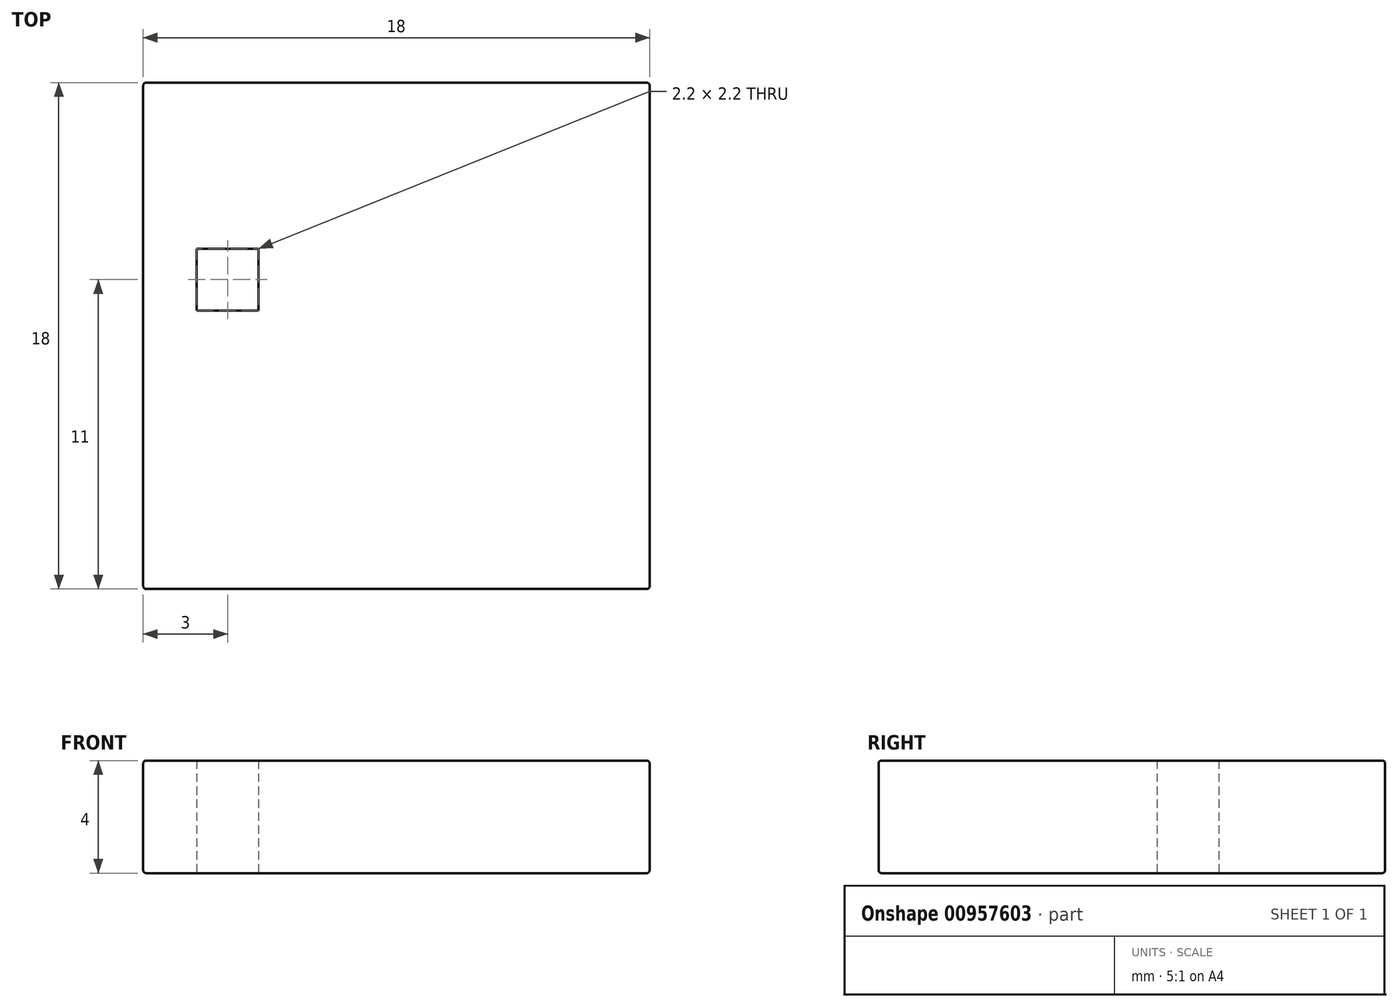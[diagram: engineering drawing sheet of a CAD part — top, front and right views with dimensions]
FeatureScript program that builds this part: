
annotation { "Feature Type Name" : "Feature", "Feature Type Description" : "" }
export const myFeature = defineFeature(function(context is Context, id is Id, definition is map)
    precondition{}
    {
        {
            var Q0;
            Q0=qCreatedBy(makeId("Top.planeOp"),FACE);
            var sketch = newSketch(context, id + "F0", { "sketchPlane" : qUnion([Q0])});
            skLineSegment(sketch, "E0.bottom", {"start": v(-9, 9) * mm, "end": v(9, 9) * mm});
            skLineSegment(sketch, "E0.top", {"start": v(-9, -9) * mm, "end": v(9, -9) * mm});
            skLineSegment(sketch, "E0.left", {"start": v(-9, 9) * mm, "end": v(-9, -9) * mm});
            skLineSegment(sketch, "E0.right", {"start": v(9, 9) * mm, "end": v(9, -9) * mm});
            skPoint(sketch, "E0.middle", {"position": v(0, 0) * mm});
            skLineSegment(sketch, "E1", {"start": v(-8, 9) * mm, "end": v(-8, -9) * mm});
            skLineSegment(sketch, "E2", {"start": v(-7.1, 9) * mm, "end": v(-7.1, -9) * mm});
            skLineSegment(sketch, "E3", {"start": v(-6.9, 9) * mm, "end": v(-6.9, -9) * mm});
            skLineSegment(sketch, "E4", {"start": v(-5.1, 9) * mm, "end": v(-5.1, -9) * mm});
            skLineSegment(sketch, "E5", {"start": v(-4.9, 9) * mm, "end": v(-4.9, -9) * mm});
            skLineSegment(sketch, "E6", {"start": v(-3.1, 9) * mm, "end": v(-3.1, -9) * mm});
            skLineSegment(sketch, "E7", {"start": v(-2.9, 9) * mm, "end": v(-2.9, -9) * mm});
            skLineSegment(sketch, "E8", {"start": v(-1.1, 9) * mm, "end": v(-1.1, -9) * mm});
            skLineSegment(sketch, "E9", {"start": v(-0.9, 9) * mm, "end": v(-0.9, -9) * mm});
            skLineSegment(sketch, "E10", {"start": v(0.9, 9) * mm, "end": v(0.9, -9) * mm});
            skLineSegment(sketch, "E11", {"start": v(1.1, 9) * mm, "end": v(1.1, -9) * mm});
            skLineSegment(sketch, "E12", {"start": v(2.9, 9) * mm, "end": v(2.9, -9) * mm});
            skLineSegment(sketch, "E13", {"start": v(3.1, 9) * mm, "end": v(3.1, -9) * mm});
            skLineSegment(sketch, "E14", {"start": v(4.9, 9) * mm, "end": v(4.9, -9) * mm});
            skLineSegment(sketch, "E15", {"start": v(5.1, 9) * mm, "end": v(5.1, -9) * mm});
            skLineSegment(sketch, "E16", {"start": v(6.9, 9) * mm, "end": v(6.9, -9) * mm});
            skLineSegment(sketch, "E17", {"start": v(7.1, 9) * mm, "end": v(7.1, -9) * mm});
            skLineSegment(sketch, "E18", {"start": v(8, 9) * mm, "end": v(8, -9) * mm});
            skLineSegment(sketch, "E19", {"start": v(9, 8) * mm, "end": v(-9, 8) * mm});
            skLineSegment(sketch, "E20", {"start": v(9, 7.1) * mm, "end": v(-9, 7.1) * mm});
            skLineSegment(sketch, "E21", {"start": v(9, 6.9) * mm, "end": v(-9, 6.9) * mm});
            skLineSegment(sketch, "E22", {"start": v(9, 5.1) * mm, "end": v(-9, 5.1) * mm});
            skLineSegment(sketch, "E23", {"start": v(9, 4.9) * mm, "end": v(-9, 4.9) * mm});
            skLineSegment(sketch, "E24", {"start": v(9, 3.1) * mm, "end": v(-9, 3.1) * mm});
            skLineSegment(sketch, "E25", {"start": v(9, 2.9) * mm, "end": v(-9, 2.9) * mm});
            skLineSegment(sketch, "E26", {"start": v(9, 1.1) * mm, "end": v(-9, 1.1) * mm});
            skLineSegment(sketch, "E27", {"start": v(9, 0.9) * mm, "end": v(-9, 0.9) * mm});
            skLineSegment(sketch, "E28", {"start": v(9, -0.9) * mm, "end": v(-9, -0.9) * mm});
            skLineSegment(sketch, "E29", {"start": v(9, -1.1) * mm, "end": v(-9, -1.1) * mm});
            skLineSegment(sketch, "E30", {"start": v(9, -2.9) * mm, "end": v(-9, -2.9) * mm});
            skLineSegment(sketch, "E31", {"start": v(9, -3.1) * mm, "end": v(-9, -3.1) * mm});
            skLineSegment(sketch, "E32", {"start": v(9, -4.9) * mm, "end": v(-9, -4.9) * mm});
            skLineSegment(sketch, "E33", {"start": v(9, -5.1) * mm, "end": v(-9, -5.1) * mm});
            skLineSegment(sketch, "E34", {"start": v(9, -6.9) * mm, "end": v(-9, -6.9) * mm});
            skLineSegment(sketch, "E35", {"start": v(9, -7.1) * mm, "end": v(-9, -7.1) * mm});
            skLineSegment(sketch, "E36", {"start": v(9, -8) * mm, "end": v(-9, -8) * mm});
            skSolve(sketch);
        }
        {
            var Q0;
            {var subQ0=sQuery(id+"F0.wireOp",EDGE,"E30");var subQ1=sQuery(id+"F0.wireOp",EDGE,"E10");var subQ2=makeQuery(id+"F0.imprint","INTERSECT",VERTEX,{"derivedFrom":[subQ1,subQ0]});Q0=makeQuery(id+"F0.imprint","IMPRINT",FACE,{"disambiguationData":[TD([[makeQuery(id+"F0.imprint","IMPRINT",EDGE,{"disambiguationData":[TD([[subQ2,-1.0]])],"derivedFrom":subQ1}),1.0]])]});}
            var Q1;
            {var subQ0=sQuery(id+"F0.wireOp",EDGE,"E26");var subQ1=sQuery(id+"F0.wireOp",EDGE,"E11");var subQ2=makeQuery(id+"F0.imprint","INTERSECT",VERTEX,{"derivedFrom":[subQ1,subQ0]});Q1=makeQuery(id+"F0.imprint","IMPRINT",FACE,{"disambiguationData":[TD([[makeQuery(id+"F0.imprint","IMPRINT",EDGE,{"disambiguationData":[TD([[subQ2,-1.0]])],"derivedFrom":subQ1}),1.0]])]});}
            var Q2;
            {var subQ0=sQuery(id+"F0.wireOp",EDGE,"E25");var subQ1=sQuery(id+"F0.wireOp",EDGE,"E8");var subQ2=makeQuery(id+"F0.imprint","INTERSECT",VERTEX,{"derivedFrom":[subQ1,subQ0]});Q2=makeQuery(id+"F0.imprint","IMPRINT",FACE,{"disambiguationData":[TD([[makeQuery(id+"F0.imprint","IMPRINT",EDGE,{"disambiguationData":[TD([[subQ2,-1.0]])],"derivedFrom":subQ1}),1.0]])]});}
            var Q3;
            {var subQ0=sQuery(id+"F0.wireOp",EDGE,"E24");var subQ1=sQuery(id+"F0.wireOp",EDGE,"E10");var subQ2=makeQuery(id+"F0.imprint","INTERSECT",VERTEX,{"derivedFrom":[subQ1,subQ0]});Q3=makeQuery(id+"F0.imprint","IMPRINT",FACE,{"disambiguationData":[TD([[makeQuery(id+"F0.imprint","IMPRINT",EDGE,{"disambiguationData":[TD([[subQ2,-1.0]])],"derivedFrom":subQ1}),1.0]])]});}
            var Q4;
            {var subQ0=sQuery(id+"F0.wireOp",EDGE,"E30");var subQ1=sQuery(id+"F0.wireOp",EDGE,"E15");var subQ2=makeQuery(id+"F0.imprint","INTERSECT",VERTEX,{"derivedFrom":[subQ1,subQ0]});Q4=makeQuery(id+"F0.imprint","IMPRINT",FACE,{"disambiguationData":[TD([[makeQuery(id+"F0.imprint","IMPRINT",EDGE,{"disambiguationData":[TD([[subQ2,-1.0]])],"derivedFrom":subQ1}),1.0]])]});}
            var Q5;
            {var subQ0=sQuery(id+"F0.wireOp",EDGE,"E35");var subQ1=sQuery(id+"F0.wireOp",EDGE,"E12");var subQ2=makeQuery(id+"F0.imprint","INTERSECT",VERTEX,{"derivedFrom":[subQ1,subQ0]});Q5=makeQuery(id+"F0.imprint","IMPRINT",FACE,{"disambiguationData":[TD([[makeQuery(id+"F0.imprint","IMPRINT",EDGE,{"disambiguationData":[TD([[subQ2,-1.0]])],"derivedFrom":subQ1}),1.0]])]});}
            var Q6;
            {var subQ0=sQuery(id+"F0.wireOp",EDGE,"E35");var subQ1=sQuery(id+"F0.wireOp",EDGE,"E14");var subQ2=makeQuery(id+"F0.imprint","INTERSECT",VERTEX,{"derivedFrom":[subQ1,subQ0]});Q6=makeQuery(id+"F0.imprint","IMPRINT",FACE,{"disambiguationData":[TD([[makeQuery(id+"F0.imprint","IMPRINT",EDGE,{"disambiguationData":[TD([[subQ2,-1.0]])],"derivedFrom":subQ1}),1.0]])]});}
            var Q7;
            {var subQ0=sQuery(id+"F0.wireOp",EDGE,"E32");var subQ1=sQuery(id+"F0.wireOp",EDGE,"E10");var subQ2=makeQuery(id+"F0.imprint","INTERSECT",VERTEX,{"derivedFrom":[subQ1,subQ0]});Q7=makeQuery(id+"F0.imprint","IMPRINT",FACE,{"disambiguationData":[TD([[makeQuery(id+"F0.imprint","IMPRINT",EDGE,{"disambiguationData":[TD([[subQ2,-1.0]])],"derivedFrom":subQ1}),1.0]])]});}
            var Q8;
            {var subQ0=sQuery(id+"F0.wireOp",EDGE,"E23");var subQ1=sQuery(id+"F0.wireOp",EDGE,"E14");var subQ2=makeQuery(id+"F0.imprint","INTERSECT",VERTEX,{"derivedFrom":[subQ1,subQ0]});Q8=makeQuery(id+"F0.imprint","IMPRINT",FACE,{"disambiguationData":[TD([[makeQuery(id+"F0.imprint","IMPRINT",EDGE,{"disambiguationData":[TD([[subQ2,-1.0]])],"derivedFrom":subQ1}),1.0]])]});}
            var Q9;
            {var subQ0=sQuery(id+"F0.wireOp",EDGE,"E23");var subQ1=sQuery(id+"F0.wireOp",EDGE,"E16");var subQ2=makeQuery(id+"F0.imprint","INTERSECT",VERTEX,{"derivedFrom":[subQ1,subQ0]});Q9=makeQuery(id+"F0.imprint","IMPRINT",FACE,{"disambiguationData":[TD([[makeQuery(id+"F0.imprint","IMPRINT",EDGE,{"disambiguationData":[TD([[subQ2,-1.0]])],"derivedFrom":subQ1}),1.0]])]});}
            var Q10;
            {var subQ0=sQuery(id+"F0.wireOp",EDGE,"E22");var subQ1=sQuery(id+"F0.wireOp",EDGE,"E9");var subQ2=makeQuery(id+"F0.imprint","INTERSECT",VERTEX,{"derivedFrom":[subQ1,subQ0]});Q10=makeQuery(id+"F0.imprint","IMPRINT",FACE,{"disambiguationData":[TD([[makeQuery(id+"F0.imprint","IMPRINT",EDGE,{"disambiguationData":[TD([[subQ2,-1.0]])],"derivedFrom":subQ1}),1.0]])]});}
            var Q11;
            {var subQ0=sQuery(id+"F0.wireOp",EDGE,"E27");var subQ1=sQuery(id+"F0.wireOp",EDGE,"E10");var subQ2=makeQuery(id+"F0.imprint","INTERSECT",VERTEX,{"derivedFrom":[subQ1,subQ0]});Q11=makeQuery(id+"F0.imprint","IMPRINT",FACE,{"disambiguationData":[TD([[makeQuery(id+"F0.imprint","IMPRINT",EDGE,{"disambiguationData":[TD([[subQ2,-1.0]])],"derivedFrom":subQ1}),1.0]])]});}
            var Q12;
            {var subQ0=sQuery(id+"F0.wireOp",EDGE,"E31");var subQ1=sQuery(id+"F0.wireOp",EDGE,"E2");var subQ2=makeQuery(id+"F0.imprint","INTERSECT",VERTEX,{"derivedFrom":[subQ1,subQ0]});Q12=makeQuery(id+"F0.imprint","IMPRINT",FACE,{"disambiguationData":[TD([[makeQuery(id+"F0.imprint","IMPRINT",EDGE,{"disambiguationData":[TD([[subQ2,-1.0]])],"derivedFrom":subQ1}),1.0]])]});}
            var Q13;
            {var subQ0=sQuery(id+"F0.wireOp",EDGE,"E30");var subQ1=sQuery(id+"F0.wireOp",EDGE,"E13");var subQ2=makeQuery(id+"F0.imprint","INTERSECT",VERTEX,{"derivedFrom":[subQ1,subQ0]});Q13=makeQuery(id+"F0.imprint","IMPRINT",FACE,{"disambiguationData":[TD([[makeQuery(id+"F0.imprint","IMPRINT",EDGE,{"disambiguationData":[TD([[subQ2,-1.0]])],"derivedFrom":subQ1}),1.0]])]});}
            var Q14;
            {var subQ0=sQuery(id+"F0.wireOp",EDGE,"E33");var subQ1=sQuery(id+"F0.wireOp",EDGE,"E16");var subQ2=makeQuery(id+"F0.imprint","INTERSECT",VERTEX,{"derivedFrom":[subQ1,subQ0]});Q14=makeQuery(id+"F0.imprint","IMPRINT",FACE,{"disambiguationData":[TD([[makeQuery(id+"F0.imprint","IMPRINT",EDGE,{"disambiguationData":[TD([[subQ2,-1.0]])],"derivedFrom":subQ1}),1.0]])]});}
            var Q15;
            {var subQ0=sQuery(id+"F0.wireOp",EDGE,"E29");var subQ1=sQuery(id+"F0.wireOp",EDGE,"E8");var subQ2=makeQuery(id+"F0.imprint","INTERSECT",VERTEX,{"derivedFrom":[subQ1,subQ0]});Q15=makeQuery(id+"F0.imprint","IMPRINT",FACE,{"disambiguationData":[TD([[makeQuery(id+"F0.imprint","IMPRINT",EDGE,{"disambiguationData":[TD([[subQ2,-1.0]])],"derivedFrom":subQ1}),1.0]])]});}
            var Q16;
            {var subQ0=sQuery(id+"F0.wireOp",EDGE,"E26");var subQ1=sQuery(id+"F0.wireOp",EDGE,"E1");var subQ2=makeQuery(id+"F0.imprint","INTERSECT",VERTEX,{"derivedFrom":[subQ1,subQ0]});Q16=makeQuery(id+"F0.imprint","IMPRINT",FACE,{"disambiguationData":[TD([[makeQuery(id+"F0.imprint","IMPRINT",EDGE,{"disambiguationData":[TD([[subQ2,-1.0]])],"derivedFrom":subQ1}),1.0]])]});}
            var Q17;
            {var subQ0=sQuery(id+"F0.wireOp",EDGE,"E30");var subQ1=sQuery(id+"F0.wireOp",EDGE,"E12");var subQ2=makeQuery(id+"F0.imprint","INTERSECT",VERTEX,{"derivedFrom":[subQ1,subQ0]});Q17=makeQuery(id+"F0.imprint","IMPRINT",FACE,{"disambiguationData":[TD([[makeQuery(id+"F0.imprint","IMPRINT",EDGE,{"disambiguationData":[TD([[subQ2,-1.0]])],"derivedFrom":subQ1}),1.0]])]});}
            var Q18;
            {var subQ0=sQuery(id+"F0.wireOp",EDGE,"E29");var subQ1=sQuery(id+"F0.wireOp",EDGE,"E12");var subQ2=makeQuery(id+"F0.imprint","INTERSECT",VERTEX,{"derivedFrom":[subQ1,subQ0]});Q18=makeQuery(id+"F0.imprint","IMPRINT",FACE,{"disambiguationData":[TD([[makeQuery(id+"F0.imprint","IMPRINT",EDGE,{"disambiguationData":[TD([[subQ2,-1.0]])],"derivedFrom":subQ1}),1.0]])]});}
            var Q19;
            {var subQ0=sQuery(id+"F0.wireOp",EDGE,"E31");var subQ1=sQuery(id+"F0.wireOp",EDGE,"E6");var subQ2=makeQuery(id+"F0.imprint","INTERSECT",VERTEX,{"derivedFrom":[subQ1,subQ0]});Q19=makeQuery(id+"F0.imprint","IMPRINT",FACE,{"disambiguationData":[TD([[makeQuery(id+"F0.imprint","IMPRINT",EDGE,{"disambiguationData":[TD([[subQ2,-1.0]])],"derivedFrom":subQ1}),1.0]])]});}
            var Q20;
            {var subQ0=sQuery(id+"F0.wireOp",EDGE,"E29");var subQ1=sQuery(id+"F0.wireOp",EDGE,"E10");var subQ2=makeQuery(id+"F0.imprint","INTERSECT",VERTEX,{"derivedFrom":[subQ1,subQ0]});Q20=makeQuery(id+"F0.imprint","IMPRINT",FACE,{"disambiguationData":[TD([[makeQuery(id+"F0.imprint","IMPRINT",EDGE,{"disambiguationData":[TD([[subQ2,-1.0]])],"derivedFrom":subQ1}),1.0]])]});}
            var Q21;
            {var subQ0=sQuery(id+"F0.wireOp",EDGE,"E25");var subQ1=sQuery(id+"F0.wireOp",EDGE,"E16");var subQ2=makeQuery(id+"F0.imprint","INTERSECT",VERTEX,{"derivedFrom":[subQ1,subQ0]});Q21=makeQuery(id+"F0.imprint","IMPRINT",FACE,{"disambiguationData":[TD([[makeQuery(id+"F0.imprint","IMPRINT",EDGE,{"disambiguationData":[TD([[subQ2,-1.0]])],"derivedFrom":subQ1}),1.0]])]});}
            var Q22;
            {var subQ0=sQuery(id+"F0.wireOp",EDGE,"E35");var subQ1=sQuery(id+"F0.wireOp",EDGE,"E16");var subQ2=makeQuery(id+"F0.imprint","INTERSECT",VERTEX,{"derivedFrom":[subQ1,subQ0]});Q22=makeQuery(id+"F0.imprint","IMPRINT",FACE,{"disambiguationData":[TD([[makeQuery(id+"F0.imprint","IMPRINT",EDGE,{"disambiguationData":[TD([[subQ2,-1.0]])],"derivedFrom":subQ1}),1.0]])]});}
            var Q23;
            {var subQ0=sQuery(id+"F0.wireOp",EDGE,"E31");var subQ1=sQuery(id+"F0.wireOp",EDGE,"E12");var subQ2=makeQuery(id+"F0.imprint","INTERSECT",VERTEX,{"derivedFrom":[subQ1,subQ0]});Q23=makeQuery(id+"F0.imprint","IMPRINT",FACE,{"disambiguationData":[TD([[makeQuery(id+"F0.imprint","IMPRINT",EDGE,{"disambiguationData":[TD([[subQ2,-1.0]])],"derivedFrom":subQ1}),1.0]])]});}
            var Q24;
            {var subQ0=sQuery(id+"F0.wireOp",EDGE,"E24");var subQ1=sQuery(id+"F0.wireOp",EDGE,"E1");var subQ2=makeQuery(id+"F0.imprint","INTERSECT",VERTEX,{"derivedFrom":[subQ1,subQ0]});Q24=makeQuery(id+"F0.imprint","IMPRINT",FACE,{"disambiguationData":[TD([[makeQuery(id+"F0.imprint","IMPRINT",EDGE,{"disambiguationData":[TD([[subQ2,-1.0]])],"derivedFrom":subQ1}),1.0]])]});}
            var Q25;
            {var subQ0=sQuery(id+"F0.wireOp",EDGE,"E27");var subQ1=sQuery(id+"F0.wireOp",EDGE,"E16");var subQ2=makeQuery(id+"F0.imprint","INTERSECT",VERTEX,{"derivedFrom":[subQ1,subQ0]});Q25=makeQuery(id+"F0.imprint","IMPRINT",FACE,{"disambiguationData":[TD([[makeQuery(id+"F0.imprint","IMPRINT",EDGE,{"disambiguationData":[TD([[subQ2,-1.0]])],"derivedFrom":subQ1}),1.0]])]});}
            var Q26;
            {var subQ0=sQuery(id+"F0.wireOp",EDGE,"E26");var subQ1=sQuery(id+"F0.wireOp",EDGE,"E9");var subQ2=makeQuery(id+"F0.imprint","INTERSECT",VERTEX,{"derivedFrom":[subQ1,subQ0]});Q26=makeQuery(id+"F0.imprint","IMPRINT",FACE,{"disambiguationData":[TD([[makeQuery(id+"F0.imprint","IMPRINT",EDGE,{"disambiguationData":[TD([[subQ2,-1.0]])],"derivedFrom":subQ1}),1.0]])]});}
            var Q27;
            {var subQ0=sQuery(id+"F0.wireOp",EDGE,"E35");var subQ1=sQuery(id+"F0.wireOp",EDGE,"E2");var subQ2=makeQuery(id+"F0.imprint","INTERSECT",VERTEX,{"derivedFrom":[subQ1,subQ0]});Q27=makeQuery(id+"F0.imprint","IMPRINT",FACE,{"disambiguationData":[TD([[makeQuery(id+"F0.imprint","IMPRINT",EDGE,{"disambiguationData":[TD([[subQ2,-1.0]])],"derivedFrom":subQ1}),1.0]])]});}
            var Q28;
            {var subQ0=sQuery(id+"F0.wireOp",EDGE,"E22");var subQ1=sQuery(id+"F0.wireOp",EDGE,"E16");var subQ2=makeQuery(id+"F0.imprint","INTERSECT",VERTEX,{"derivedFrom":[subQ1,subQ0]});Q28=makeQuery(id+"F0.imprint","IMPRINT",FACE,{"disambiguationData":[TD([[makeQuery(id+"F0.imprint","IMPRINT",EDGE,{"disambiguationData":[TD([[subQ2,-1.0]])],"derivedFrom":subQ1}),1.0]])]});}
            var Q29;
            {var subQ0=sQuery(id+"F0.wireOp",EDGE,"E35");var subQ1=sQuery(id+"F0.wireOp",EDGE,"E8");var subQ2=makeQuery(id+"F0.imprint","INTERSECT",VERTEX,{"derivedFrom":[subQ1,subQ0]});Q29=makeQuery(id+"F0.imprint","IMPRINT",FACE,{"disambiguationData":[TD([[makeQuery(id+"F0.imprint","IMPRINT",EDGE,{"disambiguationData":[TD([[subQ2,-1.0]])],"derivedFrom":subQ1}),1.0]])]});}
            var Q30;
            {var subQ0=sQuery(id+"F0.wireOp",EDGE,"E24");var subQ1=sQuery(id+"F0.wireOp",EDGE,"E7");var subQ2=makeQuery(id+"F0.imprint","INTERSECT",VERTEX,{"derivedFrom":[subQ1,subQ0]});Q30=makeQuery(id+"F0.imprint","IMPRINT",FACE,{"disambiguationData":[TD([[makeQuery(id+"F0.imprint","IMPRINT",EDGE,{"disambiguationData":[TD([[subQ2,-1.0]])],"derivedFrom":subQ1}),1.0]])]});}
            var Q31;
            {var subQ0=sQuery(id+"F0.wireOp",EDGE,"E21");var subQ1=sQuery(id+"F0.wireOp",EDGE,"E16");var subQ2=makeQuery(id+"F0.imprint","INTERSECT",VERTEX,{"derivedFrom":[subQ1,subQ0]});Q31=makeQuery(id+"F0.imprint","IMPRINT",FACE,{"disambiguationData":[TD([[makeQuery(id+"F0.imprint","IMPRINT",EDGE,{"disambiguationData":[TD([[subQ2,-1.0]])],"derivedFrom":subQ1}),1.0]])]});}
            var Q32;
            {var subQ0=sQuery(id+"F0.wireOp",EDGE,"E32");var subQ1=sQuery(id+"F0.wireOp",EDGE,"E11");var subQ2=makeQuery(id+"F0.imprint","INTERSECT",VERTEX,{"derivedFrom":[subQ1,subQ0]});Q32=makeQuery(id+"F0.imprint","IMPRINT",FACE,{"disambiguationData":[TD([[makeQuery(id+"F0.imprint","IMPRINT",EDGE,{"disambiguationData":[TD([[subQ2,-1.0]])],"derivedFrom":subQ1}),1.0]])]});}
            var Q33;
            {var subQ0=sQuery(id+"F0.wireOp",EDGE,"E33");var subQ1=sQuery(id+"F0.wireOp",EDGE,"E8");var subQ2=makeQuery(id+"F0.imprint","INTERSECT",VERTEX,{"derivedFrom":[subQ1,subQ0]});Q33=makeQuery(id+"F0.imprint","IMPRINT",FACE,{"disambiguationData":[TD([[makeQuery(id+"F0.imprint","IMPRINT",EDGE,{"disambiguationData":[TD([[subQ2,-1.0]])],"derivedFrom":subQ1}),1.0]])]});}
            var Q34;
            {var subQ0=sQuery(id+"F0.wireOp",EDGE,"E30");var subQ1=sQuery(id+"F0.wireOp",EDGE,"E9");var subQ2=makeQuery(id+"F0.imprint","INTERSECT",VERTEX,{"derivedFrom":[subQ1,subQ0]});Q34=makeQuery(id+"F0.imprint","IMPRINT",FACE,{"disambiguationData":[TD([[makeQuery(id+"F0.imprint","IMPRINT",EDGE,{"disambiguationData":[TD([[subQ2,-1.0]])],"derivedFrom":subQ1}),1.0]])]});}
            var Q35;
            {var subQ0=sQuery(id+"F0.wireOp",EDGE,"E22");var subQ1=sQuery(id+"F0.wireOp",EDGE,"E8");var subQ2=makeQuery(id+"F0.imprint","INTERSECT",VERTEX,{"derivedFrom":[subQ1,subQ0]});Q35=makeQuery(id+"F0.imprint","IMPRINT",FACE,{"disambiguationData":[TD([[makeQuery(id+"F0.imprint","IMPRINT",EDGE,{"disambiguationData":[TD([[subQ2,-1.0]])],"derivedFrom":subQ1}),1.0]])]});}
            var Q36;
            {var subQ0=sQuery(id+"F0.wireOp",EDGE,"E27");var subQ1=sQuery(id+"F0.wireOp",EDGE,"E2");var subQ2=makeQuery(id+"F0.imprint","INTERSECT",VERTEX,{"derivedFrom":[subQ1,subQ0]});Q36=makeQuery(id+"F0.imprint","IMPRINT",FACE,{"disambiguationData":[TD([[makeQuery(id+"F0.imprint","IMPRINT",EDGE,{"disambiguationData":[TD([[subQ2,-1.0]])],"derivedFrom":subQ1}),1.0]])]});}
            var Q37;
            {var subQ0=sQuery(id+"F0.wireOp",EDGE,"E30");var subQ1=sQuery(id+"F0.wireOp",EDGE,"E11");var subQ2=makeQuery(id+"F0.imprint","INTERSECT",VERTEX,{"derivedFrom":[subQ1,subQ0]});Q37=makeQuery(id+"F0.imprint","IMPRINT",FACE,{"disambiguationData":[TD([[makeQuery(id+"F0.imprint","IMPRINT",EDGE,{"disambiguationData":[TD([[subQ2,-1.0]])],"derivedFrom":subQ1}),1.0]])]});}
            var Q38;
            {var subQ0=sQuery(id+"F0.wireOp",EDGE,"E26");var subQ1=sQuery(id+"F0.wireOp",EDGE,"E5");var subQ2=makeQuery(id+"F0.imprint","INTERSECT",VERTEX,{"derivedFrom":[subQ1,subQ0]});Q38=makeQuery(id+"F0.imprint","IMPRINT",FACE,{"disambiguationData":[TD([[makeQuery(id+"F0.imprint","IMPRINT",EDGE,{"disambiguationData":[TD([[subQ2,-1.0]])],"derivedFrom":subQ1}),1.0]])]});}
            var Q39;
            {var subQ0=sQuery(id+"F0.wireOp",EDGE,"E31");var subQ1=sQuery(id+"F0.wireOp",EDGE,"E8");var subQ2=makeQuery(id+"F0.imprint","INTERSECT",VERTEX,{"derivedFrom":[subQ1,subQ0]});Q39=makeQuery(id+"F0.imprint","IMPRINT",FACE,{"disambiguationData":[TD([[makeQuery(id+"F0.imprint","IMPRINT",EDGE,{"disambiguationData":[TD([[subQ2,-1.0]])],"derivedFrom":subQ1}),1.0]])]});}
            var Q40;
            {var subQ0=sQuery(id+"F0.wireOp",EDGE,"E32");var subQ1=sQuery(id+"F0.wireOp",EDGE,"E7");var subQ2=makeQuery(id+"F0.imprint","INTERSECT",VERTEX,{"derivedFrom":[subQ1,subQ0]});Q40=makeQuery(id+"F0.imprint","IMPRINT",FACE,{"disambiguationData":[TD([[makeQuery(id+"F0.imprint","IMPRINT",EDGE,{"disambiguationData":[TD([[subQ2,-1.0]])],"derivedFrom":subQ1}),1.0]])]});}
            var Q41;
            {var subQ0=sQuery(id+"F0.wireOp",EDGE,"E24");var subQ1=sQuery(id+"F0.wireOp",EDGE,"E17");var subQ2=makeQuery(id+"F0.imprint","INTERSECT",VERTEX,{"derivedFrom":[subQ1,subQ0]});Q41=makeQuery(id+"F0.imprint","IMPRINT",FACE,{"disambiguationData":[TD([[makeQuery(id+"F0.imprint","IMPRINT",EDGE,{"disambiguationData":[TD([[subQ2,-1.0]])],"derivedFrom":subQ1}),1.0]])]});}
            var Q42;
            {var subQ0=sQuery(id+"F0.wireOp",EDGE,"E26");var subQ1=sQuery(id+"F0.wireOp",EDGE,"E14");var subQ2=makeQuery(id+"F0.imprint","INTERSECT",VERTEX,{"derivedFrom":[subQ1,subQ0]});Q42=makeQuery(id+"F0.imprint","IMPRINT",FACE,{"disambiguationData":[TD([[makeQuery(id+"F0.imprint","IMPRINT",EDGE,{"disambiguationData":[TD([[subQ2,-1.0]])],"derivedFrom":subQ1}),1.0]])]});}
            var Q43;
            {var subQ0=sQuery(id+"F0.wireOp",EDGE,"E31");var subQ1=sQuery(id+"F0.wireOp",EDGE,"E14");var subQ2=makeQuery(id+"F0.imprint","INTERSECT",VERTEX,{"derivedFrom":[subQ1,subQ0]});Q43=makeQuery(id+"F0.imprint","IMPRINT",FACE,{"disambiguationData":[TD([[makeQuery(id+"F0.imprint","IMPRINT",EDGE,{"disambiguationData":[TD([[subQ2,-1.0]])],"derivedFrom":subQ1}),1.0]])]});}
            var Q44;
            {var subQ0=sQuery(id+"F0.wireOp",EDGE,"E24");var subQ1=sQuery(id+"F0.wireOp",EDGE,"E5");var subQ2=makeQuery(id+"F0.imprint","INTERSECT",VERTEX,{"derivedFrom":[subQ1,subQ0]});Q44=makeQuery(id+"F0.imprint","IMPRINT",FACE,{"disambiguationData":[TD([[makeQuery(id+"F0.imprint","IMPRINT",EDGE,{"disambiguationData":[TD([[subQ2,-1.0]])],"derivedFrom":subQ1}),1.0]])]});}
            var Q45;
            {var subQ0=sQuery(id+"F0.wireOp",EDGE,"E26");var subQ1=sQuery(id+"F0.wireOp",EDGE,"E12");var subQ2=makeQuery(id+"F0.imprint","INTERSECT",VERTEX,{"derivedFrom":[subQ1,subQ0]});Q45=makeQuery(id+"F0.imprint","IMPRINT",FACE,{"disambiguationData":[TD([[makeQuery(id+"F0.imprint","IMPRINT",EDGE,{"disambiguationData":[TD([[subQ2,-1.0]])],"derivedFrom":subQ1}),1.0]])]});}
            var Q46;
            {var subQ0=sQuery(id+"F0.wireOp",EDGE,"E30");var subQ1=sQuery(id+"F0.wireOp",EDGE,"E5");var subQ2=makeQuery(id+"F0.imprint","INTERSECT",VERTEX,{"derivedFrom":[subQ1,subQ0]});Q46=makeQuery(id+"F0.imprint","IMPRINT",FACE,{"disambiguationData":[TD([[makeQuery(id+"F0.imprint","IMPRINT",EDGE,{"disambiguationData":[TD([[subQ2,-1.0]])],"derivedFrom":subQ1}),1.0]])]});}
            var Q47;
            {var subQ0=sQuery(id+"F0.wireOp",EDGE,"E33");var subQ1=sQuery(id+"F0.wireOp",EDGE,"E14");var subQ2=makeQuery(id+"F0.imprint","INTERSECT",VERTEX,{"derivedFrom":[subQ1,subQ0]});Q47=makeQuery(id+"F0.imprint","IMPRINT",FACE,{"disambiguationData":[TD([[makeQuery(id+"F0.imprint","IMPRINT",EDGE,{"disambiguationData":[TD([[subQ2,-1.0]])],"derivedFrom":subQ1}),1.0]])]});}
            var Q48;
            {var subQ0=sQuery(id+"F0.wireOp",EDGE,"E32");var subQ1=sQuery(id+"F0.wireOp",EDGE,"E9");var subQ2=makeQuery(id+"F0.imprint","INTERSECT",VERTEX,{"derivedFrom":[subQ1,subQ0]});Q48=makeQuery(id+"F0.imprint","IMPRINT",FACE,{"disambiguationData":[TD([[makeQuery(id+"F0.imprint","IMPRINT",EDGE,{"disambiguationData":[TD([[subQ2,-1.0]])],"derivedFrom":subQ1}),1.0]])]});}
            var Q49;
            {var subQ0=sQuery(id+"F0.wireOp",EDGE,"E25");var subQ1=sQuery(id+"F0.wireOp",EDGE,"E6");var subQ2=makeQuery(id+"F0.imprint","INTERSECT",VERTEX,{"derivedFrom":[subQ1,subQ0]});Q49=makeQuery(id+"F0.imprint","IMPRINT",FACE,{"disambiguationData":[TD([[makeQuery(id+"F0.imprint","IMPRINT",EDGE,{"disambiguationData":[TD([[subQ2,-1.0]])],"derivedFrom":subQ1}),1.0]])]});}
            var Q50;
            {var subQ0=sQuery(id+"F0.wireOp",EDGE,"E19");var subQ1=sQuery(id+"F0.wireOp",EDGE,"E16");var subQ2=makeQuery(id+"F0.imprint","INTERSECT",VERTEX,{"derivedFrom":[subQ1,subQ0]});Q50=makeQuery(id+"F0.imprint","IMPRINT",FACE,{"disambiguationData":[TD([[makeQuery(id+"F0.imprint","IMPRINT",EDGE,{"disambiguationData":[TD([[subQ2,-1.0]])],"derivedFrom":subQ1}),1.0]])]});}
            var Q51;
            {var subQ0=sQuery(id+"F0.wireOp",EDGE,"E19");var subQ1=sQuery(id+"F0.wireOp",EDGE,"E10");var subQ2=makeQuery(id+"F0.imprint","INTERSECT",VERTEX,{"derivedFrom":[subQ1,subQ0]});Q51=makeQuery(id+"F0.imprint","IMPRINT",FACE,{"disambiguationData":[TD([[makeQuery(id+"F0.imprint","IMPRINT",EDGE,{"disambiguationData":[TD([[subQ2,-1.0]])],"derivedFrom":subQ1}),1.0]])]});}
            var Q52;
            {var subQ0=sQuery(id+"F0.wireOp",EDGE,"E19");var subQ1=sQuery(id+"F0.wireOp",EDGE,"E2");var subQ2=makeQuery(id+"F0.imprint","INTERSECT",VERTEX,{"derivedFrom":[subQ1,subQ0]});Q52=makeQuery(id+"F0.imprint","IMPRINT",FACE,{"disambiguationData":[TD([[makeQuery(id+"F0.imprint","IMPRINT",EDGE,{"disambiguationData":[TD([[subQ2,-1.0]])],"derivedFrom":subQ1}),1.0]])]});}
            var Q53;
            {var subQ0=sQuery(id+"F0.wireOp",EDGE,"E32");var subQ1=sQuery(id+"F0.wireOp",EDGE,"E17");var subQ2=makeQuery(id+"F0.imprint","INTERSECT",VERTEX,{"derivedFrom":[subQ1,subQ0]});Q53=makeQuery(id+"F0.imprint","IMPRINT",FACE,{"disambiguationData":[TD([[makeQuery(id+"F0.imprint","IMPRINT",EDGE,{"disambiguationData":[TD([[subQ2,-1.0]])],"derivedFrom":subQ1}),1.0]])]});}
            var Q54;
            {var subQ0=sQuery(id+"F0.wireOp",EDGE,"E30");var subQ1=sQuery(id+"F0.wireOp",EDGE,"E17");var subQ2=makeQuery(id+"F0.imprint","INTERSECT",VERTEX,{"derivedFrom":[subQ1,subQ0]});Q54=makeQuery(id+"F0.imprint","IMPRINT",FACE,{"disambiguationData":[TD([[makeQuery(id+"F0.imprint","IMPRINT",EDGE,{"disambiguationData":[TD([[subQ2,-1.0]])],"derivedFrom":subQ1}),1.0]])]});}
            var Q55;
            {var subQ0=sQuery(id+"F0.wireOp",EDGE,"E33");var subQ1=sQuery(id+"F0.wireOp",EDGE,"E12");var subQ2=makeQuery(id+"F0.imprint","INTERSECT",VERTEX,{"derivedFrom":[subQ1,subQ0]});Q55=makeQuery(id+"F0.imprint","IMPRINT",FACE,{"disambiguationData":[TD([[makeQuery(id+"F0.imprint","IMPRINT",EDGE,{"disambiguationData":[TD([[subQ2,-1.0]])],"derivedFrom":subQ1}),1.0]])]});}
            var Q56;
            {var subQ0=sQuery(id+"F0.wireOp",EDGE,"E24");var subQ1=sQuery(id+"F0.wireOp",EDGE,"E8");var subQ2=makeQuery(id+"F0.imprint","INTERSECT",VERTEX,{"derivedFrom":[subQ1,subQ0]});Q56=makeQuery(id+"F0.imprint","IMPRINT",FACE,{"disambiguationData":[TD([[makeQuery(id+"F0.imprint","IMPRINT",EDGE,{"disambiguationData":[TD([[subQ2,-1.0]])],"derivedFrom":subQ1}),1.0]])]});}
            var Q57;
            {var subQ0=sQuery(id+"F0.wireOp",EDGE,"E22");var subQ1=sQuery(id+"F0.wireOp",EDGE,"E13");var subQ2=makeQuery(id+"F0.imprint","INTERSECT",VERTEX,{"derivedFrom":[subQ1,subQ0]});Q57=makeQuery(id+"F0.imprint","IMPRINT",FACE,{"disambiguationData":[TD([[makeQuery(id+"F0.imprint","IMPRINT",EDGE,{"disambiguationData":[TD([[subQ2,-1.0]])],"derivedFrom":subQ1}),1.0]])]});}
            var Q58;
            {var subQ0=sQuery(id+"F0.wireOp",EDGE,"E19");var subQ1=sQuery(id+"F0.wireOp",EDGE,"E14");var subQ2=makeQuery(id+"F0.imprint","INTERSECT",VERTEX,{"derivedFrom":[subQ1,subQ0]});Q58=makeQuery(id+"F0.imprint","IMPRINT",FACE,{"disambiguationData":[TD([[makeQuery(id+"F0.imprint","IMPRINT",EDGE,{"disambiguationData":[TD([[subQ2,-1.0]])],"derivedFrom":subQ1}),1.0]])]});}
            var Q59;
            {var subQ0=sQuery(id+"F0.wireOp",EDGE,"E32");var subQ1=sQuery(id+"F0.wireOp",EDGE,"E16");var subQ2=makeQuery(id+"F0.imprint","INTERSECT",VERTEX,{"derivedFrom":[subQ1,subQ0]});Q59=makeQuery(id+"F0.imprint","IMPRINT",FACE,{"disambiguationData":[TD([[makeQuery(id+"F0.imprint","IMPRINT",EDGE,{"disambiguationData":[TD([[subQ2,-1.0]])],"derivedFrom":subQ1}),1.0]])]});}
            var Q60;
            {var subQ0=sQuery(id+"F0.wireOp",EDGE,"E32");var subQ1=sQuery(id+"F0.wireOp",EDGE,"E3");var subQ2=makeQuery(id+"F0.imprint","INTERSECT",VERTEX,{"derivedFrom":[subQ1,subQ0]});Q60=makeQuery(id+"F0.imprint","IMPRINT",FACE,{"disambiguationData":[TD([[makeQuery(id+"F0.imprint","IMPRINT",EDGE,{"disambiguationData":[TD([[subQ2,-1.0]])],"derivedFrom":subQ1}),1.0]])]});}
            var Q61;
            {var subQ0=sQuery(id+"F0.wireOp",EDGE,"E32");var subQ1=sQuery(id+"F0.wireOp",EDGE,"E6");var subQ2=makeQuery(id+"F0.imprint","INTERSECT",VERTEX,{"derivedFrom":[subQ1,subQ0]});Q61=makeQuery(id+"F0.imprint","IMPRINT",FACE,{"disambiguationData":[TD([[makeQuery(id+"F0.imprint","IMPRINT",EDGE,{"disambiguationData":[TD([[subQ2,-1.0]])],"derivedFrom":subQ1}),1.0]])]});}
            var Q62;
            {var subQ0=sQuery(id+"F0.wireOp",EDGE,"E35");var subQ1=sQuery(id+"F0.wireOp",EDGE,"E10");var subQ2=makeQuery(id+"F0.imprint","INTERSECT",VERTEX,{"derivedFrom":[subQ1,subQ0]});Q62=makeQuery(id+"F0.imprint","IMPRINT",FACE,{"disambiguationData":[TD([[makeQuery(id+"F0.imprint","IMPRINT",EDGE,{"disambiguationData":[TD([[subQ2,-1.0]])],"derivedFrom":subQ1}),1.0]])]});}
            var Q63;
            {var subQ0=sQuery(id+"F0.wireOp",EDGE,"E23");var subQ1=sQuery(id+"F0.wireOp",EDGE,"E12");var subQ2=makeQuery(id+"F0.imprint","INTERSECT",VERTEX,{"derivedFrom":[subQ1,subQ0]});Q63=makeQuery(id+"F0.imprint","IMPRINT",FACE,{"disambiguationData":[TD([[makeQuery(id+"F0.imprint","IMPRINT",EDGE,{"disambiguationData":[TD([[subQ2,-1.0]])],"derivedFrom":subQ1}),1.0]])]});}
            var Q64;
            {var subQ0=sQuery(id+"F0.wireOp",EDGE,"E32");var subQ1=sQuery(id+"F0.wireOp",EDGE,"E5");var subQ2=makeQuery(id+"F0.imprint","INTERSECT",VERTEX,{"derivedFrom":[subQ1,subQ0]});Q64=makeQuery(id+"F0.imprint","IMPRINT",FACE,{"disambiguationData":[TD([[makeQuery(id+"F0.imprint","IMPRINT",EDGE,{"disambiguationData":[TD([[subQ2,-1.0]])],"derivedFrom":subQ1}),1.0]])]});}
            var Q65;
            {var subQ0=sQuery(id+"F0.wireOp",EDGE,"E33");var subQ1=sQuery(id+"F0.wireOp",EDGE,"E6");var subQ2=makeQuery(id+"F0.imprint","INTERSECT",VERTEX,{"derivedFrom":[subQ1,subQ0]});Q65=makeQuery(id+"F0.imprint","IMPRINT",FACE,{"disambiguationData":[TD([[makeQuery(id+"F0.imprint","IMPRINT",EDGE,{"disambiguationData":[TD([[subQ2,-1.0]])],"derivedFrom":subQ1}),1.0]])]});}
            var Q66;
            {var subQ0=sQuery(id+"F0.wireOp",EDGE,"E30");var subQ1=sQuery(id+"F0.wireOp",EDGE,"E7");var subQ2=makeQuery(id+"F0.imprint","INTERSECT",VERTEX,{"derivedFrom":[subQ1,subQ0]});Q66=makeQuery(id+"F0.imprint","IMPRINT",FACE,{"disambiguationData":[TD([[makeQuery(id+"F0.imprint","IMPRINT",EDGE,{"disambiguationData":[TD([[subQ2,-1.0]])],"derivedFrom":subQ1}),1.0]])]});}
            var Q67;
            {var subQ0=sQuery(id+"F0.wireOp",EDGE,"E33");var subQ1=sQuery(id+"F0.wireOp",EDGE,"E10");var subQ2=makeQuery(id+"F0.imprint","INTERSECT",VERTEX,{"derivedFrom":[subQ1,subQ0]});Q67=makeQuery(id+"F0.imprint","IMPRINT",FACE,{"disambiguationData":[TD([[makeQuery(id+"F0.imprint","IMPRINT",EDGE,{"disambiguationData":[TD([[subQ2,-1.0]])],"derivedFrom":subQ1}),1.0]])]});}
            var Q68;
            {var subQ0=sQuery(id+"F0.wireOp",EDGE,"E30");var subQ1=sQuery(id+"F0.wireOp",EDGE,"E14");var subQ2=makeQuery(id+"F0.imprint","INTERSECT",VERTEX,{"derivedFrom":[subQ1,subQ0]});Q68=makeQuery(id+"F0.imprint","IMPRINT",FACE,{"disambiguationData":[TD([[makeQuery(id+"F0.imprint","IMPRINT",EDGE,{"disambiguationData":[TD([[subQ2,-1.0]])],"derivedFrom":subQ1}),1.0]])]});}
            var Q69;
            {var subQ0=sQuery(id+"F0.wireOp",EDGE,"E26");var subQ1=sQuery(id+"F0.wireOp",EDGE,"E13");var subQ2=makeQuery(id+"F0.imprint","INTERSECT",VERTEX,{"derivedFrom":[subQ1,subQ0]});Q69=makeQuery(id+"F0.imprint","IMPRINT",FACE,{"disambiguationData":[TD([[makeQuery(id+"F0.imprint","IMPRINT",EDGE,{"disambiguationData":[TD([[subQ2,-1.0]])],"derivedFrom":subQ1}),1.0]])]});}
            var Q70;
            {var subQ0=sQuery(id+"F0.wireOp",EDGE,"E26");var subQ1=sQuery(id+"F0.wireOp",EDGE,"E16");var subQ2=makeQuery(id+"F0.imprint","INTERSECT",VERTEX,{"derivedFrom":[subQ1,subQ0]});Q70=makeQuery(id+"F0.imprint","IMPRINT",FACE,{"disambiguationData":[TD([[makeQuery(id+"F0.imprint","IMPRINT",EDGE,{"disambiguationData":[TD([[subQ2,-1.0]])],"derivedFrom":subQ1}),1.0]])]});}
            var Q71;
            {var subQ0=sQuery(id+"F0.wireOp",EDGE,"E32");var subQ1=sQuery(id+"F0.wireOp",EDGE,"E14");var subQ2=makeQuery(id+"F0.imprint","INTERSECT",VERTEX,{"derivedFrom":[subQ1,subQ0]});Q71=makeQuery(id+"F0.imprint","IMPRINT",FACE,{"disambiguationData":[TD([[makeQuery(id+"F0.imprint","IMPRINT",EDGE,{"disambiguationData":[TD([[subQ2,-1.0]])],"derivedFrom":subQ1}),1.0]])]});}
            var Q72;
            {var subQ0=sQuery(id+"F0.wireOp",EDGE,"E24");var subQ1=sQuery(id+"F0.wireOp",EDGE,"E11");var subQ2=makeQuery(id+"F0.imprint","INTERSECT",VERTEX,{"derivedFrom":[subQ1,subQ0]});Q72=makeQuery(id+"F0.imprint","IMPRINT",FACE,{"disambiguationData":[TD([[makeQuery(id+"F0.imprint","IMPRINT",EDGE,{"disambiguationData":[TD([[subQ2,-1.0]])],"derivedFrom":subQ1}),1.0]])]});}
            var Q73;
            {var subQ0=sQuery(id+"F0.wireOp",EDGE,"E30");var subQ1=sQuery(id+"F0.wireOp",EDGE,"E3");var subQ2=makeQuery(id+"F0.imprint","INTERSECT",VERTEX,{"derivedFrom":[subQ1,subQ0]});Q73=makeQuery(id+"F0.imprint","IMPRINT",FACE,{"disambiguationData":[TD([[makeQuery(id+"F0.imprint","IMPRINT",EDGE,{"disambiguationData":[TD([[subQ2,-1.0]])],"derivedFrom":subQ1}),1.0]])]});}
            var Q74;
            {var subQ0=sQuery(id+"F0.wireOp",EDGE,"E22");var subQ1=sQuery(id+"F0.wireOp",EDGE,"E14");var subQ2=makeQuery(id+"F0.imprint","INTERSECT",VERTEX,{"derivedFrom":[subQ1,subQ0]});Q74=makeQuery(id+"F0.imprint","IMPRINT",FACE,{"disambiguationData":[TD([[makeQuery(id+"F0.imprint","IMPRINT",EDGE,{"disambiguationData":[TD([[subQ2,-1.0]])],"derivedFrom":subQ1}),1.0]])]});}
            var Q75;
            {var subQ0=sQuery(id+"F0.wireOp",EDGE,"E22");var subQ1=sQuery(id+"F0.wireOp",EDGE,"E15");var subQ2=makeQuery(id+"F0.imprint","INTERSECT",VERTEX,{"derivedFrom":[subQ1,subQ0]});Q75=makeQuery(id+"F0.imprint","IMPRINT",FACE,{"disambiguationData":[TD([[makeQuery(id+"F0.imprint","IMPRINT",EDGE,{"disambiguationData":[TD([[subQ2,-1.0]])],"derivedFrom":subQ1}),1.0]])]});}
            var Q76;
            {var subQ0=sQuery(id+"F0.wireOp",EDGE,"E29");var subQ1=sQuery(id+"F0.wireOp",EDGE,"E16");var subQ2=makeQuery(id+"F0.imprint","INTERSECT",VERTEX,{"derivedFrom":[subQ1,subQ0]});Q76=makeQuery(id+"F0.imprint","IMPRINT",FACE,{"disambiguationData":[TD([[makeQuery(id+"F0.imprint","IMPRINT",EDGE,{"disambiguationData":[TD([[subQ2,-1.0]])],"derivedFrom":subQ1}),1.0]])]});}
            var Q77;
            {var subQ0=sQuery(id+"F0.wireOp",EDGE,"E22");var subQ1=sQuery(id+"F0.wireOp",EDGE,"E17");var subQ2=makeQuery(id+"F0.imprint","INTERSECT",VERTEX,{"derivedFrom":[subQ1,subQ0]});Q77=makeQuery(id+"F0.imprint","IMPRINT",FACE,{"disambiguationData":[TD([[makeQuery(id+"F0.imprint","IMPRINT",EDGE,{"disambiguationData":[TD([[subQ2,-1.0]])],"derivedFrom":subQ1}),1.0]])]});}
            var Q78;
            {var subQ0=sQuery(id+"F0.wireOp",EDGE,"E30");var subQ1=sQuery(id+"F0.wireOp",EDGE,"E6");var subQ2=makeQuery(id+"F0.imprint","INTERSECT",VERTEX,{"derivedFrom":[subQ1,subQ0]});Q78=makeQuery(id+"F0.imprint","IMPRINT",FACE,{"disambiguationData":[TD([[makeQuery(id+"F0.imprint","IMPRINT",EDGE,{"disambiguationData":[TD([[subQ2,-1.0]])],"derivedFrom":subQ1}),1.0]])]});}
            var Q79;
            {var subQ0=sQuery(id+"F0.wireOp",EDGE,"E21");var subQ1=sQuery(id+"F0.wireOp",EDGE,"E10");var subQ2=makeQuery(id+"F0.imprint","INTERSECT",VERTEX,{"derivedFrom":[subQ1,subQ0]});Q79=makeQuery(id+"F0.imprint","IMPRINT",FACE,{"disambiguationData":[TD([[makeQuery(id+"F0.imprint","IMPRINT",EDGE,{"disambiguationData":[TD([[subQ2,-1.0]])],"derivedFrom":subQ1}),1.0]])]});}
            var Q80;
            {var subQ0=sQuery(id+"F0.wireOp",EDGE,"E23");var subQ1=sQuery(id+"F0.wireOp",EDGE,"E10");var subQ2=makeQuery(id+"F0.imprint","INTERSECT",VERTEX,{"derivedFrom":[subQ1,subQ0]});Q80=makeQuery(id+"F0.imprint","IMPRINT",FACE,{"disambiguationData":[TD([[makeQuery(id+"F0.imprint","IMPRINT",EDGE,{"disambiguationData":[TD([[subQ2,-1.0]])],"derivedFrom":subQ1}),1.0]])]});}
            var Q81;
            {var subQ0=sQuery(id+"F0.wireOp",EDGE,"E24");var subQ1=sQuery(id+"F0.wireOp",EDGE,"E6");var subQ2=makeQuery(id+"F0.imprint","INTERSECT",VERTEX,{"derivedFrom":[subQ1,subQ0]});Q81=makeQuery(id+"F0.imprint","IMPRINT",FACE,{"disambiguationData":[TD([[makeQuery(id+"F0.imprint","IMPRINT",EDGE,{"disambiguationData":[TD([[subQ2,-1.0]])],"derivedFrom":subQ1}),1.0]])]});}
            var Q82;
            {var subQ0=sQuery(id+"F0.wireOp",EDGE,"E32");var subQ1=sQuery(id+"F0.wireOp",EDGE,"E1");var subQ2=makeQuery(id+"F0.imprint","INTERSECT",VERTEX,{"derivedFrom":[subQ1,subQ0]});Q82=makeQuery(id+"F0.imprint","IMPRINT",FACE,{"disambiguationData":[TD([[makeQuery(id+"F0.imprint","IMPRINT",EDGE,{"disambiguationData":[TD([[subQ2,-1.0]])],"derivedFrom":subQ1}),1.0]])]});}
            var Q83;
            {var subQ0=sQuery(id+"F0.wireOp",EDGE,"E24");var subQ1=sQuery(id+"F0.wireOp",EDGE,"E12");var subQ2=makeQuery(id+"F0.imprint","INTERSECT",VERTEX,{"derivedFrom":[subQ1,subQ0]});Q83=makeQuery(id+"F0.imprint","IMPRINT",FACE,{"disambiguationData":[TD([[makeQuery(id+"F0.imprint","IMPRINT",EDGE,{"disambiguationData":[TD([[subQ2,-1.0]])],"derivedFrom":subQ1}),1.0]])]});}
            var Q84;
            {var subQ0=sQuery(id+"F0.wireOp",EDGE,"E25");var subQ1=sQuery(id+"F0.wireOp",EDGE,"E14");var subQ2=makeQuery(id+"F0.imprint","INTERSECT",VERTEX,{"derivedFrom":[subQ1,subQ0]});Q84=makeQuery(id+"F0.imprint","IMPRINT",FACE,{"disambiguationData":[TD([[makeQuery(id+"F0.imprint","IMPRINT",EDGE,{"disambiguationData":[TD([[subQ2,-1.0]])],"derivedFrom":subQ1}),1.0]])]});}
            var Q85;
            {var subQ0=sQuery(id+"F0.wireOp",EDGE,"E26");var subQ1=sQuery(id+"F0.wireOp",EDGE,"E6");var subQ2=makeQuery(id+"F0.imprint","INTERSECT",VERTEX,{"derivedFrom":[subQ1,subQ0]});Q85=makeQuery(id+"F0.imprint","IMPRINT",FACE,{"disambiguationData":[TD([[makeQuery(id+"F0.imprint","IMPRINT",EDGE,{"disambiguationData":[TD([[subQ2,-1.0]])],"derivedFrom":subQ1}),1.0]])]});}
            var Q86;
            {var subQ0=sQuery(id+"F0.wireOp",EDGE,"E22");var subQ1=sQuery(id+"F0.wireOp",EDGE,"E3");var subQ2=makeQuery(id+"F0.imprint","INTERSECT",VERTEX,{"derivedFrom":[subQ1,subQ0]});Q86=makeQuery(id+"F0.imprint","IMPRINT",FACE,{"disambiguationData":[TD([[makeQuery(id+"F0.imprint","IMPRINT",EDGE,{"disambiguationData":[TD([[subQ2,-1.0]])],"derivedFrom":subQ1}),1.0]])]});}
            var Q87;
            {var subQ0=sQuery(id+"F0.wireOp",EDGE,"E24");var subQ1=sQuery(id+"F0.wireOp",EDGE,"E13");var subQ2=makeQuery(id+"F0.imprint","INTERSECT",VERTEX,{"derivedFrom":[subQ1,subQ0]});Q87=makeQuery(id+"F0.imprint","IMPRINT",FACE,{"disambiguationData":[TD([[makeQuery(id+"F0.imprint","IMPRINT",EDGE,{"disambiguationData":[TD([[subQ2,-1.0]])],"derivedFrom":subQ1}),1.0]])]});}
            var Q88;
            {var subQ0=sQuery(id+"F0.wireOp",EDGE,"E31");var subQ1=sQuery(id+"F0.wireOp",EDGE,"E10");var subQ2=makeQuery(id+"F0.imprint","INTERSECT",VERTEX,{"derivedFrom":[subQ1,subQ0]});Q88=makeQuery(id+"F0.imprint","IMPRINT",FACE,{"disambiguationData":[TD([[makeQuery(id+"F0.imprint","IMPRINT",EDGE,{"disambiguationData":[TD([[subQ2,-1.0]])],"derivedFrom":subQ1}),1.0]])]});}
            var Q89;
            {var subQ0=sQuery(id+"F0.wireOp",EDGE,"E26");var subQ1=sQuery(id+"F0.wireOp",EDGE,"E8");var subQ2=makeQuery(id+"F0.imprint","INTERSECT",VERTEX,{"derivedFrom":[subQ1,subQ0]});Q89=makeQuery(id+"F0.imprint","IMPRINT",FACE,{"disambiguationData":[TD([[makeQuery(id+"F0.imprint","IMPRINT",EDGE,{"disambiguationData":[TD([[subQ2,-1.0]])],"derivedFrom":subQ1}),1.0]])]});}
            var Q90;
            {var subQ0=sQuery(id+"F0.wireOp",EDGE,"E32");var subQ1=sQuery(id+"F0.wireOp",EDGE,"E12");var subQ2=makeQuery(id+"F0.imprint","INTERSECT",VERTEX,{"derivedFrom":[subQ1,subQ0]});Q90=makeQuery(id+"F0.imprint","IMPRINT",FACE,{"disambiguationData":[TD([[makeQuery(id+"F0.imprint","IMPRINT",EDGE,{"disambiguationData":[TD([[subQ2,-1.0]])],"derivedFrom":subQ1}),1.0]])]});}
            var Q91;
            {var subQ0=sQuery(id+"F0.wireOp",EDGE,"E23");var subQ1=sQuery(id+"F0.wireOp",EDGE,"E6");var subQ2=makeQuery(id+"F0.imprint","INTERSECT",VERTEX,{"derivedFrom":[subQ1,subQ0]});Q91=makeQuery(id+"F0.imprint","IMPRINT",FACE,{"disambiguationData":[TD([[makeQuery(id+"F0.imprint","IMPRINT",EDGE,{"disambiguationData":[TD([[subQ2,-1.0]])],"derivedFrom":subQ1}),1.0]])]});}
            var Q92;
            {var subQ0=sQuery(id+"F0.wireOp",EDGE,"E32");var subQ1=sQuery(id+"F0.wireOp",EDGE,"E8");var subQ2=makeQuery(id+"F0.imprint","INTERSECT",VERTEX,{"derivedFrom":[subQ1,subQ0]});Q92=makeQuery(id+"F0.imprint","IMPRINT",FACE,{"disambiguationData":[TD([[makeQuery(id+"F0.imprint","IMPRINT",EDGE,{"disambiguationData":[TD([[subQ2,-1.0]])],"derivedFrom":subQ1}),1.0]])]});}
            var Q93;
            {var subQ0=sQuery(id+"F0.wireOp",EDGE,"E27");var subQ1=sQuery(id+"F0.wireOp",EDGE,"E14");var subQ2=makeQuery(id+"F0.imprint","INTERSECT",VERTEX,{"derivedFrom":[subQ1,subQ0]});Q93=makeQuery(id+"F0.imprint","IMPRINT",FACE,{"disambiguationData":[TD([[makeQuery(id+"F0.imprint","IMPRINT",EDGE,{"disambiguationData":[TD([[subQ2,-1.0]])],"derivedFrom":subQ1}),1.0]])]});}
            var Q94;
            {var subQ0=sQuery(id+"F0.wireOp",EDGE,"E22");var subQ1=sQuery(id+"F0.wireOp",EDGE,"E1");var subQ2=makeQuery(id+"F0.imprint","INTERSECT",VERTEX,{"derivedFrom":[subQ1,subQ0]});Q94=makeQuery(id+"F0.imprint","IMPRINT",FACE,{"disambiguationData":[TD([[makeQuery(id+"F0.imprint","IMPRINT",EDGE,{"disambiguationData":[TD([[subQ2,-1.0]])],"derivedFrom":subQ1}),1.0]])]});}
            var Q95;
            {var subQ0=sQuery(id+"F0.wireOp",EDGE,"E26");var subQ1=sQuery(id+"F0.wireOp",EDGE,"E17");var subQ2=makeQuery(id+"F0.imprint","INTERSECT",VERTEX,{"derivedFrom":[subQ1,subQ0]});Q95=makeQuery(id+"F0.imprint","IMPRINT",FACE,{"disambiguationData":[TD([[makeQuery(id+"F0.imprint","IMPRINT",EDGE,{"disambiguationData":[TD([[subQ2,-1.0]])],"derivedFrom":subQ1}),1.0]])]});}
            var Q96;
            {var subQ0=sQuery(id+"F0.wireOp",EDGE,"E32");var subQ1=sQuery(id+"F0.wireOp",EDGE,"E15");var subQ2=makeQuery(id+"F0.imprint","INTERSECT",VERTEX,{"derivedFrom":[subQ1,subQ0]});Q96=makeQuery(id+"F0.imprint","IMPRINT",FACE,{"disambiguationData":[TD([[makeQuery(id+"F0.imprint","IMPRINT",EDGE,{"disambiguationData":[TD([[subQ2,-1.0]])],"derivedFrom":subQ1}),1.0]])]});}
            var Q97;
            {var subQ0=sQuery(id+"F0.wireOp",EDGE,"E23");var subQ1=sQuery(id+"F0.wireOp",EDGE,"E8");var subQ2=makeQuery(id+"F0.imprint","INTERSECT",VERTEX,{"derivedFrom":[subQ1,subQ0]});Q97=makeQuery(id+"F0.imprint","IMPRINT",FACE,{"disambiguationData":[TD([[makeQuery(id+"F0.imprint","IMPRINT",EDGE,{"disambiguationData":[TD([[subQ2,-1.0]])],"derivedFrom":subQ1}),1.0]])]});}
            var Q98;
            {var subQ0=sQuery(id+"F0.wireOp",EDGE,"E25");var subQ1=sQuery(id+"F0.wireOp",EDGE,"E12");var subQ2=makeQuery(id+"F0.imprint","INTERSECT",VERTEX,{"derivedFrom":[subQ1,subQ0]});Q98=makeQuery(id+"F0.imprint","IMPRINT",FACE,{"disambiguationData":[TD([[makeQuery(id+"F0.imprint","IMPRINT",EDGE,{"disambiguationData":[TD([[subQ2,-1.0]])],"derivedFrom":subQ1}),1.0]])]});}
            var Q99;
            {var subQ0=sQuery(id+"F0.wireOp",EDGE,"E26");var subQ1=sQuery(id+"F0.wireOp",EDGE,"E7");var subQ2=makeQuery(id+"F0.imprint","INTERSECT",VERTEX,{"derivedFrom":[subQ1,subQ0]});Q99=makeQuery(id+"F0.imprint","IMPRINT",FACE,{"disambiguationData":[TD([[makeQuery(id+"F0.imprint","IMPRINT",EDGE,{"disambiguationData":[TD([[subQ2,-1.0]])],"derivedFrom":subQ1}),1.0]])]});}
            var Q100;
            {var subQ0=sQuery(id+"F0.wireOp",EDGE,"E22");var subQ1=sQuery(id+"F0.wireOp",EDGE,"E6");var subQ2=makeQuery(id+"F0.imprint","INTERSECT",VERTEX,{"derivedFrom":[subQ1,subQ0]});Q100=makeQuery(id+"F0.imprint","IMPRINT",FACE,{"disambiguationData":[TD([[makeQuery(id+"F0.imprint","IMPRINT",EDGE,{"disambiguationData":[TD([[subQ2,-1.0]])],"derivedFrom":subQ1}),1.0]])]});}
            var Q101;
            {var subQ0=sQuery(id+"F0.wireOp",EDGE,"E33");var subQ1=sQuery(id+"F0.wireOp",EDGE,"E2");var subQ2=makeQuery(id+"F0.imprint","INTERSECT",VERTEX,{"derivedFrom":[subQ1,subQ0]});Q101=makeQuery(id+"F0.imprint","IMPRINT",FACE,{"disambiguationData":[TD([[makeQuery(id+"F0.imprint","IMPRINT",EDGE,{"disambiguationData":[TD([[subQ2,-1.0]])],"derivedFrom":subQ1}),1.0]])]});}
            var Q102;
            {var subQ0=sQuery(id+"F0.wireOp",EDGE,"E21");var subQ1=sQuery(id+"F0.wireOp",EDGE,"E8");var subQ2=makeQuery(id+"F0.imprint","INTERSECT",VERTEX,{"derivedFrom":[subQ1,subQ0]});Q102=makeQuery(id+"F0.imprint","IMPRINT",FACE,{"disambiguationData":[TD([[makeQuery(id+"F0.imprint","IMPRINT",EDGE,{"disambiguationData":[TD([[subQ2,-1.0]])],"derivedFrom":subQ1}),1.0]])]});}
            var Q103;
            {var subQ0=sQuery(id+"F0.wireOp",EDGE,"E22");var subQ1=sQuery(id+"F0.wireOp",EDGE,"E11");var subQ2=makeQuery(id+"F0.imprint","INTERSECT",VERTEX,{"derivedFrom":[subQ1,subQ0]});Q103=makeQuery(id+"F0.imprint","IMPRINT",FACE,{"disambiguationData":[TD([[makeQuery(id+"F0.imprint","IMPRINT",EDGE,{"disambiguationData":[TD([[subQ2,-1.0]])],"derivedFrom":subQ1}),1.0]])]});}
            var Q104;
            {var subQ0=sQuery(id+"F0.wireOp",EDGE,"E32");var subQ1=sQuery(id+"F0.wireOp",EDGE,"E13");var subQ2=makeQuery(id+"F0.imprint","INTERSECT",VERTEX,{"derivedFrom":[subQ1,subQ0]});Q104=makeQuery(id+"F0.imprint","IMPRINT",FACE,{"disambiguationData":[TD([[makeQuery(id+"F0.imprint","IMPRINT",EDGE,{"disambiguationData":[TD([[subQ2,-1.0]])],"derivedFrom":subQ1}),1.0]])]});}
            var Q105;
            {var subQ0=sQuery(id+"F0.wireOp",EDGE,"E21");var subQ1=sQuery(id+"F0.wireOp",EDGE,"E14");var subQ2=makeQuery(id+"F0.imprint","INTERSECT",VERTEX,{"derivedFrom":[subQ1,subQ0]});Q105=makeQuery(id+"F0.imprint","IMPRINT",FACE,{"disambiguationData":[TD([[makeQuery(id+"F0.imprint","IMPRINT",EDGE,{"disambiguationData":[TD([[subQ2,-1.0]])],"derivedFrom":subQ1}),1.0]])]});}
            var Q106;
            {var subQ0=sQuery(id+"F0.wireOp",EDGE,"E29");var subQ1=sQuery(id+"F0.wireOp",EDGE,"E6");var subQ2=makeQuery(id+"F0.imprint","INTERSECT",VERTEX,{"derivedFrom":[subQ1,subQ0]});Q106=makeQuery(id+"F0.imprint","IMPRINT",FACE,{"disambiguationData":[TD([[makeQuery(id+"F0.imprint","IMPRINT",EDGE,{"disambiguationData":[TD([[subQ2,-1.0]])],"derivedFrom":subQ1}),1.0]])]});}
            var Q107;
            {var subQ0=sQuery(id+"F0.wireOp",EDGE,"E30");var subQ1=sQuery(id+"F0.wireOp",EDGE,"E1");var subQ2=makeQuery(id+"F0.imprint","INTERSECT",VERTEX,{"derivedFrom":[subQ1,subQ0]});Q107=makeQuery(id+"F0.imprint","IMPRINT",FACE,{"disambiguationData":[TD([[makeQuery(id+"F0.imprint","IMPRINT",EDGE,{"disambiguationData":[TD([[subQ2,-1.0]])],"derivedFrom":subQ1}),1.0]])]});}
            var Q108;
            {var subQ0=sQuery(id+"F0.wireOp",EDGE,"E35");var subQ1=sQuery(id+"F0.wireOp",EDGE,"E6");var subQ2=makeQuery(id+"F0.imprint","INTERSECT",VERTEX,{"derivedFrom":[subQ1,subQ0]});Q108=makeQuery(id+"F0.imprint","IMPRINT",FACE,{"disambiguationData":[TD([[makeQuery(id+"F0.imprint","IMPRINT",EDGE,{"disambiguationData":[TD([[subQ2,-1.0]])],"derivedFrom":subQ1}),1.0]])]});}
            var Q109;
            {var subQ0=sQuery(id+"F0.wireOp",EDGE,"E19");var subQ1=sQuery(id+"F0.wireOp",EDGE,"E6");var subQ2=makeQuery(id+"F0.imprint","INTERSECT",VERTEX,{"derivedFrom":[subQ1,subQ0]});Q109=makeQuery(id+"F0.imprint","IMPRINT",FACE,{"disambiguationData":[TD([[makeQuery(id+"F0.imprint","IMPRINT",EDGE,{"disambiguationData":[TD([[subQ2,-1.0]])],"derivedFrom":subQ1}),1.0]])]});}
            var Q110;
            {var subQ0=sQuery(id+"F0.wireOp",EDGE,"E30");var subQ1=sQuery(id+"F0.wireOp",EDGE,"E8");var subQ2=makeQuery(id+"F0.imprint","INTERSECT",VERTEX,{"derivedFrom":[subQ1,subQ0]});Q110=makeQuery(id+"F0.imprint","IMPRINT",FACE,{"disambiguationData":[TD([[makeQuery(id+"F0.imprint","IMPRINT",EDGE,{"disambiguationData":[TD([[subQ2,-1.0]])],"derivedFrom":subQ1}),1.0]])]});}
            var Q111;
            {var subQ0=sQuery(id+"F0.wireOp",EDGE,"E30");var subQ1=sQuery(id+"F0.wireOp",EDGE,"E2");var subQ2=makeQuery(id+"F0.imprint","INTERSECT",VERTEX,{"derivedFrom":[subQ1,subQ0]});Q111=makeQuery(id+"F0.imprint","IMPRINT",FACE,{"disambiguationData":[TD([[makeQuery(id+"F0.imprint","IMPRINT",EDGE,{"disambiguationData":[TD([[subQ2,-1.0]])],"derivedFrom":subQ1}),1.0]])]});}
            var Q112;
            {var subQ0=sQuery(id+"F0.wireOp",EDGE,"E21");var subQ1=sQuery(id+"F0.wireOp",EDGE,"E2");var subQ2=makeQuery(id+"F0.imprint","INTERSECT",VERTEX,{"derivedFrom":[subQ1,subQ0]});Q112=makeQuery(id+"F0.imprint","IMPRINT",FACE,{"disambiguationData":[TD([[makeQuery(id+"F0.imprint","IMPRINT",EDGE,{"disambiguationData":[TD([[subQ2,-1.0]])],"derivedFrom":subQ1}),1.0]])]});}
            var Q113;
            {var subQ0=sQuery(id+"F0.wireOp",EDGE,"E27");var subQ1=sQuery(id+"F0.wireOp",EDGE,"E6");var subQ2=makeQuery(id+"F0.imprint","INTERSECT",VERTEX,{"derivedFrom":[subQ1,subQ0]});Q113=makeQuery(id+"F0.imprint","IMPRINT",FACE,{"disambiguationData":[TD([[makeQuery(id+"F0.imprint","IMPRINT",EDGE,{"disambiguationData":[TD([[subQ2,-1.0]])],"derivedFrom":subQ1}),1.0]])]});}
            var Q114;
            {var subQ0=sQuery(id+"F0.wireOp",EDGE,"E19");var subQ1=sQuery(id+"F0.wireOp",EDGE,"E8");var subQ2=makeQuery(id+"F0.imprint","INTERSECT",VERTEX,{"derivedFrom":[subQ1,subQ0]});Q114=makeQuery(id+"F0.imprint","IMPRINT",FACE,{"disambiguationData":[TD([[makeQuery(id+"F0.imprint","IMPRINT",EDGE,{"disambiguationData":[TD([[subQ2,-1.0]])],"derivedFrom":subQ1}),1.0]])]});}
            var Q115;
            {var subQ0=sQuery(id+"F0.wireOp",EDGE,"E30");var subQ1=sQuery(id+"F0.wireOp",EDGE,"E16");var subQ2=makeQuery(id+"F0.imprint","INTERSECT",VERTEX,{"derivedFrom":[subQ1,subQ0]});Q115=makeQuery(id+"F0.imprint","IMPRINT",FACE,{"disambiguationData":[TD([[makeQuery(id+"F0.imprint","IMPRINT",EDGE,{"disambiguationData":[TD([[subQ2,-1.0]])],"derivedFrom":subQ1}),1.0]])]});}
            var Q116;
            {var subQ0=sQuery(id+"F0.wireOp",EDGE,"E24");var subQ1=sQuery(id+"F0.wireOp",EDGE,"E16");var subQ2=makeQuery(id+"F0.imprint","INTERSECT",VERTEX,{"derivedFrom":[subQ1,subQ0]});Q116=makeQuery(id+"F0.imprint","IMPRINT",FACE,{"disambiguationData":[TD([[makeQuery(id+"F0.imprint","IMPRINT",EDGE,{"disambiguationData":[TD([[subQ2,-1.0]])],"derivedFrom":subQ1}),1.0]])]});}
            var Q117;
            {var subQ0=sQuery(id+"F0.wireOp",EDGE,"E19");var subQ1=sQuery(id+"F0.wireOp",EDGE,"E12");var subQ2=makeQuery(id+"F0.imprint","INTERSECT",VERTEX,{"derivedFrom":[subQ1,subQ0]});Q117=makeQuery(id+"F0.imprint","IMPRINT",FACE,{"disambiguationData":[TD([[makeQuery(id+"F0.imprint","IMPRINT",EDGE,{"disambiguationData":[TD([[subQ2,-1.0]])],"derivedFrom":subQ1}),1.0]])]});}
            var Q118;
            {var subQ0=sQuery(id+"F0.wireOp",EDGE,"E22");var subQ1=sQuery(id+"F0.wireOp",EDGE,"E2");var subQ2=makeQuery(id+"F0.imprint","INTERSECT",VERTEX,{"derivedFrom":[subQ1,subQ0]});Q118=makeQuery(id+"F0.imprint","IMPRINT",FACE,{"disambiguationData":[TD([[makeQuery(id+"F0.imprint","IMPRINT",EDGE,{"disambiguationData":[TD([[subQ2,-1.0]])],"derivedFrom":subQ1}),1.0]])]});}
            var Q119;
            {var subQ0=sQuery(id+"F0.wireOp",EDGE,"E27");var subQ1=sQuery(id+"F0.wireOp",EDGE,"E8");var subQ2=makeQuery(id+"F0.imprint","INTERSECT",VERTEX,{"derivedFrom":[subQ1,subQ0]});Q119=makeQuery(id+"F0.imprint","IMPRINT",FACE,{"disambiguationData":[TD([[makeQuery(id+"F0.imprint","IMPRINT",EDGE,{"disambiguationData":[TD([[subQ2,-1.0]])],"derivedFrom":subQ1}),1.0]])]});}
            var Q120;
            {var subQ0=sQuery(id+"F0.wireOp",EDGE,"E22");var subQ1=sQuery(id+"F0.wireOp",EDGE,"E7");var subQ2=makeQuery(id+"F0.imprint","INTERSECT",VERTEX,{"derivedFrom":[subQ1,subQ0]});Q120=makeQuery(id+"F0.imprint","IMPRINT",FACE,{"disambiguationData":[TD([[makeQuery(id+"F0.imprint","IMPRINT",EDGE,{"disambiguationData":[TD([[subQ2,-1.0]])],"derivedFrom":subQ1}),1.0]])]});}
            var Q121;
            {var subQ0=sQuery(id+"F0.wireOp",EDGE,"E26");var subQ1=sQuery(id+"F0.wireOp",EDGE,"E10");var subQ2=makeQuery(id+"F0.imprint","INTERSECT",VERTEX,{"derivedFrom":[subQ1,subQ0]});Q121=makeQuery(id+"F0.imprint","IMPRINT",FACE,{"disambiguationData":[TD([[makeQuery(id+"F0.imprint","IMPRINT",EDGE,{"disambiguationData":[TD([[subQ2,-1.0]])],"derivedFrom":subQ1}),1.0]])]});}
            var Q122;
            {var subQ0=sQuery(id+"F0.wireOp",EDGE,"E25");var subQ1=sQuery(id+"F0.wireOp",EDGE,"E10");var subQ2=makeQuery(id+"F0.imprint","INTERSECT",VERTEX,{"derivedFrom":[subQ1,subQ0]});Q122=makeQuery(id+"F0.imprint","IMPRINT",FACE,{"disambiguationData":[TD([[makeQuery(id+"F0.imprint","IMPRINT",EDGE,{"disambiguationData":[TD([[subQ2,-1.0]])],"derivedFrom":subQ1}),1.0]])]});}
            var Q123;
            {var subQ0=sQuery(id+"F0.wireOp",EDGE,"E21");var subQ1=sQuery(id+"F0.wireOp",EDGE,"E6");var subQ2=makeQuery(id+"F0.imprint","INTERSECT",VERTEX,{"derivedFrom":[subQ1,subQ0]});Q123=makeQuery(id+"F0.imprint","IMPRINT",FACE,{"disambiguationData":[TD([[makeQuery(id+"F0.imprint","IMPRINT",EDGE,{"disambiguationData":[TD([[subQ2,-1.0]])],"derivedFrom":subQ1}),1.0]])]});}
            var Q124;
            {var subQ0=sQuery(id+"F0.wireOp",EDGE,"E29");var subQ1=sQuery(id+"F0.wireOp",EDGE,"E2");var subQ2=makeQuery(id+"F0.imprint","INTERSECT",VERTEX,{"derivedFrom":[subQ1,subQ0]});Q124=makeQuery(id+"F0.imprint","IMPRINT",FACE,{"disambiguationData":[TD([[makeQuery(id+"F0.imprint","IMPRINT",EDGE,{"disambiguationData":[TD([[subQ2,-1.0]])],"derivedFrom":subQ1}),1.0]])]});}
            var Q125;
            {var subQ0=sQuery(id+"F0.wireOp",EDGE,"E27");var subQ1=sQuery(id+"F0.wireOp",EDGE,"E12");var subQ2=makeQuery(id+"F0.imprint","INTERSECT",VERTEX,{"derivedFrom":[subQ1,subQ0]});Q125=makeQuery(id+"F0.imprint","IMPRINT",FACE,{"disambiguationData":[TD([[makeQuery(id+"F0.imprint","IMPRINT",EDGE,{"disambiguationData":[TD([[subQ2,-1.0]])],"derivedFrom":subQ1}),1.0]])]});}
            var Q126;
            {var subQ0=sQuery(id+"F0.wireOp",EDGE,"E32");var subQ1=sQuery(id+"F0.wireOp",EDGE,"E2");var subQ2=makeQuery(id+"F0.imprint","INTERSECT",VERTEX,{"derivedFrom":[subQ1,subQ0]});Q126=makeQuery(id+"F0.imprint","IMPRINT",FACE,{"disambiguationData":[TD([[makeQuery(id+"F0.imprint","IMPRINT",EDGE,{"disambiguationData":[TD([[subQ2,-1.0]])],"derivedFrom":subQ1}),1.0]])]});}
            var Q127;
            {var subQ0=sQuery(id+"F0.wireOp",EDGE,"E22");var subQ1=sQuery(id+"F0.wireOp",EDGE,"E12");var subQ2=makeQuery(id+"F0.imprint","INTERSECT",VERTEX,{"derivedFrom":[subQ1,subQ0]});Q127=makeQuery(id+"F0.imprint","IMPRINT",FACE,{"disambiguationData":[TD([[makeQuery(id+"F0.imprint","IMPRINT",EDGE,{"disambiguationData":[TD([[subQ2,-1.0]])],"derivedFrom":subQ1}),1.0]])]});}
            var Q128;
            {var subQ0=sQuery(id+"F0.wireOp",EDGE,"E23");var subQ1=sQuery(id+"F0.wireOp",EDGE,"E2");var subQ2=makeQuery(id+"F0.imprint","INTERSECT",VERTEX,{"derivedFrom":[subQ1,subQ0]});Q128=makeQuery(id+"F0.imprint","IMPRINT",FACE,{"disambiguationData":[TD([[makeQuery(id+"F0.imprint","IMPRINT",EDGE,{"disambiguationData":[TD([[subQ2,-1.0]])],"derivedFrom":subQ1}),1.0]])]});}
            var Q129;
            {var subQ0=sQuery(id+"F0.wireOp",EDGE,"E22");var subQ1=sQuery(id+"F0.wireOp",EDGE,"E10");var subQ2=makeQuery(id+"F0.imprint","INTERSECT",VERTEX,{"derivedFrom":[subQ1,subQ0]});Q129=makeQuery(id+"F0.imprint","IMPRINT",FACE,{"disambiguationData":[TD([[makeQuery(id+"F0.imprint","IMPRINT",EDGE,{"disambiguationData":[TD([[subQ2,-1.0]])],"derivedFrom":subQ1}),1.0]])]});}
            var Q130;
            {var subQ0=sQuery(id+"F0.wireOp",EDGE,"E26");var subQ1=sQuery(id+"F0.wireOp",EDGE,"E15");var subQ2=makeQuery(id+"F0.imprint","INTERSECT",VERTEX,{"derivedFrom":[subQ1,subQ0]});Q130=makeQuery(id+"F0.imprint","IMPRINT",FACE,{"disambiguationData":[TD([[makeQuery(id+"F0.imprint","IMPRINT",EDGE,{"disambiguationData":[TD([[subQ2,-1.0]])],"derivedFrom":subQ1}),1.0]])]});}
            var Q131;
            {var subQ0=sQuery(id+"F0.wireOp",EDGE,"E24");var subQ1=sQuery(id+"F0.wireOp",EDGE,"E14");var subQ2=makeQuery(id+"F0.imprint","INTERSECT",VERTEX,{"derivedFrom":[subQ1,subQ0]});Q131=makeQuery(id+"F0.imprint","IMPRINT",FACE,{"disambiguationData":[TD([[makeQuery(id+"F0.imprint","IMPRINT",EDGE,{"disambiguationData":[TD([[subQ2,-1.0]])],"derivedFrom":subQ1}),1.0]])]});}
            var Q132;
            {var subQ0=sQuery(id+"F0.wireOp",EDGE,"E24");var subQ1=sQuery(id+"F0.wireOp",EDGE,"E9");var subQ2=makeQuery(id+"F0.imprint","INTERSECT",VERTEX,{"derivedFrom":[subQ1,subQ0]});Q132=makeQuery(id+"F0.imprint","IMPRINT",FACE,{"disambiguationData":[TD([[makeQuery(id+"F0.imprint","IMPRINT",EDGE,{"disambiguationData":[TD([[subQ2,-1.0]])],"derivedFrom":subQ1}),1.0]])]});}
            var Q133;
            {var subQ0=sQuery(id+"F0.wireOp",EDGE,"E21");var subQ1=sQuery(id+"F0.wireOp",EDGE,"E12");var subQ2=makeQuery(id+"F0.imprint","INTERSECT",VERTEX,{"derivedFrom":[subQ1,subQ0]});Q133=makeQuery(id+"F0.imprint","IMPRINT",FACE,{"disambiguationData":[TD([[makeQuery(id+"F0.imprint","IMPRINT",EDGE,{"disambiguationData":[TD([[subQ2,-1.0]])],"derivedFrom":subQ1}),1.0]])]});}
            var Q134;
            {var subQ0=sQuery(id+"F0.wireOp",EDGE,"E22");var subQ1=sQuery(id+"F0.wireOp",EDGE,"E5");var subQ2=makeQuery(id+"F0.imprint","INTERSECT",VERTEX,{"derivedFrom":[subQ1,subQ0]});Q134=makeQuery(id+"F0.imprint","IMPRINT",FACE,{"disambiguationData":[TD([[makeQuery(id+"F0.imprint","IMPRINT",EDGE,{"disambiguationData":[TD([[subQ2,-1.0]])],"derivedFrom":subQ1}),1.0]])]});}
            var Q135;
            {var subQ0=sQuery(id+"F0.wireOp",EDGE,"E24");var subQ1=sQuery(id+"F0.wireOp",EDGE,"E15");var subQ2=makeQuery(id+"F0.imprint","INTERSECT",VERTEX,{"derivedFrom":[subQ1,subQ0]});Q135=makeQuery(id+"F0.imprint","IMPRINT",FACE,{"disambiguationData":[TD([[makeQuery(id+"F0.imprint","IMPRINT",EDGE,{"disambiguationData":[TD([[subQ2,-1.0]])],"derivedFrom":subQ1}),1.0]])]});}
            var Q136;
            {var subQ0=sQuery(id+"F0.wireOp",EDGE,"E29");var subQ1=sQuery(id+"F0.wireOp",EDGE,"E14");var subQ2=makeQuery(id+"F0.imprint","INTERSECT",VERTEX,{"derivedFrom":[subQ1,subQ0]});Q136=makeQuery(id+"F0.imprint","IMPRINT",FACE,{"disambiguationData":[TD([[makeQuery(id+"F0.imprint","IMPRINT",EDGE,{"disambiguationData":[TD([[subQ2,-1.0]])],"derivedFrom":subQ1}),1.0]])]});}
            var Q137;
            {var subQ0=sQuery(id+"F0.wireOp",EDGE,"E31");var subQ1=sQuery(id+"F0.wireOp",EDGE,"E16");var subQ2=makeQuery(id+"F0.imprint","INTERSECT",VERTEX,{"derivedFrom":[subQ1,subQ0]});Q137=makeQuery(id+"F0.imprint","IMPRINT",FACE,{"disambiguationData":[TD([[makeQuery(id+"F0.imprint","IMPRINT",EDGE,{"disambiguationData":[TD([[subQ2,-1.0]])],"derivedFrom":subQ1}),1.0]])]});}
            var Q138;
            {var subQ0=sQuery(id+"F0.wireOp",EDGE,"E34");var subQ1=sQuery(id+"F0.wireOp",EDGE,"E15");var subQ2=makeQuery(id+"F0.imprint","INTERSECT",VERTEX,{"derivedFrom":[subQ1,subQ0]});Q138=makeQuery(id+"F0.imprint","IMPRINT",FACE,{"disambiguationData":[TD([[makeQuery(id+"F0.imprint","IMPRINT",EDGE,{"disambiguationData":[TD([[subQ2,-1.0]])],"derivedFrom":subQ1}),1.0]])]});}
            var Q139;
            {var subQ0=sQuery(id+"F0.wireOp",EDGE,"E20");var subQ1=sQuery(id+"F0.wireOp",EDGE,"E6");var subQ2=makeQuery(id+"F0.imprint","INTERSECT",VERTEX,{"derivedFrom":[subQ1,subQ0]});Q139=makeQuery(id+"F0.imprint","IMPRINT",FACE,{"disambiguationData":[TD([[makeQuery(id+"F0.imprint","IMPRINT",EDGE,{"disambiguationData":[TD([[subQ2,-1.0]])],"derivedFrom":subQ1}),1.0]])]});}
            var Q140;
            {var subQ0=sQuery(id+"F0.wireOp",EDGE,"E22");var subQ1=sQuery(id+"F0.wireOp",EDGE,"E0.right");var subQ2=makeQuery(id+"F0.imprint","INTERSECT",VERTEX,{"derivedFrom":[subQ1,subQ0]});Q140=makeQuery(id+"F0.imprint","IMPRINT",FACE,{"disambiguationData":[TD([[makeQuery(id+"F0.imprint","IMPRINT",EDGE,{"disambiguationData":[TD([[subQ2,-1.0]])],"derivedFrom":subQ1}),-1.0]])]});}
            var Q141;
            {var subQ0=sQuery(id+"F0.wireOp",EDGE,"E7");var subQ1=sQuery(id+"F0.wireOp",EDGE,"E0.bottom");var subQ2=makeQuery(id+"F0.imprint","INTERSECT",VERTEX,{"derivedFrom":[subQ1,subQ0]});Q141=makeQuery(id+"F0.imprint","IMPRINT",FACE,{"disambiguationData":[TD([[makeQuery(id+"F0.imprint","IMPRINT",EDGE,{"disambiguationData":[TD([[subQ2,-1.0]])],"derivedFrom":subQ1}),-1.0]])]});}
            var Q142;
            {var subQ0=sQuery(id+"F0.wireOp",EDGE,"E20");var subQ1=sQuery(id+"F0.wireOp",EDGE,"E15");var subQ2=makeQuery(id+"F0.imprint","INTERSECT",VERTEX,{"derivedFrom":[subQ1,subQ0]});Q142=makeQuery(id+"F0.imprint","IMPRINT",FACE,{"disambiguationData":[TD([[makeQuery(id+"F0.imprint","IMPRINT",EDGE,{"disambiguationData":[TD([[subQ2,-1.0]])],"derivedFrom":subQ1}),1.0]])]});}
            var Q143;
            {var subQ0=sQuery(id+"F0.wireOp",EDGE,"E30");var subQ1=sQuery(id+"F0.wireOp",EDGE,"E0.left");var subQ2=makeQuery(id+"F0.imprint","INTERSECT",VERTEX,{"derivedFrom":[subQ1,subQ0]});Q143=makeQuery(id+"F0.imprint","IMPRINT",FACE,{"disambiguationData":[TD([[makeQuery(id+"F0.imprint","IMPRINT",EDGE,{"disambiguationData":[TD([[subQ2,-1.0]])],"derivedFrom":subQ1}),1.0]])]});}
            var Q144;
            {var subQ0=sQuery(id+"F0.wireOp",EDGE,"E20");var subQ1=sQuery(id+"F0.wireOp",EDGE,"E1");var subQ2=makeQuery(id+"F0.imprint","INTERSECT",VERTEX,{"derivedFrom":[subQ1,subQ0]});Q144=makeQuery(id+"F0.imprint","IMPRINT",FACE,{"disambiguationData":[TD([[makeQuery(id+"F0.imprint","IMPRINT",EDGE,{"disambiguationData":[TD([[subQ2,-1.0]])],"derivedFrom":subQ1}),1.0]])]});}
            var Q145;
            {var subQ0=sQuery(id+"F0.wireOp",EDGE,"E28");var subQ1=sQuery(id+"F0.wireOp",EDGE,"E12");var subQ2=makeQuery(id+"F0.imprint","INTERSECT",VERTEX,{"derivedFrom":[subQ1,subQ0]});Q145=makeQuery(id+"F0.imprint","IMPRINT",FACE,{"disambiguationData":[TD([[makeQuery(id+"F0.imprint","IMPRINT",EDGE,{"disambiguationData":[TD([[subQ2,-1.0]])],"derivedFrom":subQ1}),1.0]])]});}
            var Q146;
            {var subQ0=sQuery(id+"F0.wireOp",EDGE,"E35");var subQ1=sQuery(id+"F0.wireOp",EDGE,"E0.left");var subQ2=makeQuery(id+"F0.imprint","INTERSECT",VERTEX,{"derivedFrom":[subQ1,subQ0]});Q146=makeQuery(id+"F0.imprint","IMPRINT",FACE,{"disambiguationData":[TD([[makeQuery(id+"F0.imprint","IMPRINT",EDGE,{"disambiguationData":[TD([[subQ2,-1.0]])],"derivedFrom":subQ1}),1.0]])]});}
            var Q147;
            {var subQ0=sQuery(id+"F0.wireOp",EDGE,"E34");var subQ1=sQuery(id+"F0.wireOp",EDGE,"E17");var subQ2=makeQuery(id+"F0.imprint","INTERSECT",VERTEX,{"derivedFrom":[subQ1,subQ0]});Q147=makeQuery(id+"F0.imprint","IMPRINT",FACE,{"disambiguationData":[TD([[makeQuery(id+"F0.imprint","IMPRINT",EDGE,{"disambiguationData":[TD([[subQ2,-1.0]])],"derivedFrom":subQ1}),1.0]])]});}
            var Q148;
            {var subQ0=sQuery(id+"F0.wireOp",EDGE,"E28");var subQ1=sQuery(id+"F0.wireOp",EDGE,"E11");var subQ2=makeQuery(id+"F0.imprint","INTERSECT",VERTEX,{"derivedFrom":[subQ1,subQ0]});Q148=makeQuery(id+"F0.imprint","IMPRINT",FACE,{"disambiguationData":[TD([[makeQuery(id+"F0.imprint","IMPRINT",EDGE,{"disambiguationData":[TD([[subQ2,-1.0]])],"derivedFrom":subQ1}),1.0]])]});}
            var Q149;
            {var subQ0=sQuery(id+"F0.wireOp",EDGE,"E35");var subQ1=sQuery(id+"F0.wireOp",EDGE,"E0.right");var subQ2=makeQuery(id+"F0.imprint","INTERSECT",VERTEX,{"derivedFrom":[subQ1,subQ0]});Q149=makeQuery(id+"F0.imprint","IMPRINT",FACE,{"disambiguationData":[TD([[makeQuery(id+"F0.imprint","IMPRINT",EDGE,{"disambiguationData":[TD([[subQ2,-1.0]])],"derivedFrom":subQ1}),-1.0]])]});}
            var Q150;
            {var subQ0=sQuery(id+"F0.wireOp",EDGE,"E28");var subQ1=sQuery(id+"F0.wireOp",EDGE,"E10");var subQ2=makeQuery(id+"F0.imprint","INTERSECT",VERTEX,{"derivedFrom":[subQ1,subQ0]});Q150=makeQuery(id+"F0.imprint","IMPRINT",FACE,{"disambiguationData":[TD([[makeQuery(id+"F0.imprint","IMPRINT",EDGE,{"disambiguationData":[TD([[subQ2,-1.0]])],"derivedFrom":subQ1}),1.0]])]});}
            var Q151;
            {var subQ0=sQuery(id+"F0.wireOp",EDGE,"E17");var subQ1=sQuery(id+"F0.wireOp",EDGE,"E0.bottom");var subQ2=makeQuery(id+"F0.imprint","INTERSECT",VERTEX,{"derivedFrom":[subQ1,subQ0]});Q151=makeQuery(id+"F0.imprint","IMPRINT",FACE,{"disambiguationData":[TD([[makeQuery(id+"F0.imprint","IMPRINT",EDGE,{"disambiguationData":[TD([[subQ2,-1.0]])],"derivedFrom":subQ1}),-1.0]])]});}
            var Q152;
            {var subQ0=sQuery(id+"F0.wireOp",EDGE,"E13");var subQ1=sQuery(id+"F0.wireOp",EDGE,"E0.bottom");var subQ2=makeQuery(id+"F0.imprint","INTERSECT",VERTEX,{"derivedFrom":[subQ1,subQ0]});Q152=makeQuery(id+"F0.imprint","IMPRINT",FACE,{"disambiguationData":[TD([[makeQuery(id+"F0.imprint","IMPRINT",EDGE,{"disambiguationData":[TD([[subQ2,-1.0]])],"derivedFrom":subQ1}),-1.0]])]});}
            var Q153;
            {var subQ0=sQuery(id+"F0.wireOp",EDGE,"E20");var subQ1=sQuery(id+"F0.wireOp",EDGE,"E5");var subQ2=makeQuery(id+"F0.imprint","INTERSECT",VERTEX,{"derivedFrom":[subQ1,subQ0]});Q153=makeQuery(id+"F0.imprint","IMPRINT",FACE,{"disambiguationData":[TD([[makeQuery(id+"F0.imprint","IMPRINT",EDGE,{"disambiguationData":[TD([[subQ2,-1.0]])],"derivedFrom":subQ1}),1.0]])]});}
            var Q154;
            {var subQ0=sQuery(id+"F0.wireOp",EDGE,"E20");var subQ1=sQuery(id+"F0.wireOp",EDGE,"E16");var subQ2=makeQuery(id+"F0.imprint","INTERSECT",VERTEX,{"derivedFrom":[subQ1,subQ0]});Q154=makeQuery(id+"F0.imprint","IMPRINT",FACE,{"disambiguationData":[TD([[makeQuery(id+"F0.imprint","IMPRINT",EDGE,{"disambiguationData":[TD([[subQ2,-1.0]])],"derivedFrom":subQ1}),1.0]])]});}
            var Q155;
            {var subQ0=sQuery(id+"F0.wireOp",EDGE,"E16");var subQ1=sQuery(id+"F0.wireOp",EDGE,"E0.bottom");var subQ2=makeQuery(id+"F0.imprint","INTERSECT",VERTEX,{"derivedFrom":[subQ1,subQ0]});Q155=makeQuery(id+"F0.imprint","IMPRINT",FACE,{"disambiguationData":[TD([[makeQuery(id+"F0.imprint","IMPRINT",EDGE,{"disambiguationData":[TD([[subQ2,-1.0]])],"derivedFrom":subQ1}),-1.0]])]});}
            var Q156;
            {var subQ0=sQuery(id+"F0.wireOp",EDGE,"E33");var subQ1=sQuery(id+"F0.wireOp",EDGE,"E0.right");var subQ2=makeQuery(id+"F0.imprint","INTERSECT",VERTEX,{"derivedFrom":[subQ1,subQ0]});Q156=makeQuery(id+"F0.imprint","IMPRINT",FACE,{"disambiguationData":[TD([[makeQuery(id+"F0.imprint","IMPRINT",EDGE,{"disambiguationData":[TD([[subQ2,-1.0]])],"derivedFrom":subQ1}),-1.0]])]});}
            var Q157;
            {var subQ0=sQuery(id+"F0.wireOp",EDGE,"E28");var subQ1=sQuery(id+"F0.wireOp",EDGE,"E3");var subQ2=makeQuery(id+"F0.imprint","INTERSECT",VERTEX,{"derivedFrom":[subQ1,subQ0]});Q157=makeQuery(id+"F0.imprint","IMPRINT",FACE,{"disambiguationData":[TD([[makeQuery(id+"F0.imprint","IMPRINT",EDGE,{"disambiguationData":[TD([[subQ2,-1.0]])],"derivedFrom":subQ1}),1.0]])]});}
            var Q158;
            {var subQ0=sQuery(id+"F0.wireOp",EDGE,"E28");var subQ1=sQuery(id+"F0.wireOp",EDGE,"E6");var subQ2=makeQuery(id+"F0.imprint","INTERSECT",VERTEX,{"derivedFrom":[subQ1,subQ0]});Q158=makeQuery(id+"F0.imprint","IMPRINT",FACE,{"disambiguationData":[TD([[makeQuery(id+"F0.imprint","IMPRINT",EDGE,{"disambiguationData":[TD([[subQ2,-1.0]])],"derivedFrom":subQ1}),1.0]])]});}
            var Q159;
            {var subQ0=sQuery(id+"F0.wireOp",EDGE,"E28");var subQ1=sQuery(id+"F0.wireOp",EDGE,"E1");var subQ2=makeQuery(id+"F0.imprint","INTERSECT",VERTEX,{"derivedFrom":[subQ1,subQ0]});Q159=makeQuery(id+"F0.imprint","IMPRINT",FACE,{"disambiguationData":[TD([[makeQuery(id+"F0.imprint","IMPRINT",EDGE,{"disambiguationData":[TD([[subQ2,-1.0]])],"derivedFrom":subQ1}),1.0]])]});}
            var Q160;
            {var subQ0=sQuery(id+"F0.wireOp",EDGE,"E20");var subQ1=sQuery(id+"F0.wireOp",EDGE,"E10");var subQ2=makeQuery(id+"F0.imprint","INTERSECT",VERTEX,{"derivedFrom":[subQ1,subQ0]});Q160=makeQuery(id+"F0.imprint","IMPRINT",FACE,{"disambiguationData":[TD([[makeQuery(id+"F0.imprint","IMPRINT",EDGE,{"disambiguationData":[TD([[subQ2,-1.0]])],"derivedFrom":subQ1}),1.0]])]});}
            var Q161;
            {var subQ0=sQuery(id+"F0.wireOp",EDGE,"E20");var subQ1=sQuery(id+"F0.wireOp",EDGE,"E14");var subQ2=makeQuery(id+"F0.imprint","INTERSECT",VERTEX,{"derivedFrom":[subQ1,subQ0]});Q161=makeQuery(id+"F0.imprint","IMPRINT",FACE,{"disambiguationData":[TD([[makeQuery(id+"F0.imprint","IMPRINT",EDGE,{"disambiguationData":[TD([[subQ2,-1.0]])],"derivedFrom":subQ1}),1.0]])]});}
            var Q162;
            {var subQ0=sQuery(id+"F0.wireOp",EDGE,"E4");var subQ1=sQuery(id+"F0.wireOp",EDGE,"E0.bottom");var subQ2=makeQuery(id+"F0.imprint","INTERSECT",VERTEX,{"derivedFrom":[subQ1,subQ0]});Q162=makeQuery(id+"F0.imprint","IMPRINT",FACE,{"disambiguationData":[TD([[makeQuery(id+"F0.imprint","IMPRINT",EDGE,{"disambiguationData":[TD([[subQ2,-1.0]])],"derivedFrom":subQ1}),-1.0]])]});}
            var Q163;
            {var subQ0=sQuery(id+"F0.wireOp",EDGE,"E14");var subQ1=sQuery(id+"F0.wireOp",EDGE,"E0.bottom");var subQ2=makeQuery(id+"F0.imprint","INTERSECT",VERTEX,{"derivedFrom":[subQ1,subQ0]});Q163=makeQuery(id+"F0.imprint","IMPRINT",FACE,{"disambiguationData":[TD([[makeQuery(id+"F0.imprint","IMPRINT",EDGE,{"disambiguationData":[TD([[subQ2,-1.0]])],"derivedFrom":subQ1}),-1.0]])]});}
            var Q164;
            {var subQ0=sQuery(id+"F0.wireOp",EDGE,"E7");var subQ1=sQuery(id+"F0.wireOp",EDGE,"E0.top");var subQ2=makeQuery(id+"F0.imprint","INTERSECT",VERTEX,{"derivedFrom":[subQ1,subQ0]});Q164=makeQuery(id+"F0.imprint","IMPRINT",FACE,{"disambiguationData":[TD([[makeQuery(id+"F0.imprint","IMPRINT",EDGE,{"disambiguationData":[TD([[subQ2,-1.0]])],"derivedFrom":subQ1}),1.0]])]});}
            var Q165;
            {var subQ0=sQuery(id+"F0.wireOp",EDGE,"E30");var subQ1=sQuery(id+"F0.wireOp",EDGE,"E4");var subQ2=makeQuery(id+"F0.imprint","INTERSECT",VERTEX,{"derivedFrom":[subQ1,subQ0]});Q165=makeQuery(id+"F0.imprint","IMPRINT",FACE,{"disambiguationData":[TD([[makeQuery(id+"F0.imprint","IMPRINT",EDGE,{"disambiguationData":[TD([[subQ2,-1.0]])],"derivedFrom":subQ1}),1.0]])]});}
            var Q166;
            {var subQ0=sQuery(id+"F0.wireOp",EDGE,"E23");var subQ1=sQuery(id+"F0.wireOp",EDGE,"E0.right");var subQ2=makeQuery(id+"F0.imprint","INTERSECT",VERTEX,{"derivedFrom":[subQ1,subQ0]});Q166=makeQuery(id+"F0.imprint","IMPRINT",FACE,{"disambiguationData":[TD([[makeQuery(id+"F0.imprint","IMPRINT",EDGE,{"disambiguationData":[TD([[subQ2,-1.0]])],"derivedFrom":subQ1}),-1.0]])]});}
            var Q167;
            {var subQ0=sQuery(id+"F0.wireOp",EDGE,"E34");var subQ1=sQuery(id+"F0.wireOp",EDGE,"E16");var subQ2=makeQuery(id+"F0.imprint","INTERSECT",VERTEX,{"derivedFrom":[subQ1,subQ0]});Q167=makeQuery(id+"F0.imprint","IMPRINT",FACE,{"disambiguationData":[TD([[makeQuery(id+"F0.imprint","IMPRINT",EDGE,{"disambiguationData":[TD([[subQ2,-1.0]])],"derivedFrom":subQ1}),1.0]])]});}
            var Q168;
            {var subQ0=sQuery(id+"F0.wireOp",EDGE,"E32");var subQ1=sQuery(id+"F0.wireOp",EDGE,"E0.left");var subQ2=makeQuery(id+"F0.imprint","INTERSECT",VERTEX,{"derivedFrom":[subQ1,subQ0]});Q168=makeQuery(id+"F0.imprint","IMPRINT",FACE,{"disambiguationData":[TD([[makeQuery(id+"F0.imprint","IMPRINT",EDGE,{"disambiguationData":[TD([[subQ2,-1.0]])],"derivedFrom":subQ1}),1.0]])]});}
            var Q169;
            {var subQ0=sQuery(id+"F0.wireOp",EDGE,"E34");var subQ1=sQuery(id+"F0.wireOp",EDGE,"E7");var subQ2=makeQuery(id+"F0.imprint","INTERSECT",VERTEX,{"derivedFrom":[subQ1,subQ0]});Q169=makeQuery(id+"F0.imprint","IMPRINT",FACE,{"disambiguationData":[TD([[makeQuery(id+"F0.imprint","IMPRINT",EDGE,{"disambiguationData":[TD([[subQ2,-1.0]])],"derivedFrom":subQ1}),1.0]])]});}
            var Q170;
            {var subQ0=sQuery(id+"F0.wireOp",EDGE,"E22");var subQ1=sQuery(id+"F0.wireOp",EDGE,"E4");var subQ2=makeQuery(id+"F0.imprint","INTERSECT",VERTEX,{"derivedFrom":[subQ1,subQ0]});Q170=makeQuery(id+"F0.imprint","IMPRINT",FACE,{"disambiguationData":[TD([[makeQuery(id+"F0.imprint","IMPRINT",EDGE,{"disambiguationData":[TD([[subQ2,-1.0]])],"derivedFrom":subQ1}),1.0]])]});}
            var Q171;
            {var subQ0=sQuery(id+"F0.wireOp",EDGE,"E14");var subQ1=sQuery(id+"F0.wireOp",EDGE,"E0.top");var subQ2=makeQuery(id+"F0.imprint","INTERSECT",VERTEX,{"derivedFrom":[subQ1,subQ0]});Q171=makeQuery(id+"F0.imprint","IMPRINT",FACE,{"disambiguationData":[TD([[makeQuery(id+"F0.imprint","IMPRINT",EDGE,{"disambiguationData":[TD([[subQ2,-1.0]])],"derivedFrom":subQ1}),1.0]])]});}
            var Q172;
            {var subQ0=sQuery(id+"F0.wireOp",EDGE,"E34");var subQ1=sQuery(id+"F0.wireOp",EDGE,"E1");var subQ2=makeQuery(id+"F0.imprint","INTERSECT",VERTEX,{"derivedFrom":[subQ1,subQ0]});Q172=makeQuery(id+"F0.imprint","IMPRINT",FACE,{"disambiguationData":[TD([[makeQuery(id+"F0.imprint","IMPRINT",EDGE,{"disambiguationData":[TD([[subQ2,-1.0]])],"derivedFrom":subQ1}),1.0]])]});}
            var Q173;
            {var subQ0=sQuery(id+"F0.wireOp",EDGE,"E21");var subQ1=sQuery(id+"F0.wireOp",EDGE,"E0.right");var subQ2=makeQuery(id+"F0.imprint","INTERSECT",VERTEX,{"derivedFrom":[subQ1,subQ0]});Q173=makeQuery(id+"F0.imprint","IMPRINT",FACE,{"disambiguationData":[TD([[makeQuery(id+"F0.imprint","IMPRINT",EDGE,{"disambiguationData":[TD([[subQ2,-1.0]])],"derivedFrom":subQ1}),-1.0]])]});}
            var Q174;
            {var subQ0=sQuery(id+"F0.wireOp",EDGE,"E16");var subQ1=sQuery(id+"F0.wireOp",EDGE,"E0.top");var subQ2=makeQuery(id+"F0.imprint","INTERSECT",VERTEX,{"derivedFrom":[subQ1,subQ0]});Q174=makeQuery(id+"F0.imprint","IMPRINT",FACE,{"disambiguationData":[TD([[makeQuery(id+"F0.imprint","IMPRINT",EDGE,{"disambiguationData":[TD([[subQ2,-1.0]])],"derivedFrom":subQ1}),1.0]])]});}
            var Q175;
            {var subQ0=sQuery(id+"F0.wireOp",EDGE,"E31");var subQ1=sQuery(id+"F0.wireOp",EDGE,"E4");var subQ2=makeQuery(id+"F0.imprint","INTERSECT",VERTEX,{"derivedFrom":[subQ1,subQ0]});Q175=makeQuery(id+"F0.imprint","IMPRINT",FACE,{"disambiguationData":[TD([[makeQuery(id+"F0.imprint","IMPRINT",EDGE,{"disambiguationData":[TD([[subQ2,-1.0]])],"derivedFrom":subQ1}),1.0]])]});}
            var Q176;
            {var subQ0=sQuery(id+"F0.wireOp",EDGE,"E32");var subQ1=sQuery(id+"F0.wireOp",EDGE,"E4");var subQ2=makeQuery(id+"F0.imprint","INTERSECT",VERTEX,{"derivedFrom":[subQ1,subQ0]});Q176=makeQuery(id+"F0.imprint","IMPRINT",FACE,{"disambiguationData":[TD([[makeQuery(id+"F0.imprint","IMPRINT",EDGE,{"disambiguationData":[TD([[subQ2,-1.0]])],"derivedFrom":subQ1}),1.0]])]});}
            var Q177;
            {var subQ0=sQuery(id+"F0.wireOp",EDGE,"E33");var subQ1=sQuery(id+"F0.wireOp",EDGE,"E0.left");var subQ2=makeQuery(id+"F0.imprint","INTERSECT",VERTEX,{"derivedFrom":[subQ1,subQ0]});Q177=makeQuery(id+"F0.imprint","IMPRINT",FACE,{"disambiguationData":[TD([[makeQuery(id+"F0.imprint","IMPRINT",EDGE,{"disambiguationData":[TD([[subQ2,-1.0]])],"derivedFrom":subQ1}),1.0]])]});}
            var Q178;
            {var subQ0=sQuery(id+"F0.wireOp",EDGE,"E20");var subQ1=sQuery(id+"F0.wireOp",EDGE,"E3");var subQ2=makeQuery(id+"F0.imprint","INTERSECT",VERTEX,{"derivedFrom":[subQ1,subQ0]});Q178=makeQuery(id+"F0.imprint","IMPRINT",FACE,{"disambiguationData":[TD([[makeQuery(id+"F0.imprint","IMPRINT",EDGE,{"disambiguationData":[TD([[subQ2,-1.0]])],"derivedFrom":subQ1}),1.0]])]});}
            var Q179;
            {var subQ0=sQuery(id+"F0.wireOp",EDGE,"E20");var subQ1=sQuery(id+"F0.wireOp",EDGE,"E17");var subQ2=makeQuery(id+"F0.imprint","INTERSECT",VERTEX,{"derivedFrom":[subQ1,subQ0]});Q179=makeQuery(id+"F0.imprint","IMPRINT",FACE,{"disambiguationData":[TD([[makeQuery(id+"F0.imprint","IMPRINT",EDGE,{"disambiguationData":[TD([[subQ2,-1.0]])],"derivedFrom":subQ1}),1.0]])]});}
            var Q180;
            {var subQ0=sQuery(id+"F0.wireOp",EDGE,"E28");var subQ1=sQuery(id+"F0.wireOp",EDGE,"E13");var subQ2=makeQuery(id+"F0.imprint","INTERSECT",VERTEX,{"derivedFrom":[subQ1,subQ0]});Q180=makeQuery(id+"F0.imprint","IMPRINT",FACE,{"disambiguationData":[TD([[makeQuery(id+"F0.imprint","IMPRINT",EDGE,{"disambiguationData":[TD([[subQ2,-1.0]])],"derivedFrom":subQ1}),1.0]])]});}
            var Q181;
            {var subQ0=sQuery(id+"F0.wireOp",EDGE,"E35");var subQ1=sQuery(id+"F0.wireOp",EDGE,"E4");var subQ2=makeQuery(id+"F0.imprint","INTERSECT",VERTEX,{"derivedFrom":[subQ1,subQ0]});Q181=makeQuery(id+"F0.imprint","IMPRINT",FACE,{"disambiguationData":[TD([[makeQuery(id+"F0.imprint","IMPRINT",EDGE,{"disambiguationData":[TD([[subQ2,-1.0]])],"derivedFrom":subQ1}),1.0]])]});}
            var Q182;
            {var subQ0=sQuery(id+"F0.wireOp",EDGE,"E34");var subQ1=sQuery(id+"F0.wireOp",EDGE,"E11");var subQ2=makeQuery(id+"F0.imprint","INTERSECT",VERTEX,{"derivedFrom":[subQ1,subQ0]});Q182=makeQuery(id+"F0.imprint","IMPRINT",FACE,{"disambiguationData":[TD([[makeQuery(id+"F0.imprint","IMPRINT",EDGE,{"disambiguationData":[TD([[subQ2,-1.0]])],"derivedFrom":subQ1}),1.0]])]});}
            var Q183;
            {var subQ0=sQuery(id+"F0.wireOp",EDGE,"E11");var subQ1=sQuery(id+"F0.wireOp",EDGE,"E0.bottom");var subQ2=makeQuery(id+"F0.imprint","INTERSECT",VERTEX,{"derivedFrom":[subQ1,subQ0]});Q183=makeQuery(id+"F0.imprint","IMPRINT",FACE,{"disambiguationData":[TD([[makeQuery(id+"F0.imprint","IMPRINT",EDGE,{"disambiguationData":[TD([[subQ2,-1.0]])],"derivedFrom":subQ1}),-1.0]])]});}
            var Q184;
            {var subQ0=sQuery(id+"F0.wireOp",EDGE,"E23");var subQ1=sQuery(id+"F0.wireOp",EDGE,"E0.left");var subQ2=makeQuery(id+"F0.imprint","INTERSECT",VERTEX,{"derivedFrom":[subQ1,subQ0]});Q184=makeQuery(id+"F0.imprint","IMPRINT",FACE,{"disambiguationData":[TD([[makeQuery(id+"F0.imprint","IMPRINT",EDGE,{"disambiguationData":[TD([[subQ2,-1.0]])],"derivedFrom":subQ1}),1.0]])]});}
            var Q185;
            {var subQ0=sQuery(id+"F0.wireOp",EDGE,"E26");var subQ1=sQuery(id+"F0.wireOp",EDGE,"E0.left");var subQ2=makeQuery(id+"F0.imprint","INTERSECT",VERTEX,{"derivedFrom":[subQ1,subQ0]});Q185=makeQuery(id+"F0.imprint","IMPRINT",FACE,{"disambiguationData":[TD([[makeQuery(id+"F0.imprint","IMPRINT",EDGE,{"disambiguationData":[TD([[subQ2,-1.0]])],"derivedFrom":subQ1}),1.0]])]});}
            var Q186;
            {var subQ0=sQuery(id+"F0.wireOp",EDGE,"E24");var subQ1=sQuery(id+"F0.wireOp",EDGE,"E0.left");var subQ2=makeQuery(id+"F0.imprint","INTERSECT",VERTEX,{"derivedFrom":[subQ1,subQ0]});Q186=makeQuery(id+"F0.imprint","IMPRINT",FACE,{"disambiguationData":[TD([[makeQuery(id+"F0.imprint","IMPRINT",EDGE,{"disambiguationData":[TD([[subQ2,-1.0]])],"derivedFrom":subQ1}),1.0]])]});}
            var Q187;
            {var subQ0=sQuery(id+"F0.wireOp",EDGE,"E31");var subQ1=sQuery(id+"F0.wireOp",EDGE,"E0.left");var subQ2=makeQuery(id+"F0.imprint","INTERSECT",VERTEX,{"derivedFrom":[subQ1,subQ0]});Q187=makeQuery(id+"F0.imprint","IMPRINT",FACE,{"disambiguationData":[TD([[makeQuery(id+"F0.imprint","IMPRINT",EDGE,{"disambiguationData":[TD([[subQ2,-1.0]])],"derivedFrom":subQ1}),1.0]])]});}
            var Q188;
            {var subQ0=sQuery(id+"F0.wireOp",EDGE,"E20");var subQ1=sQuery(id+"F0.wireOp",EDGE,"E0.right");var subQ2=makeQuery(id+"F0.imprint","INTERSECT",VERTEX,{"derivedFrom":[subQ1,subQ0]});Q188=makeQuery(id+"F0.imprint","IMPRINT",FACE,{"disambiguationData":[TD([[makeQuery(id+"F0.imprint","IMPRINT",EDGE,{"disambiguationData":[TD([[subQ2,-1.0]])],"derivedFrom":subQ1}),-1.0]])]});}
            var Q189;
            {var subQ0=sQuery(id+"F0.wireOp",EDGE,"E8");var subQ1=sQuery(id+"F0.wireOp",EDGE,"E0.bottom");var subQ2=makeQuery(id+"F0.imprint","INTERSECT",VERTEX,{"derivedFrom":[subQ1,subQ0]});Q189=makeQuery(id+"F0.imprint","IMPRINT",FACE,{"disambiguationData":[TD([[makeQuery(id+"F0.imprint","IMPRINT",EDGE,{"disambiguationData":[TD([[subQ2,-1.0]])],"derivedFrom":subQ1}),-1.0]])]});}
            var Q190;
            {var subQ0=sQuery(id+"F0.wireOp",EDGE,"E30");var subQ1=sQuery(id+"F0.wireOp",EDGE,"E0.right");var subQ2=makeQuery(id+"F0.imprint","INTERSECT",VERTEX,{"derivedFrom":[subQ1,subQ0]});Q190=makeQuery(id+"F0.imprint","IMPRINT",FACE,{"disambiguationData":[TD([[makeQuery(id+"F0.imprint","IMPRINT",EDGE,{"disambiguationData":[TD([[subQ2,-1.0]])],"derivedFrom":subQ1}),-1.0]])]});}
            var Q191;
            {var subQ0=sQuery(id+"F0.wireOp",EDGE,"E20");var subQ1=sQuery(id+"F0.wireOp",EDGE,"E9");var subQ2=makeQuery(id+"F0.imprint","INTERSECT",VERTEX,{"derivedFrom":[subQ1,subQ0]});Q191=makeQuery(id+"F0.imprint","IMPRINT",FACE,{"disambiguationData":[TD([[makeQuery(id+"F0.imprint","IMPRINT",EDGE,{"disambiguationData":[TD([[subQ2,-1.0]])],"derivedFrom":subQ1}),1.0]])]});}
            var Q192;
            {var subQ0=sQuery(id+"F0.wireOp",EDGE,"E20");var subQ1=sQuery(id+"F0.wireOp",EDGE,"E4");var subQ2=makeQuery(id+"F0.imprint","INTERSECT",VERTEX,{"derivedFrom":[subQ1,subQ0]});Q192=makeQuery(id+"F0.imprint","IMPRINT",FACE,{"disambiguationData":[TD([[makeQuery(id+"F0.imprint","IMPRINT",EDGE,{"disambiguationData":[TD([[subQ2,-1.0]])],"derivedFrom":subQ1}),1.0]])]});}
            var Q193;
            {var subQ0=sQuery(id+"F0.wireOp",EDGE,"E19");var subQ1=sQuery(id+"F0.wireOp",EDGE,"E0.left");var subQ2=makeQuery(id+"F0.imprint","INTERSECT",VERTEX,{"derivedFrom":[subQ1,subQ0]});Q193=makeQuery(id+"F0.imprint","IMPRINT",FACE,{"disambiguationData":[TD([[makeQuery(id+"F0.imprint","IMPRINT",EDGE,{"disambiguationData":[TD([[subQ2,-1.0]])],"derivedFrom":subQ1}),1.0]])]});}
            var Q194;
            {var subQ0=sQuery(id+"F0.wireOp",EDGE,"E22");var subQ1=sQuery(id+"F0.wireOp",EDGE,"E0.left");var subQ2=makeQuery(id+"F0.imprint","INTERSECT",VERTEX,{"derivedFrom":[subQ1,subQ0]});Q194=makeQuery(id+"F0.imprint","IMPRINT",FACE,{"disambiguationData":[TD([[makeQuery(id+"F0.imprint","IMPRINT",EDGE,{"disambiguationData":[TD([[subQ2,-1.0]])],"derivedFrom":subQ1}),1.0]])]});}
            var Q195;
            {var subQ0=sQuery(id+"F0.wireOp",EDGE,"E34");var subQ1=sQuery(id+"F0.wireOp",EDGE,"E0.left");var subQ2=makeQuery(id+"F0.imprint","INTERSECT",VERTEX,{"derivedFrom":[subQ1,subQ0]});Q195=makeQuery(id+"F0.imprint","IMPRINT",FACE,{"disambiguationData":[TD([[makeQuery(id+"F0.imprint","IMPRINT",EDGE,{"disambiguationData":[TD([[subQ2,-1.0]])],"derivedFrom":subQ1}),1.0]])]});}
            var Q196;
            {var subQ0=sQuery(id+"F0.wireOp",EDGE,"E34");var subQ1=sQuery(id+"F0.wireOp",EDGE,"E10");var subQ2=makeQuery(id+"F0.imprint","INTERSECT",VERTEX,{"derivedFrom":[subQ1,subQ0]});Q196=makeQuery(id+"F0.imprint","IMPRINT",FACE,{"disambiguationData":[TD([[makeQuery(id+"F0.imprint","IMPRINT",EDGE,{"disambiguationData":[TD([[subQ2,-1.0]])],"derivedFrom":subQ1}),1.0]])]});}
            var Q197;
            {var subQ0=sQuery(id+"F0.wireOp",EDGE,"E20");var subQ1=sQuery(id+"F0.wireOp",EDGE,"E8");var subQ2=makeQuery(id+"F0.imprint","INTERSECT",VERTEX,{"derivedFrom":[subQ1,subQ0]});Q197=makeQuery(id+"F0.imprint","IMPRINT",FACE,{"disambiguationData":[TD([[makeQuery(id+"F0.imprint","IMPRINT",EDGE,{"disambiguationData":[TD([[subQ2,-1.0]])],"derivedFrom":subQ1}),1.0]])]});}
            var Q198;
            {var subQ0=sQuery(id+"F0.wireOp",EDGE,"E25");var subQ1=sQuery(id+"F0.wireOp",EDGE,"E0.left");var subQ2=makeQuery(id+"F0.imprint","INTERSECT",VERTEX,{"derivedFrom":[subQ1,subQ0]});Q198=makeQuery(id+"F0.imprint","IMPRINT",FACE,{"disambiguationData":[TD([[makeQuery(id+"F0.imprint","IMPRINT",EDGE,{"disambiguationData":[TD([[subQ2,-1.0]])],"derivedFrom":subQ1}),1.0]])]});}
            var Q199;
            {var subQ0=sQuery(id+"F0.wireOp",EDGE,"E26");var subQ1=sQuery(id+"F0.wireOp",EDGE,"E0.right");var subQ2=makeQuery(id+"F0.imprint","INTERSECT",VERTEX,{"derivedFrom":[subQ1,subQ0]});Q199=makeQuery(id+"F0.imprint","IMPRINT",FACE,{"disambiguationData":[TD([[makeQuery(id+"F0.imprint","IMPRINT",EDGE,{"disambiguationData":[TD([[subQ2,-1.0]])],"derivedFrom":subQ1}),-1.0]])]});}
            var Q200;
            {var subQ0=sQuery(id+"F0.wireOp",EDGE,"E20");var subQ1=sQuery(id+"F0.wireOp",EDGE,"E11");var subQ2=makeQuery(id+"F0.imprint","INTERSECT",VERTEX,{"derivedFrom":[subQ1,subQ0]});Q200=makeQuery(id+"F0.imprint","IMPRINT",FACE,{"disambiguationData":[TD([[makeQuery(id+"F0.imprint","IMPRINT",EDGE,{"disambiguationData":[TD([[subQ2,-1.0]])],"derivedFrom":subQ1}),1.0]])]});}
            var Q201;
            {var subQ0=sQuery(id+"F0.wireOp",EDGE,"E34");var subQ1=sQuery(id+"F0.wireOp",EDGE,"E12");var subQ2=makeQuery(id+"F0.imprint","INTERSECT",VERTEX,{"derivedFrom":[subQ1,subQ0]});Q201=makeQuery(id+"F0.imprint","IMPRINT",FACE,{"disambiguationData":[TD([[makeQuery(id+"F0.imprint","IMPRINT",EDGE,{"disambiguationData":[TD([[subQ2,-1.0]])],"derivedFrom":subQ1}),1.0]])]});}
            var Q202;
            {var subQ0=sQuery(id+"F0.wireOp",EDGE,"E1");var subQ1=sQuery(id+"F0.wireOp",EDGE,"E0.top");var subQ2=makeQuery(id+"F0.imprint","INTERSECT",VERTEX,{"derivedFrom":[subQ1,subQ0]});Q202=makeQuery(id+"F0.imprint","IMPRINT",FACE,{"disambiguationData":[TD([[makeQuery(id+"F0.imprint","IMPRINT",EDGE,{"disambiguationData":[TD([[subQ2,-1.0]])],"derivedFrom":subQ1}),1.0]])]});}
            var Q203;
            {var subQ0=sQuery(id+"F0.wireOp",EDGE,"E8");var subQ1=sQuery(id+"F0.wireOp",EDGE,"E0.top");var subQ2=makeQuery(id+"F0.imprint","INTERSECT",VERTEX,{"derivedFrom":[subQ1,subQ0]});Q203=makeQuery(id+"F0.imprint","IMPRINT",FACE,{"disambiguationData":[TD([[makeQuery(id+"F0.imprint","IMPRINT",EDGE,{"disambiguationData":[TD([[subQ2,-1.0]])],"derivedFrom":subQ1}),1.0]])]});}
            var Q204;
            {var subQ0=sQuery(id+"F0.wireOp",EDGE,"E34");var subQ1=sQuery(id+"F0.wireOp",EDGE,"E8");var subQ2=makeQuery(id+"F0.imprint","INTERSECT",VERTEX,{"derivedFrom":[subQ1,subQ0]});Q204=makeQuery(id+"F0.imprint","IMPRINT",FACE,{"disambiguationData":[TD([[makeQuery(id+"F0.imprint","IMPRINT",EDGE,{"disambiguationData":[TD([[subQ2,-1.0]])],"derivedFrom":subQ1}),1.0]])]});}
            var Q205;
            {var subQ0=sQuery(id+"F0.wireOp",EDGE,"E29");var subQ1=sQuery(id+"F0.wireOp",EDGE,"E0.right");var subQ2=makeQuery(id+"F0.imprint","INTERSECT",VERTEX,{"derivedFrom":[subQ1,subQ0]});Q205=makeQuery(id+"F0.imprint","IMPRINT",FACE,{"disambiguationData":[TD([[makeQuery(id+"F0.imprint","IMPRINT",EDGE,{"disambiguationData":[TD([[subQ2,-1.0]])],"derivedFrom":subQ1}),-1.0]])]});}
            var Q206;
            {var subQ0=sQuery(id+"F0.wireOp",EDGE,"E28");var subQ1=sQuery(id+"F0.wireOp",EDGE,"E17");var subQ2=makeQuery(id+"F0.imprint","INTERSECT",VERTEX,{"derivedFrom":[subQ1,subQ0]});Q206=makeQuery(id+"F0.imprint","IMPRINT",FACE,{"disambiguationData":[TD([[makeQuery(id+"F0.imprint","IMPRINT",EDGE,{"disambiguationData":[TD([[subQ2,-1.0]])],"derivedFrom":subQ1}),1.0]])]});}
            var Q207;
            {var subQ0=sQuery(id+"F0.wireOp",EDGE,"E34");var subQ1=sQuery(id+"F0.wireOp",EDGE,"E2");var subQ2=makeQuery(id+"F0.imprint","INTERSECT",VERTEX,{"derivedFrom":[subQ1,subQ0]});Q207=makeQuery(id+"F0.imprint","IMPRINT",FACE,{"disambiguationData":[TD([[makeQuery(id+"F0.imprint","IMPRINT",EDGE,{"disambiguationData":[TD([[subQ2,-1.0]])],"derivedFrom":subQ1}),1.0]])]});}
            var Q208;
            {var subQ0=sQuery(id+"F0.wireOp",EDGE,"E15");var subQ1=sQuery(id+"F0.wireOp",EDGE,"E0.bottom");var subQ2=makeQuery(id+"F0.imprint","INTERSECT",VERTEX,{"derivedFrom":[subQ1,subQ0]});Q208=makeQuery(id+"F0.imprint","IMPRINT",FACE,{"disambiguationData":[TD([[makeQuery(id+"F0.imprint","IMPRINT",EDGE,{"disambiguationData":[TD([[subQ2,-1.0]])],"derivedFrom":subQ1}),-1.0]])]});}
            var Q209;
            {var subQ0=sQuery(id+"F0.wireOp",EDGE,"E28");var subQ1=sQuery(id+"F0.wireOp",EDGE,"E9");var subQ2=makeQuery(id+"F0.imprint","INTERSECT",VERTEX,{"derivedFrom":[subQ1,subQ0]});Q209=makeQuery(id+"F0.imprint","IMPRINT",FACE,{"disambiguationData":[TD([[makeQuery(id+"F0.imprint","IMPRINT",EDGE,{"disambiguationData":[TD([[subQ2,-1.0]])],"derivedFrom":subQ1}),1.0]])]});}
            var Q210;
            {var subQ0=sQuery(id+"F0.wireOp",EDGE,"E5");var subQ1=sQuery(id+"F0.wireOp",EDGE,"E0.bottom");var subQ2=makeQuery(id+"F0.imprint","INTERSECT",VERTEX,{"derivedFrom":[subQ1,subQ0]});Q210=makeQuery(id+"F0.imprint","IMPRINT",FACE,{"disambiguationData":[TD([[makeQuery(id+"F0.imprint","IMPRINT",EDGE,{"disambiguationData":[TD([[subQ2,-1.0]])],"derivedFrom":subQ1}),-1.0]])]});}
            var Q211;
            {var subQ0=sQuery(id+"F0.wireOp",EDGE,"E2");var subQ1=sQuery(id+"F0.wireOp",EDGE,"E0.bottom");var subQ2=makeQuery(id+"F0.imprint","INTERSECT",VERTEX,{"derivedFrom":[subQ1,subQ0]});Q211=makeQuery(id+"F0.imprint","IMPRINT",FACE,{"disambiguationData":[TD([[makeQuery(id+"F0.imprint","IMPRINT",EDGE,{"disambiguationData":[TD([[subQ2,-1.0]])],"derivedFrom":subQ1}),-1.0]])]});}
            var Q212;
            {var subQ0=sQuery(id+"F0.wireOp",EDGE,"E34");var subQ1=sQuery(id+"F0.wireOp",EDGE,"E14");var subQ2=makeQuery(id+"F0.imprint","INTERSECT",VERTEX,{"derivedFrom":[subQ1,subQ0]});Q212=makeQuery(id+"F0.imprint","IMPRINT",FACE,{"disambiguationData":[TD([[makeQuery(id+"F0.imprint","IMPRINT",EDGE,{"disambiguationData":[TD([[subQ2,-1.0]])],"derivedFrom":subQ1}),1.0]])]});}
            var Q213;
            {var subQ0=sQuery(id+"F0.wireOp",EDGE,"E3");var subQ1=sQuery(id+"F0.wireOp",EDGE,"E0.bottom");var subQ2=makeQuery(id+"F0.imprint","INTERSECT",VERTEX,{"derivedFrom":[subQ1,subQ0]});Q213=makeQuery(id+"F0.imprint","IMPRINT",FACE,{"disambiguationData":[TD([[makeQuery(id+"F0.imprint","IMPRINT",EDGE,{"disambiguationData":[TD([[subQ2,-1.0]])],"derivedFrom":subQ1}),-1.0]])]});}
            var Q214;
            {var subQ0=sQuery(id+"F0.wireOp",EDGE,"E28");var subQ1=sQuery(id+"F0.wireOp",EDGE,"E7");var subQ2=makeQuery(id+"F0.imprint","INTERSECT",VERTEX,{"derivedFrom":[subQ1,subQ0]});Q214=makeQuery(id+"F0.imprint","IMPRINT",FACE,{"disambiguationData":[TD([[makeQuery(id+"F0.imprint","IMPRINT",EDGE,{"disambiguationData":[TD([[subQ2,-1.0]])],"derivedFrom":subQ1}),1.0]])]});}
            var Q215;
            {var subQ0=sQuery(id+"F0.wireOp",EDGE,"E34");var subQ1=sQuery(id+"F0.wireOp",EDGE,"E9");var subQ2=makeQuery(id+"F0.imprint","INTERSECT",VERTEX,{"derivedFrom":[subQ1,subQ0]});Q215=makeQuery(id+"F0.imprint","IMPRINT",FACE,{"disambiguationData":[TD([[makeQuery(id+"F0.imprint","IMPRINT",EDGE,{"disambiguationData":[TD([[subQ2,-1.0]])],"derivedFrom":subQ1}),1.0]])]});}
            var Q216;
            {var subQ0=sQuery(id+"F0.wireOp",EDGE,"E13");var subQ1=sQuery(id+"F0.wireOp",EDGE,"E0.top");var subQ2=makeQuery(id+"F0.imprint","INTERSECT",VERTEX,{"derivedFrom":[subQ1,subQ0]});Q216=makeQuery(id+"F0.imprint","IMPRINT",FACE,{"disambiguationData":[TD([[makeQuery(id+"F0.imprint","IMPRINT",EDGE,{"disambiguationData":[TD([[subQ2,-1.0]])],"derivedFrom":subQ1}),1.0]])]});}
            var Q217;
            {var subQ0=sQuery(id+"F0.wireOp",EDGE,"E28");var subQ1=sQuery(id+"F0.wireOp",EDGE,"E0.left");var subQ2=makeQuery(id+"F0.imprint","INTERSECT",VERTEX,{"derivedFrom":[subQ1,subQ0]});Q217=makeQuery(id+"F0.imprint","IMPRINT",FACE,{"disambiguationData":[TD([[makeQuery(id+"F0.imprint","IMPRINT",EDGE,{"disambiguationData":[TD([[subQ2,-1.0]])],"derivedFrom":subQ1}),1.0]])]});}
            var Q218;
            {var subQ0=sQuery(id+"F0.wireOp",EDGE,"E29");var subQ1=sQuery(id+"F0.wireOp",EDGE,"E4");var subQ2=makeQuery(id+"F0.imprint","INTERSECT",VERTEX,{"derivedFrom":[subQ1,subQ0]});Q218=makeQuery(id+"F0.imprint","IMPRINT",FACE,{"disambiguationData":[TD([[makeQuery(id+"F0.imprint","IMPRINT",EDGE,{"disambiguationData":[TD([[subQ2,-1.0]])],"derivedFrom":subQ1}),1.0]])]});}
            var Q219;
            {var subQ0=sQuery(id+"F0.wireOp",EDGE,"E20");var subQ1=sQuery(id+"F0.wireOp",EDGE,"E2");var subQ2=makeQuery(id+"F0.imprint","INTERSECT",VERTEX,{"derivedFrom":[subQ1,subQ0]});Q219=makeQuery(id+"F0.imprint","IMPRINT",FACE,{"disambiguationData":[TD([[makeQuery(id+"F0.imprint","IMPRINT",EDGE,{"disambiguationData":[TD([[subQ2,-1.0]])],"derivedFrom":subQ1}),1.0]])]});}
            var Q220;
            {var subQ0=sQuery(id+"F0.wireOp",EDGE,"E27");var subQ1=sQuery(id+"F0.wireOp",EDGE,"E4");var subQ2=makeQuery(id+"F0.imprint","INTERSECT",VERTEX,{"derivedFrom":[subQ1,subQ0]});Q220=makeQuery(id+"F0.imprint","IMPRINT",FACE,{"disambiguationData":[TD([[makeQuery(id+"F0.imprint","IMPRINT",EDGE,{"disambiguationData":[TD([[subQ2,-1.0]])],"derivedFrom":subQ1}),1.0]])]});}
            var Q221;
            {var subQ0=sQuery(id+"F0.wireOp",EDGE,"E10");var subQ1=sQuery(id+"F0.wireOp",EDGE,"E0.top");var subQ2=makeQuery(id+"F0.imprint","INTERSECT",VERTEX,{"derivedFrom":[subQ1,subQ0]});Q221=makeQuery(id+"F0.imprint","IMPRINT",FACE,{"disambiguationData":[TD([[makeQuery(id+"F0.imprint","IMPRINT",EDGE,{"disambiguationData":[TD([[subQ2,-1.0]])],"derivedFrom":subQ1}),1.0]])]});}
            var Q222;
            {var subQ0=sQuery(id+"F0.wireOp",EDGE,"E21");var subQ1=sQuery(id+"F0.wireOp",EDGE,"E0.left");var subQ2=makeQuery(id+"F0.imprint","INTERSECT",VERTEX,{"derivedFrom":[subQ1,subQ0]});Q222=makeQuery(id+"F0.imprint","IMPRINT",FACE,{"disambiguationData":[TD([[makeQuery(id+"F0.imprint","IMPRINT",EDGE,{"disambiguationData":[TD([[subQ2,-1.0]])],"derivedFrom":subQ1}),1.0]])]});}
            var Q223;
            {var subQ0=sQuery(id+"F0.wireOp",EDGE,"E28");var subQ1=sQuery(id+"F0.wireOp",EDGE,"E15");var subQ2=makeQuery(id+"F0.imprint","INTERSECT",VERTEX,{"derivedFrom":[subQ1,subQ0]});Q223=makeQuery(id+"F0.imprint","IMPRINT",FACE,{"disambiguationData":[TD([[makeQuery(id+"F0.imprint","IMPRINT",EDGE,{"disambiguationData":[TD([[subQ2,-1.0]])],"derivedFrom":subQ1}),1.0]])]});}
            var Q224;
            {var subQ0=sQuery(id+"F0.wireOp",EDGE,"E9");var subQ1=sQuery(id+"F0.wireOp",EDGE,"E0.top");var subQ2=makeQuery(id+"F0.imprint","INTERSECT",VERTEX,{"derivedFrom":[subQ1,subQ0]});Q224=makeQuery(id+"F0.imprint","IMPRINT",FACE,{"disambiguationData":[TD([[makeQuery(id+"F0.imprint","IMPRINT",EDGE,{"disambiguationData":[TD([[subQ2,-1.0]])],"derivedFrom":subQ1}),1.0]])]});}
            var Q225;
            {var subQ0=sQuery(id+"F0.wireOp",EDGE,"E34");var subQ1=sQuery(id+"F0.wireOp",EDGE,"E13");var subQ2=makeQuery(id+"F0.imprint","INTERSECT",VERTEX,{"derivedFrom":[subQ1,subQ0]});Q225=makeQuery(id+"F0.imprint","IMPRINT",FACE,{"disambiguationData":[TD([[makeQuery(id+"F0.imprint","IMPRINT",EDGE,{"disambiguationData":[TD([[subQ2,-1.0]])],"derivedFrom":subQ1}),1.0]])]});}
            var Q226;
            {var subQ0=sQuery(id+"F0.wireOp",EDGE,"E29");var subQ1=sQuery(id+"F0.wireOp",EDGE,"E0.left");var subQ2=makeQuery(id+"F0.imprint","INTERSECT",VERTEX,{"derivedFrom":[subQ1,subQ0]});Q226=makeQuery(id+"F0.imprint","IMPRINT",FACE,{"disambiguationData":[TD([[makeQuery(id+"F0.imprint","IMPRINT",EDGE,{"disambiguationData":[TD([[subQ2,-1.0]])],"derivedFrom":subQ1}),1.0]])]});}
            var Q227;
            {var subQ0=sQuery(id+"F0.wireOp",EDGE,"E31");var subQ1=sQuery(id+"F0.wireOp",EDGE,"E0.right");var subQ2=makeQuery(id+"F0.imprint","INTERSECT",VERTEX,{"derivedFrom":[subQ1,subQ0]});Q227=makeQuery(id+"F0.imprint","IMPRINT",FACE,{"disambiguationData":[TD([[makeQuery(id+"F0.imprint","IMPRINT",EDGE,{"disambiguationData":[TD([[subQ2,-1.0]])],"derivedFrom":subQ1}),-1.0]])]});}
            var Q228;
            {var subQ0=sQuery(id+"F0.wireOp",EDGE,"E11");var subQ1=sQuery(id+"F0.wireOp",EDGE,"E0.top");var subQ2=makeQuery(id+"F0.imprint","INTERSECT",VERTEX,{"derivedFrom":[subQ1,subQ0]});Q228=makeQuery(id+"F0.imprint","IMPRINT",FACE,{"disambiguationData":[TD([[makeQuery(id+"F0.imprint","IMPRINT",EDGE,{"disambiguationData":[TD([[subQ2,-1.0]])],"derivedFrom":subQ1}),1.0]])]});}
            var Q229;
            {var subQ0=sQuery(id+"F0.wireOp",EDGE,"E4");var subQ1=sQuery(id+"F0.wireOp",EDGE,"E0.top");var subQ2=makeQuery(id+"F0.imprint","INTERSECT",VERTEX,{"derivedFrom":[subQ1,subQ0]});Q229=makeQuery(id+"F0.imprint","IMPRINT",FACE,{"disambiguationData":[TD([[makeQuery(id+"F0.imprint","IMPRINT",EDGE,{"disambiguationData":[TD([[subQ2,-1.0]])],"derivedFrom":subQ1}),1.0]])]});}
            var Q230;
            {var subQ0=sQuery(id+"F0.wireOp",EDGE,"E12");var subQ1=sQuery(id+"F0.wireOp",EDGE,"E0.top");var subQ2=makeQuery(id+"F0.imprint","INTERSECT",VERTEX,{"derivedFrom":[subQ1,subQ0]});Q230=makeQuery(id+"F0.imprint","IMPRINT",FACE,{"disambiguationData":[TD([[makeQuery(id+"F0.imprint","IMPRINT",EDGE,{"disambiguationData":[TD([[subQ2,-1.0]])],"derivedFrom":subQ1}),1.0]])]});}
            var Q231;
            {var subQ0=sQuery(id+"F0.wireOp",EDGE,"E28");var subQ1=sQuery(id+"F0.wireOp",EDGE,"E8");var subQ2=makeQuery(id+"F0.imprint","INTERSECT",VERTEX,{"derivedFrom":[subQ1,subQ0]});Q231=makeQuery(id+"F0.imprint","IMPRINT",FACE,{"disambiguationData":[TD([[makeQuery(id+"F0.imprint","IMPRINT",EDGE,{"disambiguationData":[TD([[subQ2,-1.0]])],"derivedFrom":subQ1}),1.0]])]});}
            var Q232;
            {var subQ0=sQuery(id+"F0.wireOp",EDGE,"E20");var subQ1=sQuery(id+"F0.wireOp",EDGE,"E7");var subQ2=makeQuery(id+"F0.imprint","INTERSECT",VERTEX,{"derivedFrom":[subQ1,subQ0]});Q232=makeQuery(id+"F0.imprint","IMPRINT",FACE,{"disambiguationData":[TD([[makeQuery(id+"F0.imprint","IMPRINT",EDGE,{"disambiguationData":[TD([[subQ2,-1.0]])],"derivedFrom":subQ1}),1.0]])]});}
            var Q233;
            {var subQ0=sQuery(id+"F0.wireOp",EDGE,"E2");var subQ1=sQuery(id+"F0.wireOp",EDGE,"E0.top");var subQ2=makeQuery(id+"F0.imprint","INTERSECT",VERTEX,{"derivedFrom":[subQ1,subQ0]});Q233=makeQuery(id+"F0.imprint","IMPRINT",FACE,{"disambiguationData":[TD([[makeQuery(id+"F0.imprint","IMPRINT",EDGE,{"disambiguationData":[TD([[subQ2,-1.0]])],"derivedFrom":subQ1}),1.0]])]});}
            var Q234;
            {var subQ0=sQuery(id+"F0.wireOp",EDGE,"E28");var subQ1=sQuery(id+"F0.wireOp",EDGE,"E2");var subQ2=makeQuery(id+"F0.imprint","INTERSECT",VERTEX,{"derivedFrom":[subQ1,subQ0]});Q234=makeQuery(id+"F0.imprint","IMPRINT",FACE,{"disambiguationData":[TD([[makeQuery(id+"F0.imprint","IMPRINT",EDGE,{"disambiguationData":[TD([[subQ2,-1.0]])],"derivedFrom":subQ1}),1.0]])]});}
            var Q235;
            {var subQ0=sQuery(id+"F0.wireOp",EDGE,"E28");var subQ1=sQuery(id+"F0.wireOp",EDGE,"E5");var subQ2=makeQuery(id+"F0.imprint","INTERSECT",VERTEX,{"derivedFrom":[subQ1,subQ0]});Q235=makeQuery(id+"F0.imprint","IMPRINT",FACE,{"disambiguationData":[TD([[makeQuery(id+"F0.imprint","IMPRINT",EDGE,{"disambiguationData":[TD([[subQ2,-1.0]])],"derivedFrom":subQ1}),1.0]])]});}
            var Q236;
            {var subQ0=sQuery(id+"F0.wireOp",EDGE,"E34");var subQ1=sQuery(id+"F0.wireOp",EDGE,"E6");var subQ2=makeQuery(id+"F0.imprint","INTERSECT",VERTEX,{"derivedFrom":[subQ1,subQ0]});Q236=makeQuery(id+"F0.imprint","IMPRINT",FACE,{"disambiguationData":[TD([[makeQuery(id+"F0.imprint","IMPRINT",EDGE,{"disambiguationData":[TD([[subQ2,-1.0]])],"derivedFrom":subQ1}),1.0]])]});}
            var Q237;
            {var subQ0=sQuery(id+"F0.wireOp",EDGE,"E17");var subQ1=sQuery(id+"F0.wireOp",EDGE,"E0.top");var subQ2=makeQuery(id+"F0.imprint","INTERSECT",VERTEX,{"derivedFrom":[subQ1,subQ0]});Q237=makeQuery(id+"F0.imprint","IMPRINT",FACE,{"disambiguationData":[TD([[makeQuery(id+"F0.imprint","IMPRINT",EDGE,{"disambiguationData":[TD([[subQ2,-1.0]])],"derivedFrom":subQ1}),1.0]])]});}
            var Q238;
            {var subQ0=sQuery(id+"F0.wireOp",EDGE,"E21");var subQ1=sQuery(id+"F0.wireOp",EDGE,"E4");var subQ2=makeQuery(id+"F0.imprint","INTERSECT",VERTEX,{"derivedFrom":[subQ1,subQ0]});Q238=makeQuery(id+"F0.imprint","IMPRINT",FACE,{"disambiguationData":[TD([[makeQuery(id+"F0.imprint","IMPRINT",EDGE,{"disambiguationData":[TD([[subQ2,-1.0]])],"derivedFrom":subQ1}),1.0]])]});}
            var Q239;
            {var subQ0=sQuery(id+"F0.wireOp",EDGE,"E19");var subQ1=sQuery(id+"F0.wireOp",EDGE,"E0.right");var subQ2=makeQuery(id+"F0.imprint","INTERSECT",VERTEX,{"derivedFrom":[subQ1,subQ0]});Q239=makeQuery(id+"F0.imprint","IMPRINT",FACE,{"disambiguationData":[TD([[makeQuery(id+"F0.imprint","IMPRINT",EDGE,{"disambiguationData":[TD([[subQ2,-1.0]])],"derivedFrom":subQ1}),-1.0]])]});}
            var Q240;
            {var subQ0=sQuery(id+"F0.wireOp",EDGE,"E5");var subQ1=sQuery(id+"F0.wireOp",EDGE,"E0.top");var subQ2=makeQuery(id+"F0.imprint","INTERSECT",VERTEX,{"derivedFrom":[subQ1,subQ0]});Q240=makeQuery(id+"F0.imprint","IMPRINT",FACE,{"disambiguationData":[TD([[makeQuery(id+"F0.imprint","IMPRINT",EDGE,{"disambiguationData":[TD([[subQ2,-1.0]])],"derivedFrom":subQ1}),1.0]])]});}
            var Q241;
            {var subQ0=sQuery(id+"F0.wireOp",EDGE,"E1");var subQ1=sQuery(id+"F0.wireOp",EDGE,"E0.bottom");var subQ2=makeQuery(id+"F0.imprint","INTERSECT",VERTEX,{"derivedFrom":[subQ1,subQ0]});Q241=makeQuery(id+"F0.imprint","IMPRINT",FACE,{"disambiguationData":[TD([[makeQuery(id+"F0.imprint","IMPRINT",EDGE,{"disambiguationData":[TD([[subQ2,-1.0]])],"derivedFrom":subQ1}),-1.0]])]});}
            var Q242;
            {var subQ0=sQuery(id+"F0.wireOp",EDGE,"E33");var subQ1=sQuery(id+"F0.wireOp",EDGE,"E4");var subQ2=makeQuery(id+"F0.imprint","INTERSECT",VERTEX,{"derivedFrom":[subQ1,subQ0]});Q242=makeQuery(id+"F0.imprint","IMPRINT",FACE,{"disambiguationData":[TD([[makeQuery(id+"F0.imprint","IMPRINT",EDGE,{"disambiguationData":[TD([[subQ2,-1.0]])],"derivedFrom":subQ1}),1.0]])]});}
            var Q243;
            {var subQ0=sQuery(id+"F0.wireOp",EDGE,"E19");var subQ1=sQuery(id+"F0.wireOp",EDGE,"E4");var subQ2=makeQuery(id+"F0.imprint","INTERSECT",VERTEX,{"derivedFrom":[subQ1,subQ0]});Q243=makeQuery(id+"F0.imprint","IMPRINT",FACE,{"disambiguationData":[TD([[makeQuery(id+"F0.imprint","IMPRINT",EDGE,{"disambiguationData":[TD([[subQ2,-1.0]])],"derivedFrom":subQ1}),1.0]])]});}
            var Q244;
            {var subQ0=sQuery(id+"F0.wireOp",EDGE,"E3");var subQ1=sQuery(id+"F0.wireOp",EDGE,"E0.top");var subQ2=makeQuery(id+"F0.imprint","INTERSECT",VERTEX,{"derivedFrom":[subQ1,subQ0]});Q244=makeQuery(id+"F0.imprint","IMPRINT",FACE,{"disambiguationData":[TD([[makeQuery(id+"F0.imprint","IMPRINT",EDGE,{"disambiguationData":[TD([[subQ2,-1.0]])],"derivedFrom":subQ1}),1.0]])]});}
            var Q245;
            {var subQ0=sQuery(id+"F0.wireOp",EDGE,"E28");var subQ1=sQuery(id+"F0.wireOp",EDGE,"E0.right");var subQ2=makeQuery(id+"F0.imprint","INTERSECT",VERTEX,{"derivedFrom":[subQ1,subQ0]});Q245=makeQuery(id+"F0.imprint","IMPRINT",FACE,{"disambiguationData":[TD([[makeQuery(id+"F0.imprint","IMPRINT",EDGE,{"disambiguationData":[TD([[subQ2,-1.0]])],"derivedFrom":subQ1}),-1.0]])]});}
            var Q246;
            {var subQ0=sQuery(id+"F0.wireOp",EDGE,"E23");var subQ1=sQuery(id+"F0.wireOp",EDGE,"E4");var subQ2=makeQuery(id+"F0.imprint","INTERSECT",VERTEX,{"derivedFrom":[subQ1,subQ0]});Q246=makeQuery(id+"F0.imprint","IMPRINT",FACE,{"disambiguationData":[TD([[makeQuery(id+"F0.imprint","IMPRINT",EDGE,{"disambiguationData":[TD([[subQ2,-1.0]])],"derivedFrom":subQ1}),1.0]])]});}
            var Q247;
            {var subQ0=sQuery(id+"F0.wireOp",EDGE,"E32");var subQ1=sQuery(id+"F0.wireOp",EDGE,"E0.right");var subQ2=makeQuery(id+"F0.imprint","INTERSECT",VERTEX,{"derivedFrom":[subQ1,subQ0]});Q247=makeQuery(id+"F0.imprint","IMPRINT",FACE,{"disambiguationData":[TD([[makeQuery(id+"F0.imprint","IMPRINT",EDGE,{"disambiguationData":[TD([[subQ2,-1.0]])],"derivedFrom":subQ1}),-1.0]])]});}
            var Q248;
            {var subQ0=sQuery(id+"F0.wireOp",EDGE,"E27");var subQ1=sQuery(id+"F0.wireOp",EDGE,"E0.right");var subQ2=makeQuery(id+"F0.imprint","INTERSECT",VERTEX,{"derivedFrom":[subQ1,subQ0]});Q248=makeQuery(id+"F0.imprint","IMPRINT",FACE,{"disambiguationData":[TD([[makeQuery(id+"F0.imprint","IMPRINT",EDGE,{"disambiguationData":[TD([[subQ2,-1.0]])],"derivedFrom":subQ1}),-1.0]])]});}
            var Q249;
            {var subQ0=sQuery(id+"F0.wireOp",EDGE,"E6");var subQ1=sQuery(id+"F0.wireOp",EDGE,"E0.top");var subQ2=makeQuery(id+"F0.imprint","INTERSECT",VERTEX,{"derivedFrom":[subQ1,subQ0]});Q249=makeQuery(id+"F0.imprint","IMPRINT",FACE,{"disambiguationData":[TD([[makeQuery(id+"F0.imprint","IMPRINT",EDGE,{"disambiguationData":[TD([[subQ2,-1.0]])],"derivedFrom":subQ1}),1.0]])]});}
            var Q250;
            {var subQ0=sQuery(id+"F0.wireOp",EDGE,"E20");var subQ1=sQuery(id+"F0.wireOp",EDGE,"E0.left");var subQ2=makeQuery(id+"F0.imprint","INTERSECT",VERTEX,{"derivedFrom":[subQ1,subQ0]});Q250=makeQuery(id+"F0.imprint","IMPRINT",FACE,{"disambiguationData":[TD([[makeQuery(id+"F0.imprint","IMPRINT",EDGE,{"disambiguationData":[TD([[subQ2,-1.0]])],"derivedFrom":subQ1}),1.0]])]});}
            var Q251;
            {var subQ0=sQuery(id+"F0.wireOp",EDGE,"E27");var subQ1=sQuery(id+"F0.wireOp",EDGE,"E0.left");var subQ2=makeQuery(id+"F0.imprint","INTERSECT",VERTEX,{"derivedFrom":[subQ1,subQ0]});Q251=makeQuery(id+"F0.imprint","IMPRINT",FACE,{"disambiguationData":[TD([[makeQuery(id+"F0.imprint","IMPRINT",EDGE,{"disambiguationData":[TD([[subQ2,-1.0]])],"derivedFrom":subQ1}),1.0]])]});}
            var Q252;
            {var subQ0=sQuery(id+"F0.wireOp",EDGE,"E34");var subQ1=sQuery(id+"F0.wireOp",EDGE,"E5");var subQ2=makeQuery(id+"F0.imprint","INTERSECT",VERTEX,{"derivedFrom":[subQ1,subQ0]});Q252=makeQuery(id+"F0.imprint","IMPRINT",FACE,{"disambiguationData":[TD([[makeQuery(id+"F0.imprint","IMPRINT",EDGE,{"disambiguationData":[TD([[subQ2,-1.0]])],"derivedFrom":subQ1}),1.0]])]});}
            var Q253;
            {var subQ0=sQuery(id+"F0.wireOp",EDGE,"E9");var subQ1=sQuery(id+"F0.wireOp",EDGE,"E0.bottom");var subQ2=makeQuery(id+"F0.imprint","INTERSECT",VERTEX,{"derivedFrom":[subQ1,subQ0]});Q253=makeQuery(id+"F0.imprint","IMPRINT",FACE,{"disambiguationData":[TD([[makeQuery(id+"F0.imprint","IMPRINT",EDGE,{"disambiguationData":[TD([[subQ2,-1.0]])],"derivedFrom":subQ1}),-1.0]])]});}
            var Q254;
            {var subQ0=sQuery(id+"F0.wireOp",EDGE,"E28");var subQ1=sQuery(id+"F0.wireOp",EDGE,"E14");var subQ2=makeQuery(id+"F0.imprint","INTERSECT",VERTEX,{"derivedFrom":[subQ1,subQ0]});Q254=makeQuery(id+"F0.imprint","IMPRINT",FACE,{"disambiguationData":[TD([[makeQuery(id+"F0.imprint","IMPRINT",EDGE,{"disambiguationData":[TD([[subQ2,-1.0]])],"derivedFrom":subQ1}),1.0]])]});}
            var Q255;
            {var subQ0=sQuery(id+"F0.wireOp",EDGE,"E34");var subQ1=sQuery(id+"F0.wireOp",EDGE,"E0.right");var subQ2=makeQuery(id+"F0.imprint","INTERSECT",VERTEX,{"derivedFrom":[subQ1,subQ0]});Q255=makeQuery(id+"F0.imprint","IMPRINT",FACE,{"disambiguationData":[TD([[makeQuery(id+"F0.imprint","IMPRINT",EDGE,{"disambiguationData":[TD([[subQ2,-1.0]])],"derivedFrom":subQ1}),-1.0]])]});}
            var Q256;
            {var subQ0=sQuery(id+"F0.wireOp",EDGE,"E28");var subQ1=sQuery(id+"F0.wireOp",EDGE,"E16");var subQ2=makeQuery(id+"F0.imprint","INTERSECT",VERTEX,{"derivedFrom":[subQ1,subQ0]});Q256=makeQuery(id+"F0.imprint","IMPRINT",FACE,{"disambiguationData":[TD([[makeQuery(id+"F0.imprint","IMPRINT",EDGE,{"disambiguationData":[TD([[subQ2,-1.0]])],"derivedFrom":subQ1}),1.0]])]});}
            var Q257;
            {var subQ0=sQuery(id+"F0.wireOp",EDGE,"E24");var subQ1=sQuery(id+"F0.wireOp",EDGE,"E0.right");var subQ2=makeQuery(id+"F0.imprint","INTERSECT",VERTEX,{"derivedFrom":[subQ1,subQ0]});Q257=makeQuery(id+"F0.imprint","IMPRINT",FACE,{"disambiguationData":[TD([[makeQuery(id+"F0.imprint","IMPRINT",EDGE,{"disambiguationData":[TD([[subQ2,-1.0]])],"derivedFrom":subQ1}),-1.0]])]});}
            var Q258;
            {var subQ0=sQuery(id+"F0.wireOp",EDGE,"E20");var subQ1=sQuery(id+"F0.wireOp",EDGE,"E13");var subQ2=makeQuery(id+"F0.imprint","INTERSECT",VERTEX,{"derivedFrom":[subQ1,subQ0]});Q258=makeQuery(id+"F0.imprint","IMPRINT",FACE,{"disambiguationData":[TD([[makeQuery(id+"F0.imprint","IMPRINT",EDGE,{"disambiguationData":[TD([[subQ2,-1.0]])],"derivedFrom":subQ1}),1.0]])]});}
            var Q259;
            {var subQ0=sQuery(id+"F0.wireOp",EDGE,"E20");var subQ1=sQuery(id+"F0.wireOp",EDGE,"E12");var subQ2=makeQuery(id+"F0.imprint","INTERSECT",VERTEX,{"derivedFrom":[subQ1,subQ0]});Q259=makeQuery(id+"F0.imprint","IMPRINT",FACE,{"disambiguationData":[TD([[makeQuery(id+"F0.imprint","IMPRINT",EDGE,{"disambiguationData":[TD([[subQ2,-1.0]])],"derivedFrom":subQ1}),1.0]])]});}
            var Q260;
            {var subQ0=sQuery(id+"F0.wireOp",EDGE,"E12");var subQ1=sQuery(id+"F0.wireOp",EDGE,"E0.bottom");var subQ2=makeQuery(id+"F0.imprint","INTERSECT",VERTEX,{"derivedFrom":[subQ1,subQ0]});Q260=makeQuery(id+"F0.imprint","IMPRINT",FACE,{"disambiguationData":[TD([[makeQuery(id+"F0.imprint","IMPRINT",EDGE,{"disambiguationData":[TD([[subQ2,-1.0]])],"derivedFrom":subQ1}),-1.0]])]});}
            var Q261;
            {var subQ0=sQuery(id+"F0.wireOp",EDGE,"E6");var subQ1=sQuery(id+"F0.wireOp",EDGE,"E0.bottom");var subQ2=makeQuery(id+"F0.imprint","INTERSECT",VERTEX,{"derivedFrom":[subQ1,subQ0]});Q261=makeQuery(id+"F0.imprint","IMPRINT",FACE,{"disambiguationData":[TD([[makeQuery(id+"F0.imprint","IMPRINT",EDGE,{"disambiguationData":[TD([[subQ2,-1.0]])],"derivedFrom":subQ1}),-1.0]])]});}
            var Q262;
            {var subQ0=sQuery(id+"F0.wireOp",EDGE,"E10");var subQ1=sQuery(id+"F0.wireOp",EDGE,"E0.bottom");var subQ2=makeQuery(id+"F0.imprint","INTERSECT",VERTEX,{"derivedFrom":[subQ1,subQ0]});Q262=makeQuery(id+"F0.imprint","IMPRINT",FACE,{"disambiguationData":[TD([[makeQuery(id+"F0.imprint","IMPRINT",EDGE,{"disambiguationData":[TD([[subQ2,-1.0]])],"derivedFrom":subQ1}),-1.0]])]});}
            var Q263;
            {var subQ0=sQuery(id+"F0.wireOp",EDGE,"E34");var subQ1=sQuery(id+"F0.wireOp",EDGE,"E3");var subQ2=makeQuery(id+"F0.imprint","INTERSECT",VERTEX,{"derivedFrom":[subQ1,subQ0]});Q263=makeQuery(id+"F0.imprint","IMPRINT",FACE,{"disambiguationData":[TD([[makeQuery(id+"F0.imprint","IMPRINT",EDGE,{"disambiguationData":[TD([[subQ2,-1.0]])],"derivedFrom":subQ1}),1.0]])]});}
            var Q264;
            {var subQ0=sQuery(id+"F0.wireOp",EDGE,"E15");var subQ1=sQuery(id+"F0.wireOp",EDGE,"E0.top");var subQ2=makeQuery(id+"F0.imprint","INTERSECT",VERTEX,{"derivedFrom":[subQ1,subQ0]});Q264=makeQuery(id+"F0.imprint","IMPRINT",FACE,{"disambiguationData":[TD([[makeQuery(id+"F0.imprint","IMPRINT",EDGE,{"disambiguationData":[TD([[subQ2,-1.0]])],"derivedFrom":subQ1}),1.0]])]});}
            var Q265;
            {var subQ0=sQuery(id+"F0.wireOp",EDGE,"E28");var subQ1=sQuery(id+"F0.wireOp",EDGE,"E4");var subQ2=makeQuery(id+"F0.imprint","INTERSECT",VERTEX,{"derivedFrom":[subQ1,subQ0]});Q265=makeQuery(id+"F0.imprint","IMPRINT",FACE,{"disambiguationData":[TD([[makeQuery(id+"F0.imprint","IMPRINT",EDGE,{"disambiguationData":[TD([[subQ2,-1.0]])],"derivedFrom":subQ1}),1.0]])]});}
            var Q266;
            {var subQ0=sQuery(id+"F0.wireOp",EDGE,"E25");var subQ1=sQuery(id+"F0.wireOp",EDGE,"E0.right");var subQ2=makeQuery(id+"F0.imprint","INTERSECT",VERTEX,{"derivedFrom":[subQ1,subQ0]});Q266=makeQuery(id+"F0.imprint","IMPRINT",FACE,{"disambiguationData":[TD([[makeQuery(id+"F0.imprint","IMPRINT",EDGE,{"disambiguationData":[TD([[subQ2,-1.0]])],"derivedFrom":subQ1}),-1.0]])]});}
            var Q267;
            {var subQ0=sQuery(id+"F0.wireOp",EDGE,"E34");var subQ1=sQuery(id+"F0.wireOp",EDGE,"E4");var subQ2=makeQuery(id+"F0.imprint","INTERSECT",VERTEX,{"derivedFrom":[subQ1,subQ0]});Q267=makeQuery(id+"F0.imprint","IMPRINT",FACE,{"disambiguationData":[TD([[makeQuery(id+"F0.imprint","IMPRINT",EDGE,{"disambiguationData":[TD([[subQ2,-1.0]])],"derivedFrom":subQ1}),1.0]])]});}
            var Q268;
            {var subQ0=sQuery(id+"F0.wireOp",EDGE,"E0.right");var subQ1=sQuery(id+"F0.wireOp",EDGE,"E0.top");var subQ2=makeQuery(id+"F0.imprint","INTERSECT",VERTEX,{"derivedFrom":[subQ1,subQ0]});Q268=makeQuery(id+"F0.imprint","IMPRINT",FACE,{"disambiguationData":[TD([[makeQuery(id+"F0.imprint","IMPRINT",EDGE,{"disambiguationData":[TD([[subQ2,1.0]])],"derivedFrom":subQ1}),1.0]])]});}
            var Q269;
            {var subQ0=sQuery(id+"F0.wireOp",EDGE,"E0.right");var subQ1=sQuery(id+"F0.wireOp",EDGE,"E0.bottom");var subQ2=makeQuery(id+"F0.imprint","INTERSECT",VERTEX,{"derivedFrom":[subQ1,subQ0]});Q269=makeQuery(id+"F0.imprint","IMPRINT",FACE,{"disambiguationData":[TD([[makeQuery(id+"F0.imprint","IMPRINT",EDGE,{"disambiguationData":[TD([[subQ2,1.0]])],"derivedFrom":subQ1}),-1.0]])]});}
            var Q270;
            {var subQ0=sQuery(id+"F0.wireOp",EDGE,"E0.left");var subQ1=sQuery(id+"F0.wireOp",EDGE,"E0.top");var subQ2=makeQuery(id+"F0.imprint","INTERSECT",VERTEX,{"derivedFrom":[subQ1,subQ0]});Q270=makeQuery(id+"F0.imprint","IMPRINT",FACE,{"disambiguationData":[TD([[makeQuery(id+"F0.imprint","IMPRINT",EDGE,{"disambiguationData":[TD([[subQ2,-1.0]])],"derivedFrom":subQ1}),1.0]])]});}
            var Q271;
            {var subQ0=sQuery(id+"F0.wireOp",EDGE,"E0.left");var subQ1=sQuery(id+"F0.wireOp",EDGE,"E0.bottom");var subQ2=makeQuery(id+"F0.imprint","INTERSECT",VERTEX,{"derivedFrom":[subQ1,subQ0]});Q271=makeQuery(id+"F0.imprint","IMPRINT",FACE,{"disambiguationData":[TD([[makeQuery(id+"F0.imprint","IMPRINT",EDGE,{"disambiguationData":[TD([[subQ2,-1.0]])],"derivedFrom":subQ1}),-1.0]])]});}
            var Q272;
            {var subQ0=sQuery(id+"F0.wireOp",EDGE,"E21");var subQ1=sQuery(id+"F0.wireOp",EDGE,"E1");var subQ2=makeQuery(id+"F0.imprint","INTERSECT",VERTEX,{"derivedFrom":[subQ1,subQ0]});Q272=makeQuery(id+"F0.imprint","IMPRINT",FACE,{"disambiguationData":[TD([[makeQuery(id+"F0.imprint","IMPRINT",EDGE,{"disambiguationData":[TD([[subQ2,-1.0]])],"derivedFrom":subQ1}),1.0]])]});}
            var Q273;
            {var subQ0=sQuery(id+"F0.wireOp",EDGE,"E23");var subQ1=sQuery(id+"F0.wireOp",EDGE,"E1");var subQ2=makeQuery(id+"F0.imprint","INTERSECT",VERTEX,{"derivedFrom":[subQ1,subQ0]});Q273=makeQuery(id+"F0.imprint","IMPRINT",FACE,{"disambiguationData":[TD([[makeQuery(id+"F0.imprint","IMPRINT",EDGE,{"disambiguationData":[TD([[subQ2,-1.0]])],"derivedFrom":subQ1}),1.0]])]});}
            var Q274;
            {var subQ0=sQuery(id+"F0.wireOp",EDGE,"E31");var subQ1=sQuery(id+"F0.wireOp",EDGE,"E1");var subQ2=makeQuery(id+"F0.imprint","INTERSECT",VERTEX,{"derivedFrom":[subQ1,subQ0]});Q274=makeQuery(id+"F0.imprint","IMPRINT",FACE,{"disambiguationData":[TD([[makeQuery(id+"F0.imprint","IMPRINT",EDGE,{"disambiguationData":[TD([[subQ2,-1.0]])],"derivedFrom":subQ1}),1.0]])]});}
            var Q275;
            {var subQ0=sQuery(id+"F0.wireOp",EDGE,"E19");var subQ1=sQuery(id+"F0.wireOp",EDGE,"E1");var subQ2=makeQuery(id+"F0.imprint","INTERSECT",VERTEX,{"derivedFrom":[subQ1,subQ0]});Q275=makeQuery(id+"F0.imprint","IMPRINT",FACE,{"disambiguationData":[TD([[makeQuery(id+"F0.imprint","IMPRINT",EDGE,{"disambiguationData":[TD([[subQ2,-1.0]])],"derivedFrom":subQ1}),1.0]])]});}
            var Q276;
            {var subQ0=sQuery(id+"F0.wireOp",EDGE,"E35");var subQ1=sQuery(id+"F0.wireOp",EDGE,"E1");var subQ2=makeQuery(id+"F0.imprint","INTERSECT",VERTEX,{"derivedFrom":[subQ1,subQ0]});Q276=makeQuery(id+"F0.imprint","IMPRINT",FACE,{"disambiguationData":[TD([[makeQuery(id+"F0.imprint","IMPRINT",EDGE,{"disambiguationData":[TD([[subQ2,-1.0]])],"derivedFrom":subQ1}),1.0]])]});}
            var Q277;
            {var subQ0=sQuery(id+"F0.wireOp",EDGE,"E29");var subQ1=sQuery(id+"F0.wireOp",EDGE,"E1");var subQ2=makeQuery(id+"F0.imprint","INTERSECT",VERTEX,{"derivedFrom":[subQ1,subQ0]});Q277=makeQuery(id+"F0.imprint","IMPRINT",FACE,{"disambiguationData":[TD([[makeQuery(id+"F0.imprint","IMPRINT",EDGE,{"disambiguationData":[TD([[subQ2,-1.0]])],"derivedFrom":subQ1}),1.0]])]});}
            var Q278;
            {var subQ0=sQuery(id+"F0.wireOp",EDGE,"E33");var subQ1=sQuery(id+"F0.wireOp",EDGE,"E1");var subQ2=makeQuery(id+"F0.imprint","INTERSECT",VERTEX,{"derivedFrom":[subQ1,subQ0]});Q278=makeQuery(id+"F0.imprint","IMPRINT",FACE,{"disambiguationData":[TD([[makeQuery(id+"F0.imprint","IMPRINT",EDGE,{"disambiguationData":[TD([[subQ2,-1.0]])],"derivedFrom":subQ1}),1.0]])]});}
            var Q279;
            {var subQ0=sQuery(id+"F0.wireOp",EDGE,"E27");var subQ1=sQuery(id+"F0.wireOp",EDGE,"E1");var subQ2=makeQuery(id+"F0.imprint","INTERSECT",VERTEX,{"derivedFrom":[subQ1,subQ0]});Q279=makeQuery(id+"F0.imprint","IMPRINT",FACE,{"disambiguationData":[TD([[makeQuery(id+"F0.imprint","IMPRINT",EDGE,{"disambiguationData":[TD([[subQ2,-1.0]])],"derivedFrom":subQ1}),1.0]])]});}
            var Q280;
            {var subQ0=sQuery(id+"F0.wireOp",EDGE,"E25");var subQ1=sQuery(id+"F0.wireOp",EDGE,"E1");var subQ2=makeQuery(id+"F0.imprint","INTERSECT",VERTEX,{"derivedFrom":[subQ1,subQ0]});Q280=makeQuery(id+"F0.imprint","IMPRINT",FACE,{"disambiguationData":[TD([[makeQuery(id+"F0.imprint","IMPRINT",EDGE,{"disambiguationData":[TD([[subQ2,-1.0]])],"derivedFrom":subQ1}),1.0]])]});}
            var Q281;
            {var subQ0=sQuery(id+"F0.wireOp",EDGE,"E19");var subQ1=sQuery(id+"F0.wireOp",EDGE,"E17");var subQ2=makeQuery(id+"F0.imprint","INTERSECT",VERTEX,{"derivedFrom":[subQ1,subQ0]});Q281=makeQuery(id+"F0.imprint","IMPRINT",FACE,{"disambiguationData":[TD([[makeQuery(id+"F0.imprint","IMPRINT",EDGE,{"disambiguationData":[TD([[subQ2,-1.0]])],"derivedFrom":subQ1}),1.0]])]});}
            var Q282;
            {var subQ0=sQuery(id+"F0.wireOp",EDGE,"E21");var subQ1=sQuery(id+"F0.wireOp",EDGE,"E17");var subQ2=makeQuery(id+"F0.imprint","INTERSECT",VERTEX,{"derivedFrom":[subQ1,subQ0]});Q282=makeQuery(id+"F0.imprint","IMPRINT",FACE,{"disambiguationData":[TD([[makeQuery(id+"F0.imprint","IMPRINT",EDGE,{"disambiguationData":[TD([[subQ2,-1.0]])],"derivedFrom":subQ1}),1.0]])]});}
            var Q283;
            {var subQ0=sQuery(id+"F0.wireOp",EDGE,"E23");var subQ1=sQuery(id+"F0.wireOp",EDGE,"E17");var subQ2=makeQuery(id+"F0.imprint","INTERSECT",VERTEX,{"derivedFrom":[subQ1,subQ0]});Q283=makeQuery(id+"F0.imprint","IMPRINT",FACE,{"disambiguationData":[TD([[makeQuery(id+"F0.imprint","IMPRINT",EDGE,{"disambiguationData":[TD([[subQ2,-1.0]])],"derivedFrom":subQ1}),1.0]])]});}
            var Q284;
            {var subQ0=sQuery(id+"F0.wireOp",EDGE,"E25");var subQ1=sQuery(id+"F0.wireOp",EDGE,"E17");var subQ2=makeQuery(id+"F0.imprint","INTERSECT",VERTEX,{"derivedFrom":[subQ1,subQ0]});Q284=makeQuery(id+"F0.imprint","IMPRINT",FACE,{"disambiguationData":[TD([[makeQuery(id+"F0.imprint","IMPRINT",EDGE,{"disambiguationData":[TD([[subQ2,-1.0]])],"derivedFrom":subQ1}),1.0]])]});}
            var Q285;
            {var subQ0=sQuery(id+"F0.wireOp",EDGE,"E27");var subQ1=sQuery(id+"F0.wireOp",EDGE,"E17");var subQ2=makeQuery(id+"F0.imprint","INTERSECT",VERTEX,{"derivedFrom":[subQ1,subQ0]});Q285=makeQuery(id+"F0.imprint","IMPRINT",FACE,{"disambiguationData":[TD([[makeQuery(id+"F0.imprint","IMPRINT",EDGE,{"disambiguationData":[TD([[subQ2,-1.0]])],"derivedFrom":subQ1}),1.0]])]});}
            var Q286;
            {var subQ0=sQuery(id+"F0.wireOp",EDGE,"E29");var subQ1=sQuery(id+"F0.wireOp",EDGE,"E17");var subQ2=makeQuery(id+"F0.imprint","INTERSECT",VERTEX,{"derivedFrom":[subQ1,subQ0]});Q286=makeQuery(id+"F0.imprint","IMPRINT",FACE,{"disambiguationData":[TD([[makeQuery(id+"F0.imprint","IMPRINT",EDGE,{"disambiguationData":[TD([[subQ2,-1.0]])],"derivedFrom":subQ1}),1.0]])]});}
            var Q287;
            {var subQ0=sQuery(id+"F0.wireOp",EDGE,"E31");var subQ1=sQuery(id+"F0.wireOp",EDGE,"E17");var subQ2=makeQuery(id+"F0.imprint","INTERSECT",VERTEX,{"derivedFrom":[subQ1,subQ0]});Q287=makeQuery(id+"F0.imprint","IMPRINT",FACE,{"disambiguationData":[TD([[makeQuery(id+"F0.imprint","IMPRINT",EDGE,{"disambiguationData":[TD([[subQ2,-1.0]])],"derivedFrom":subQ1}),1.0]])]});}
            var Q288;
            {var subQ0=sQuery(id+"F0.wireOp",EDGE,"E33");var subQ1=sQuery(id+"F0.wireOp",EDGE,"E17");var subQ2=makeQuery(id+"F0.imprint","INTERSECT",VERTEX,{"derivedFrom":[subQ1,subQ0]});Q288=makeQuery(id+"F0.imprint","IMPRINT",FACE,{"disambiguationData":[TD([[makeQuery(id+"F0.imprint","IMPRINT",EDGE,{"disambiguationData":[TD([[subQ2,-1.0]])],"derivedFrom":subQ1}),1.0]])]});}
            var Q289;
            {var subQ0=sQuery(id+"F0.wireOp",EDGE,"E35");var subQ1=sQuery(id+"F0.wireOp",EDGE,"E17");var subQ2=makeQuery(id+"F0.imprint","INTERSECT",VERTEX,{"derivedFrom":[subQ1,subQ0]});Q289=makeQuery(id+"F0.imprint","IMPRINT",FACE,{"disambiguationData":[TD([[makeQuery(id+"F0.imprint","IMPRINT",EDGE,{"disambiguationData":[TD([[subQ2,-1.0]])],"derivedFrom":subQ1}),1.0]])]});}
            var Q290;
            {var subQ0=sQuery(id+"F0.wireOp",EDGE,"E21");var subQ1=sQuery(id+"F0.wireOp",EDGE,"E5");var subQ2=makeQuery(id+"F0.imprint","INTERSECT",VERTEX,{"derivedFrom":[subQ1,subQ0]});Q290=makeQuery(id+"F0.imprint","IMPRINT",FACE,{"disambiguationData":[TD([[makeQuery(id+"F0.imprint","IMPRINT",EDGE,{"disambiguationData":[TD([[subQ2,-1.0]])],"derivedFrom":subQ1}),1.0]])]});}
            var Q291;
            {var subQ0=sQuery(id+"F0.wireOp",EDGE,"E21");var subQ1=sQuery(id+"F0.wireOp",EDGE,"E7");var subQ2=makeQuery(id+"F0.imprint","INTERSECT",VERTEX,{"derivedFrom":[subQ1,subQ0]});Q291=makeQuery(id+"F0.imprint","IMPRINT",FACE,{"disambiguationData":[TD([[makeQuery(id+"F0.imprint","IMPRINT",EDGE,{"disambiguationData":[TD([[subQ2,-1.0]])],"derivedFrom":subQ1}),1.0]])]});}
            var Q292;
            {var subQ0=sQuery(id+"F0.wireOp",EDGE,"E21");var subQ1=sQuery(id+"F0.wireOp",EDGE,"E9");var subQ2=makeQuery(id+"F0.imprint","INTERSECT",VERTEX,{"derivedFrom":[subQ1,subQ0]});Q292=makeQuery(id+"F0.imprint","IMPRINT",FACE,{"disambiguationData":[TD([[makeQuery(id+"F0.imprint","IMPRINT",EDGE,{"disambiguationData":[TD([[subQ2,-1.0]])],"derivedFrom":subQ1}),1.0]])]});}
            var Q293;
            {var subQ0=sQuery(id+"F0.wireOp",EDGE,"E21");var subQ1=sQuery(id+"F0.wireOp",EDGE,"E11");var subQ2=makeQuery(id+"F0.imprint","INTERSECT",VERTEX,{"derivedFrom":[subQ1,subQ0]});Q293=makeQuery(id+"F0.imprint","IMPRINT",FACE,{"disambiguationData":[TD([[makeQuery(id+"F0.imprint","IMPRINT",EDGE,{"disambiguationData":[TD([[subQ2,-1.0]])],"derivedFrom":subQ1}),1.0]])]});}
            var Q294;
            {var subQ0=sQuery(id+"F0.wireOp",EDGE,"E21");var subQ1=sQuery(id+"F0.wireOp",EDGE,"E13");var subQ2=makeQuery(id+"F0.imprint","INTERSECT",VERTEX,{"derivedFrom":[subQ1,subQ0]});Q294=makeQuery(id+"F0.imprint","IMPRINT",FACE,{"disambiguationData":[TD([[makeQuery(id+"F0.imprint","IMPRINT",EDGE,{"disambiguationData":[TD([[subQ2,-1.0]])],"derivedFrom":subQ1}),1.0]])]});}
            var Q295;
            {var subQ0=sQuery(id+"F0.wireOp",EDGE,"E21");var subQ1=sQuery(id+"F0.wireOp",EDGE,"E15");var subQ2=makeQuery(id+"F0.imprint","INTERSECT",VERTEX,{"derivedFrom":[subQ1,subQ0]});Q295=makeQuery(id+"F0.imprint","IMPRINT",FACE,{"disambiguationData":[TD([[makeQuery(id+"F0.imprint","IMPRINT",EDGE,{"disambiguationData":[TD([[subQ2,-1.0]])],"derivedFrom":subQ1}),1.0]])]});}
            var Q296;
            {var subQ0=sQuery(id+"F0.wireOp",EDGE,"E19");var subQ1=sQuery(id+"F0.wireOp",EDGE,"E15");var subQ2=makeQuery(id+"F0.imprint","INTERSECT",VERTEX,{"derivedFrom":[subQ1,subQ0]});Q296=makeQuery(id+"F0.imprint","IMPRINT",FACE,{"disambiguationData":[TD([[makeQuery(id+"F0.imprint","IMPRINT",EDGE,{"disambiguationData":[TD([[subQ2,-1.0]])],"derivedFrom":subQ1}),1.0]])]});}
            var Q297;
            {var subQ0=sQuery(id+"F0.wireOp",EDGE,"E23");var subQ1=sQuery(id+"F0.wireOp",EDGE,"E15");var subQ2=makeQuery(id+"F0.imprint","INTERSECT",VERTEX,{"derivedFrom":[subQ1,subQ0]});Q297=makeQuery(id+"F0.imprint","IMPRINT",FACE,{"disambiguationData":[TD([[makeQuery(id+"F0.imprint","IMPRINT",EDGE,{"disambiguationData":[TD([[subQ2,-1.0]])],"derivedFrom":subQ1}),1.0]])]});}
            var Q298;
            {var subQ0=sQuery(id+"F0.wireOp",EDGE,"E25");var subQ1=sQuery(id+"F0.wireOp",EDGE,"E15");var subQ2=makeQuery(id+"F0.imprint","INTERSECT",VERTEX,{"derivedFrom":[subQ1,subQ0]});Q298=makeQuery(id+"F0.imprint","IMPRINT",FACE,{"disambiguationData":[TD([[makeQuery(id+"F0.imprint","IMPRINT",EDGE,{"disambiguationData":[TD([[subQ2,-1.0]])],"derivedFrom":subQ1}),1.0]])]});}
            var Q299;
            {var subQ0=sQuery(id+"F0.wireOp",EDGE,"E27");var subQ1=sQuery(id+"F0.wireOp",EDGE,"E15");var subQ2=makeQuery(id+"F0.imprint","INTERSECT",VERTEX,{"derivedFrom":[subQ1,subQ0]});Q299=makeQuery(id+"F0.imprint","IMPRINT",FACE,{"disambiguationData":[TD([[makeQuery(id+"F0.imprint","IMPRINT",EDGE,{"disambiguationData":[TD([[subQ2,-1.0]])],"derivedFrom":subQ1}),1.0]])]});}
            var Q300;
            {var subQ0=sQuery(id+"F0.wireOp",EDGE,"E29");var subQ1=sQuery(id+"F0.wireOp",EDGE,"E15");var subQ2=makeQuery(id+"F0.imprint","INTERSECT",VERTEX,{"derivedFrom":[subQ1,subQ0]});Q300=makeQuery(id+"F0.imprint","IMPRINT",FACE,{"disambiguationData":[TD([[makeQuery(id+"F0.imprint","IMPRINT",EDGE,{"disambiguationData":[TD([[subQ2,-1.0]])],"derivedFrom":subQ1}),1.0]])]});}
            var Q301;
            {var subQ0=sQuery(id+"F0.wireOp",EDGE,"E31");var subQ1=sQuery(id+"F0.wireOp",EDGE,"E15");var subQ2=makeQuery(id+"F0.imprint","INTERSECT",VERTEX,{"derivedFrom":[subQ1,subQ0]});Q301=makeQuery(id+"F0.imprint","IMPRINT",FACE,{"disambiguationData":[TD([[makeQuery(id+"F0.imprint","IMPRINT",EDGE,{"disambiguationData":[TD([[subQ2,-1.0]])],"derivedFrom":subQ1}),1.0]])]});}
            var Q302;
            {var subQ0=sQuery(id+"F0.wireOp",EDGE,"E33");var subQ1=sQuery(id+"F0.wireOp",EDGE,"E15");var subQ2=makeQuery(id+"F0.imprint","INTERSECT",VERTEX,{"derivedFrom":[subQ1,subQ0]});Q302=makeQuery(id+"F0.imprint","IMPRINT",FACE,{"disambiguationData":[TD([[makeQuery(id+"F0.imprint","IMPRINT",EDGE,{"disambiguationData":[TD([[subQ2,-1.0]])],"derivedFrom":subQ1}),1.0]])]});}
            var Q303;
            {var subQ0=sQuery(id+"F0.wireOp",EDGE,"E35");var subQ1=sQuery(id+"F0.wireOp",EDGE,"E15");var subQ2=makeQuery(id+"F0.imprint","INTERSECT",VERTEX,{"derivedFrom":[subQ1,subQ0]});Q303=makeQuery(id+"F0.imprint","IMPRINT",FACE,{"disambiguationData":[TD([[makeQuery(id+"F0.imprint","IMPRINT",EDGE,{"disambiguationData":[TD([[subQ2,-1.0]])],"derivedFrom":subQ1}),1.0]])]});}
            var Q304;
            {var subQ0=sQuery(id+"F0.wireOp",EDGE,"E23");var subQ1=sQuery(id+"F0.wireOp",EDGE,"E5");var subQ2=makeQuery(id+"F0.imprint","INTERSECT",VERTEX,{"derivedFrom":[subQ1,subQ0]});Q304=makeQuery(id+"F0.imprint","IMPRINT",FACE,{"disambiguationData":[TD([[makeQuery(id+"F0.imprint","IMPRINT",EDGE,{"disambiguationData":[TD([[subQ2,-1.0]])],"derivedFrom":subQ1}),1.0]])]});}
            var Q305;
            {var subQ0=sQuery(id+"F0.wireOp",EDGE,"E23");var subQ1=sQuery(id+"F0.wireOp",EDGE,"E7");var subQ2=makeQuery(id+"F0.imprint","INTERSECT",VERTEX,{"derivedFrom":[subQ1,subQ0]});Q305=makeQuery(id+"F0.imprint","IMPRINT",FACE,{"disambiguationData":[TD([[makeQuery(id+"F0.imprint","IMPRINT",EDGE,{"disambiguationData":[TD([[subQ2,-1.0]])],"derivedFrom":subQ1}),1.0]])]});}
            var Q306;
            {var subQ0=sQuery(id+"F0.wireOp",EDGE,"E23");var subQ1=sQuery(id+"F0.wireOp",EDGE,"E9");var subQ2=makeQuery(id+"F0.imprint","INTERSECT",VERTEX,{"derivedFrom":[subQ1,subQ0]});Q306=makeQuery(id+"F0.imprint","IMPRINT",FACE,{"disambiguationData":[TD([[makeQuery(id+"F0.imprint","IMPRINT",EDGE,{"disambiguationData":[TD([[subQ2,-1.0]])],"derivedFrom":subQ1}),1.0]])]});}
            var Q307;
            {var subQ0=sQuery(id+"F0.wireOp",EDGE,"E23");var subQ1=sQuery(id+"F0.wireOp",EDGE,"E11");var subQ2=makeQuery(id+"F0.imprint","INTERSECT",VERTEX,{"derivedFrom":[subQ1,subQ0]});Q307=makeQuery(id+"F0.imprint","IMPRINT",FACE,{"disambiguationData":[TD([[makeQuery(id+"F0.imprint","IMPRINT",EDGE,{"disambiguationData":[TD([[subQ2,-1.0]])],"derivedFrom":subQ1}),1.0]])]});}
            var Q308;
            {var subQ0=sQuery(id+"F0.wireOp",EDGE,"E23");var subQ1=sQuery(id+"F0.wireOp",EDGE,"E13");var subQ2=makeQuery(id+"F0.imprint","INTERSECT",VERTEX,{"derivedFrom":[subQ1,subQ0]});Q308=makeQuery(id+"F0.imprint","IMPRINT",FACE,{"disambiguationData":[TD([[makeQuery(id+"F0.imprint","IMPRINT",EDGE,{"disambiguationData":[TD([[subQ2,-1.0]])],"derivedFrom":subQ1}),1.0]])]});}
            var Q309;
            {var subQ0=sQuery(id+"F0.wireOp",EDGE,"E19");var subQ1=sQuery(id+"F0.wireOp",EDGE,"E13");var subQ2=makeQuery(id+"F0.imprint","INTERSECT",VERTEX,{"derivedFrom":[subQ1,subQ0]});Q309=makeQuery(id+"F0.imprint","IMPRINT",FACE,{"disambiguationData":[TD([[makeQuery(id+"F0.imprint","IMPRINT",EDGE,{"disambiguationData":[TD([[subQ2,-1.0]])],"derivedFrom":subQ1}),1.0]])]});}
            var Q310;
            {var subQ0=sQuery(id+"F0.wireOp",EDGE,"E25");var subQ1=sQuery(id+"F0.wireOp",EDGE,"E13");var subQ2=makeQuery(id+"F0.imprint","INTERSECT",VERTEX,{"derivedFrom":[subQ1,subQ0]});Q310=makeQuery(id+"F0.imprint","IMPRINT",FACE,{"disambiguationData":[TD([[makeQuery(id+"F0.imprint","IMPRINT",EDGE,{"disambiguationData":[TD([[subQ2,-1.0]])],"derivedFrom":subQ1}),1.0]])]});}
            var Q311;
            {var subQ0=sQuery(id+"F0.wireOp",EDGE,"E25");var subQ1=sQuery(id+"F0.wireOp",EDGE,"E11");var subQ2=makeQuery(id+"F0.imprint","INTERSECT",VERTEX,{"derivedFrom":[subQ1,subQ0]});Q311=makeQuery(id+"F0.imprint","IMPRINT",FACE,{"disambiguationData":[TD([[makeQuery(id+"F0.imprint","IMPRINT",EDGE,{"disambiguationData":[TD([[subQ2,-1.0]])],"derivedFrom":subQ1}),1.0]])]});}
            var Q312;
            {var subQ0=sQuery(id+"F0.wireOp",EDGE,"E19");var subQ1=sQuery(id+"F0.wireOp",EDGE,"E7");var subQ2=makeQuery(id+"F0.imprint","INTERSECT",VERTEX,{"derivedFrom":[subQ1,subQ0]});Q312=makeQuery(id+"F0.imprint","IMPRINT",FACE,{"disambiguationData":[TD([[makeQuery(id+"F0.imprint","IMPRINT",EDGE,{"disambiguationData":[TD([[subQ2,-1.0]])],"derivedFrom":subQ1}),1.0]])]});}
            var Q313;
            {var subQ0=sQuery(id+"F0.wireOp",EDGE,"E33");var subQ1=sQuery(id+"F0.wireOp",EDGE,"E7");var subQ2=makeQuery(id+"F0.imprint","INTERSECT",VERTEX,{"derivedFrom":[subQ1,subQ0]});Q313=makeQuery(id+"F0.imprint","IMPRINT",FACE,{"disambiguationData":[TD([[makeQuery(id+"F0.imprint","IMPRINT",EDGE,{"disambiguationData":[TD([[subQ2,-1.0]])],"derivedFrom":subQ1}),1.0]])]});}
            var Q314;
            {var subQ0=sQuery(id+"F0.wireOp",EDGE,"E35");var subQ1=sQuery(id+"F0.wireOp",EDGE,"E7");var subQ2=makeQuery(id+"F0.imprint","INTERSECT",VERTEX,{"derivedFrom":[subQ1,subQ0]});Q314=makeQuery(id+"F0.imprint","IMPRINT",FACE,{"disambiguationData":[TD([[makeQuery(id+"F0.imprint","IMPRINT",EDGE,{"disambiguationData":[TD([[subQ2,-1.0]])],"derivedFrom":subQ1}),1.0]])]});}
            var Q315;
            {var subQ0=sQuery(id+"F0.wireOp",EDGE,"E27");var subQ1=sQuery(id+"F0.wireOp",EDGE,"E11");var subQ2=makeQuery(id+"F0.imprint","INTERSECT",VERTEX,{"derivedFrom":[subQ1,subQ0]});Q315=makeQuery(id+"F0.imprint","IMPRINT",FACE,{"disambiguationData":[TD([[makeQuery(id+"F0.imprint","IMPRINT",EDGE,{"disambiguationData":[TD([[subQ2,-1.0]])],"derivedFrom":subQ1}),1.0]])]});}
            var Q316;
            {var subQ0=sQuery(id+"F0.wireOp",EDGE,"E27");var subQ1=sQuery(id+"F0.wireOp",EDGE,"E13");var subQ2=makeQuery(id+"F0.imprint","INTERSECT",VERTEX,{"derivedFrom":[subQ1,subQ0]});Q316=makeQuery(id+"F0.imprint","IMPRINT",FACE,{"disambiguationData":[TD([[makeQuery(id+"F0.imprint","IMPRINT",EDGE,{"disambiguationData":[TD([[subQ2,-1.0]])],"derivedFrom":subQ1}),1.0]])]});}
            var Q317;
            {var subQ0=sQuery(id+"F0.wireOp",EDGE,"E19");var subQ1=sQuery(id+"F0.wireOp",EDGE,"E5");var subQ2=makeQuery(id+"F0.imprint","INTERSECT",VERTEX,{"derivedFrom":[subQ1,subQ0]});Q317=makeQuery(id+"F0.imprint","IMPRINT",FACE,{"disambiguationData":[TD([[makeQuery(id+"F0.imprint","IMPRINT",EDGE,{"disambiguationData":[TD([[subQ2,-1.0]])],"derivedFrom":subQ1}),1.0]])]});}
            var Q318;
            {var subQ0=sQuery(id+"F0.wireOp",EDGE,"E33");var subQ1=sQuery(id+"F0.wireOp",EDGE,"E5");var subQ2=makeQuery(id+"F0.imprint","INTERSECT",VERTEX,{"derivedFrom":[subQ1,subQ0]});Q318=makeQuery(id+"F0.imprint","IMPRINT",FACE,{"disambiguationData":[TD([[makeQuery(id+"F0.imprint","IMPRINT",EDGE,{"disambiguationData":[TD([[subQ2,-1.0]])],"derivedFrom":subQ1}),1.0]])]});}
            var Q319;
            {var subQ0=sQuery(id+"F0.wireOp",EDGE,"E19");var subQ1=sQuery(id+"F0.wireOp",EDGE,"E9");var subQ2=makeQuery(id+"F0.imprint","INTERSECT",VERTEX,{"derivedFrom":[subQ1,subQ0]});Q319=makeQuery(id+"F0.imprint","IMPRINT",FACE,{"disambiguationData":[TD([[makeQuery(id+"F0.imprint","IMPRINT",EDGE,{"disambiguationData":[TD([[subQ2,-1.0]])],"derivedFrom":subQ1}),1.0]])]});}
            var Q320;
            {var subQ0=sQuery(id+"F0.wireOp",EDGE,"E31");var subQ1=sQuery(id+"F0.wireOp",EDGE,"E9");var subQ2=makeQuery(id+"F0.imprint","INTERSECT",VERTEX,{"derivedFrom":[subQ1,subQ0]});Q320=makeQuery(id+"F0.imprint","IMPRINT",FACE,{"disambiguationData":[TD([[makeQuery(id+"F0.imprint","IMPRINT",EDGE,{"disambiguationData":[TD([[subQ2,-1.0]])],"derivedFrom":subQ1}),1.0]])]});}
            var Q321;
            {var subQ0=sQuery(id+"F0.wireOp",EDGE,"E35");var subQ1=sQuery(id+"F0.wireOp",EDGE,"E5");var subQ2=makeQuery(id+"F0.imprint","INTERSECT",VERTEX,{"derivedFrom":[subQ1,subQ0]});Q321=makeQuery(id+"F0.imprint","IMPRINT",FACE,{"disambiguationData":[TD([[makeQuery(id+"F0.imprint","IMPRINT",EDGE,{"disambiguationData":[TD([[subQ2,-1.0]])],"derivedFrom":subQ1}),1.0]])]});}
            var Q322;
            {var subQ0=sQuery(id+"F0.wireOp",EDGE,"E31");var subQ1=sQuery(id+"F0.wireOp",EDGE,"E5");var subQ2=makeQuery(id+"F0.imprint","INTERSECT",VERTEX,{"derivedFrom":[subQ1,subQ0]});Q322=makeQuery(id+"F0.imprint","IMPRINT",FACE,{"disambiguationData":[TD([[makeQuery(id+"F0.imprint","IMPRINT",EDGE,{"disambiguationData":[TD([[subQ2,-1.0]])],"derivedFrom":subQ1}),1.0]])]});}
            var Q323;
            {var subQ0=sQuery(id+"F0.wireOp",EDGE,"E31");var subQ1=sQuery(id+"F0.wireOp",EDGE,"E11");var subQ2=makeQuery(id+"F0.imprint","INTERSECT",VERTEX,{"derivedFrom":[subQ1,subQ0]});Q323=makeQuery(id+"F0.imprint","IMPRINT",FACE,{"disambiguationData":[TD([[makeQuery(id+"F0.imprint","IMPRINT",EDGE,{"disambiguationData":[TD([[subQ2,-1.0]])],"derivedFrom":subQ1}),1.0]])]});}
            var Q324;
            {var subQ0=sQuery(id+"F0.wireOp",EDGE,"E35");var subQ1=sQuery(id+"F0.wireOp",EDGE,"E9");var subQ2=makeQuery(id+"F0.imprint","INTERSECT",VERTEX,{"derivedFrom":[subQ1,subQ0]});Q324=makeQuery(id+"F0.imprint","IMPRINT",FACE,{"disambiguationData":[TD([[makeQuery(id+"F0.imprint","IMPRINT",EDGE,{"disambiguationData":[TD([[subQ2,-1.0]])],"derivedFrom":subQ1}),1.0]])]});}
            var Q325;
            {var subQ0=sQuery(id+"F0.wireOp",EDGE,"E31");var subQ1=sQuery(id+"F0.wireOp",EDGE,"E7");var subQ2=makeQuery(id+"F0.imprint","INTERSECT",VERTEX,{"derivedFrom":[subQ1,subQ0]});Q325=makeQuery(id+"F0.imprint","IMPRINT",FACE,{"disambiguationData":[TD([[makeQuery(id+"F0.imprint","IMPRINT",EDGE,{"disambiguationData":[TD([[subQ2,-1.0]])],"derivedFrom":subQ1}),1.0]])]});}
            var Q326;
            {var subQ0=sQuery(id+"F0.wireOp",EDGE,"E31");var subQ1=sQuery(id+"F0.wireOp",EDGE,"E13");var subQ2=makeQuery(id+"F0.imprint","INTERSECT",VERTEX,{"derivedFrom":[subQ1,subQ0]});Q326=makeQuery(id+"F0.imprint","IMPRINT",FACE,{"disambiguationData":[TD([[makeQuery(id+"F0.imprint","IMPRINT",EDGE,{"disambiguationData":[TD([[subQ2,-1.0]])],"derivedFrom":subQ1}),1.0]])]});}
            var Q327;
            {var subQ0=sQuery(id+"F0.wireOp",EDGE,"E25");var subQ1=sQuery(id+"F0.wireOp",EDGE,"E5");var subQ2=makeQuery(id+"F0.imprint","INTERSECT",VERTEX,{"derivedFrom":[subQ1,subQ0]});Q327=makeQuery(id+"F0.imprint","IMPRINT",FACE,{"disambiguationData":[TD([[makeQuery(id+"F0.imprint","IMPRINT",EDGE,{"disambiguationData":[TD([[subQ2,-1.0]])],"derivedFrom":subQ1}),1.0]])]});}
            var Q328;
            {var subQ0=sQuery(id+"F0.wireOp",EDGE,"E29");var subQ1=sQuery(id+"F0.wireOp",EDGE,"E5");var subQ2=makeQuery(id+"F0.imprint","INTERSECT",VERTEX,{"derivedFrom":[subQ1,subQ0]});Q328=makeQuery(id+"F0.imprint","IMPRINT",FACE,{"disambiguationData":[TD([[makeQuery(id+"F0.imprint","IMPRINT",EDGE,{"disambiguationData":[TD([[subQ2,-1.0]])],"derivedFrom":subQ1}),1.0]])]});}
            var Q329;
            {var subQ0=sQuery(id+"F0.wireOp",EDGE,"E29");var subQ1=sQuery(id+"F0.wireOp",EDGE,"E11");var subQ2=makeQuery(id+"F0.imprint","INTERSECT",VERTEX,{"derivedFrom":[subQ1,subQ0]});Q329=makeQuery(id+"F0.imprint","IMPRINT",FACE,{"disambiguationData":[TD([[makeQuery(id+"F0.imprint","IMPRINT",EDGE,{"disambiguationData":[TD([[subQ2,-1.0]])],"derivedFrom":subQ1}),1.0]])]});}
            var Q330;
            {var subQ0=sQuery(id+"F0.wireOp",EDGE,"E29");var subQ1=sQuery(id+"F0.wireOp",EDGE,"E7");var subQ2=makeQuery(id+"F0.imprint","INTERSECT",VERTEX,{"derivedFrom":[subQ1,subQ0]});Q330=makeQuery(id+"F0.imprint","IMPRINT",FACE,{"disambiguationData":[TD([[makeQuery(id+"F0.imprint","IMPRINT",EDGE,{"disambiguationData":[TD([[subQ2,-1.0]])],"derivedFrom":subQ1}),1.0]])]});}
            var Q331;
            {var subQ0=sQuery(id+"F0.wireOp",EDGE,"E29");var subQ1=sQuery(id+"F0.wireOp",EDGE,"E13");var subQ2=makeQuery(id+"F0.imprint","INTERSECT",VERTEX,{"derivedFrom":[subQ1,subQ0]});Q331=makeQuery(id+"F0.imprint","IMPRINT",FACE,{"disambiguationData":[TD([[makeQuery(id+"F0.imprint","IMPRINT",EDGE,{"disambiguationData":[TD([[subQ2,-1.0]])],"derivedFrom":subQ1}),1.0]])]});}
            var Q332;
            {var subQ0=sQuery(id+"F0.wireOp",EDGE,"E33");var subQ1=sQuery(id+"F0.wireOp",EDGE,"E9");var subQ2=makeQuery(id+"F0.imprint","INTERSECT",VERTEX,{"derivedFrom":[subQ1,subQ0]});Q332=makeQuery(id+"F0.imprint","IMPRINT",FACE,{"disambiguationData":[TD([[makeQuery(id+"F0.imprint","IMPRINT",EDGE,{"disambiguationData":[TD([[subQ2,-1.0]])],"derivedFrom":subQ1}),1.0]])]});}
            var Q333;
            {var subQ0=sQuery(id+"F0.wireOp",EDGE,"E29");var subQ1=sQuery(id+"F0.wireOp",EDGE,"E9");var subQ2=makeQuery(id+"F0.imprint","INTERSECT",VERTEX,{"derivedFrom":[subQ1,subQ0]});Q333=makeQuery(id+"F0.imprint","IMPRINT",FACE,{"disambiguationData":[TD([[makeQuery(id+"F0.imprint","IMPRINT",EDGE,{"disambiguationData":[TD([[subQ2,-1.0]])],"derivedFrom":subQ1}),1.0]])]});}
            var Q334;
            {var subQ0=sQuery(id+"F0.wireOp",EDGE,"E27");var subQ1=sQuery(id+"F0.wireOp",EDGE,"E7");var subQ2=makeQuery(id+"F0.imprint","INTERSECT",VERTEX,{"derivedFrom":[subQ1,subQ0]});Q334=makeQuery(id+"F0.imprint","IMPRINT",FACE,{"disambiguationData":[TD([[makeQuery(id+"F0.imprint","IMPRINT",EDGE,{"disambiguationData":[TD([[subQ2,-1.0]])],"derivedFrom":subQ1}),1.0]])]});}
            var Q335;
            {var subQ0=sQuery(id+"F0.wireOp",EDGE,"E27");var subQ1=sQuery(id+"F0.wireOp",EDGE,"E5");var subQ2=makeQuery(id+"F0.imprint","INTERSECT",VERTEX,{"derivedFrom":[subQ1,subQ0]});Q335=makeQuery(id+"F0.imprint","IMPRINT",FACE,{"disambiguationData":[TD([[makeQuery(id+"F0.imprint","IMPRINT",EDGE,{"disambiguationData":[TD([[subQ2,-1.0]])],"derivedFrom":subQ1}),1.0]])]});}
            var Q336;
            {var subQ0=sQuery(id+"F0.wireOp",EDGE,"E35");var subQ1=sQuery(id+"F0.wireOp",EDGE,"E11");var subQ2=makeQuery(id+"F0.imprint","INTERSECT",VERTEX,{"derivedFrom":[subQ1,subQ0]});Q336=makeQuery(id+"F0.imprint","IMPRINT",FACE,{"disambiguationData":[TD([[makeQuery(id+"F0.imprint","IMPRINT",EDGE,{"disambiguationData":[TD([[subQ2,-1.0]])],"derivedFrom":subQ1}),1.0]])]});}
            var Q337;
            {var subQ0=sQuery(id+"F0.wireOp",EDGE,"E33");var subQ1=sQuery(id+"F0.wireOp",EDGE,"E11");var subQ2=makeQuery(id+"F0.imprint","INTERSECT",VERTEX,{"derivedFrom":[subQ1,subQ0]});Q337=makeQuery(id+"F0.imprint","IMPRINT",FACE,{"disambiguationData":[TD([[makeQuery(id+"F0.imprint","IMPRINT",EDGE,{"disambiguationData":[TD([[subQ2,-1.0]])],"derivedFrom":subQ1}),1.0]])]});}
            var Q338;
            {var subQ0=sQuery(id+"F0.wireOp",EDGE,"E19");var subQ1=sQuery(id+"F0.wireOp",EDGE,"E11");var subQ2=makeQuery(id+"F0.imprint","INTERSECT",VERTEX,{"derivedFrom":[subQ1,subQ0]});Q338=makeQuery(id+"F0.imprint","IMPRINT",FACE,{"disambiguationData":[TD([[makeQuery(id+"F0.imprint","IMPRINT",EDGE,{"disambiguationData":[TD([[subQ2,-1.0]])],"derivedFrom":subQ1}),1.0]])]});}
            var Q339;
            {var subQ0=sQuery(id+"F0.wireOp",EDGE,"E25");var subQ1=sQuery(id+"F0.wireOp",EDGE,"E9");var subQ2=makeQuery(id+"F0.imprint","INTERSECT",VERTEX,{"derivedFrom":[subQ1,subQ0]});Q339=makeQuery(id+"F0.imprint","IMPRINT",FACE,{"disambiguationData":[TD([[makeQuery(id+"F0.imprint","IMPRINT",EDGE,{"disambiguationData":[TD([[subQ2,-1.0]])],"derivedFrom":subQ1}),1.0]])]});}
            var Q340;
            {var subQ0=sQuery(id+"F0.wireOp",EDGE,"E25");var subQ1=sQuery(id+"F0.wireOp",EDGE,"E7");var subQ2=makeQuery(id+"F0.imprint","INTERSECT",VERTEX,{"derivedFrom":[subQ1,subQ0]});Q340=makeQuery(id+"F0.imprint","IMPRINT",FACE,{"disambiguationData":[TD([[makeQuery(id+"F0.imprint","IMPRINT",EDGE,{"disambiguationData":[TD([[subQ2,-1.0]])],"derivedFrom":subQ1}),1.0]])]});}
            var Q341;
            {var subQ0=sQuery(id+"F0.wireOp",EDGE,"E35");var subQ1=sQuery(id+"F0.wireOp",EDGE,"E13");var subQ2=makeQuery(id+"F0.imprint","INTERSECT",VERTEX,{"derivedFrom":[subQ1,subQ0]});Q341=makeQuery(id+"F0.imprint","IMPRINT",FACE,{"disambiguationData":[TD([[makeQuery(id+"F0.imprint","IMPRINT",EDGE,{"disambiguationData":[TD([[subQ2,-1.0]])],"derivedFrom":subQ1}),1.0]])]});}
            var Q342;
            {var subQ0=sQuery(id+"F0.wireOp",EDGE,"E33");var subQ1=sQuery(id+"F0.wireOp",EDGE,"E13");var subQ2=makeQuery(id+"F0.imprint","INTERSECT",VERTEX,{"derivedFrom":[subQ1,subQ0]});Q342=makeQuery(id+"F0.imprint","IMPRINT",FACE,{"disambiguationData":[TD([[makeQuery(id+"F0.imprint","IMPRINT",EDGE,{"disambiguationData":[TD([[subQ2,-1.0]])],"derivedFrom":subQ1}),1.0]])]});}
            var Q343;
            {var subQ0=sQuery(id+"F0.wireOp",EDGE,"E27");var subQ1=sQuery(id+"F0.wireOp",EDGE,"E9");var subQ2=makeQuery(id+"F0.imprint","INTERSECT",VERTEX,{"derivedFrom":[subQ1,subQ0]});Q343=makeQuery(id+"F0.imprint","IMPRINT",FACE,{"disambiguationData":[TD([[makeQuery(id+"F0.imprint","IMPRINT",EDGE,{"disambiguationData":[TD([[subQ2,-1.0]])],"derivedFrom":subQ1}),1.0]])]});}
            var Q344;
            {var subQ0=sQuery(id+"F0.wireOp",EDGE,"E31");var subQ1=sQuery(id+"F0.wireOp",EDGE,"E3");var subQ2=makeQuery(id+"F0.imprint","INTERSECT",VERTEX,{"derivedFrom":[subQ1,subQ0]});Q344=makeQuery(id+"F0.imprint","IMPRINT",FACE,{"disambiguationData":[TD([[makeQuery(id+"F0.imprint","IMPRINT",EDGE,{"disambiguationData":[TD([[subQ2,-1.0]])],"derivedFrom":subQ1}),1.0]])]});}
            var Q345;
            {var subQ0=sQuery(id+"F0.wireOp",EDGE,"E27");var subQ1=sQuery(id+"F0.wireOp",EDGE,"E3");var subQ2=makeQuery(id+"F0.imprint","INTERSECT",VERTEX,{"derivedFrom":[subQ1,subQ0]});Q345=makeQuery(id+"F0.imprint","IMPRINT",FACE,{"disambiguationData":[TD([[makeQuery(id+"F0.imprint","IMPRINT",EDGE,{"disambiguationData":[TD([[subQ2,-1.0]])],"derivedFrom":subQ1}),1.0]])]});}
            var Q346;
            {var subQ0=sQuery(id+"F0.wireOp",EDGE,"E35");var subQ1=sQuery(id+"F0.wireOp",EDGE,"E3");var subQ2=makeQuery(id+"F0.imprint","INTERSECT",VERTEX,{"derivedFrom":[subQ1,subQ0]});Q346=makeQuery(id+"F0.imprint","IMPRINT",FACE,{"disambiguationData":[TD([[makeQuery(id+"F0.imprint","IMPRINT",EDGE,{"disambiguationData":[TD([[subQ2,-1.0]])],"derivedFrom":subQ1}),1.0]])]});}
            var Q347;
            {var subQ0=sQuery(id+"F0.wireOp",EDGE,"E33");var subQ1=sQuery(id+"F0.wireOp",EDGE,"E3");var subQ2=makeQuery(id+"F0.imprint","INTERSECT",VERTEX,{"derivedFrom":[subQ1,subQ0]});Q347=makeQuery(id+"F0.imprint","IMPRINT",FACE,{"disambiguationData":[TD([[makeQuery(id+"F0.imprint","IMPRINT",EDGE,{"disambiguationData":[TD([[subQ2,-1.0]])],"derivedFrom":subQ1}),1.0]])]});}
            var Q348;
            {var subQ0=sQuery(id+"F0.wireOp",EDGE,"E29");var subQ1=sQuery(id+"F0.wireOp",EDGE,"E3");var subQ2=makeQuery(id+"F0.imprint","INTERSECT",VERTEX,{"derivedFrom":[subQ1,subQ0]});Q348=makeQuery(id+"F0.imprint","IMPRINT",FACE,{"disambiguationData":[TD([[makeQuery(id+"F0.imprint","IMPRINT",EDGE,{"disambiguationData":[TD([[subQ2,-1.0]])],"derivedFrom":subQ1}),1.0]])]});}
            var Q349;
            {var subQ0=sQuery(id+"F0.wireOp",EDGE,"E21");var subQ1=sQuery(id+"F0.wireOp",EDGE,"E3");var subQ2=makeQuery(id+"F0.imprint","INTERSECT",VERTEX,{"derivedFrom":[subQ1,subQ0]});Q349=makeQuery(id+"F0.imprint","IMPRINT",FACE,{"disambiguationData":[TD([[makeQuery(id+"F0.imprint","IMPRINT",EDGE,{"disambiguationData":[TD([[subQ2,-1.0]])],"derivedFrom":subQ1}),1.0]])]});}
            var Q350;
            {var subQ0=sQuery(id+"F0.wireOp",EDGE,"E19");var subQ1=sQuery(id+"F0.wireOp",EDGE,"E3");var subQ2=makeQuery(id+"F0.imprint","INTERSECT",VERTEX,{"derivedFrom":[subQ1,subQ0]});Q350=makeQuery(id+"F0.imprint","IMPRINT",FACE,{"disambiguationData":[TD([[makeQuery(id+"F0.imprint","IMPRINT",EDGE,{"disambiguationData":[TD([[subQ2,-1.0]])],"derivedFrom":subQ1}),1.0]])]});}
            var Q351;
            {var subQ0=sQuery(id+"F0.wireOp",EDGE,"E23");var subQ1=sQuery(id+"F0.wireOp",EDGE,"E3");var subQ2=makeQuery(id+"F0.imprint","INTERSECT",VERTEX,{"derivedFrom":[subQ1,subQ0]});Q351=makeQuery(id+"F0.imprint","IMPRINT",FACE,{"disambiguationData":[TD([[makeQuery(id+"F0.imprint","IMPRINT",EDGE,{"disambiguationData":[TD([[subQ2,-1.0]])],"derivedFrom":subQ1}),1.0]])]});}
            extrude(context, id + "F1", {"entities" : qUnion([Q0, Q1, Q2, Q3, Q4, Q5, Q6, Q7, Q8, Q9, Q10, Q11, Q12, Q13, Q14, Q15, Q16, Q17, Q18, Q19, Q20, Q21, Q22, Q23, Q24, Q25, Q26, Q27, Q28, Q29, Q30, Q31, Q32, Q33, Q34, Q35, Q36, Q37, Q38, Q39, Q40, Q41, Q42, Q43, Q44, Q45, Q46, Q47, Q48, Q49, Q50, Q51, Q52, Q53, Q54, Q55, Q56, Q57, Q58, Q59, Q60, Q61, Q62, Q63, Q64, Q65, Q66, Q67, Q68, Q69, Q70, Q71, Q72, Q73, Q74, Q75, Q76, Q77, Q78, Q79, Q80, Q81, Q82, Q83, Q84, Q85, Q86, Q87, Q88, Q89, Q90, Q91, Q92, Q93, Q94, Q95, Q96, Q97, Q98, Q99, Q100, Q101, Q102, Q103, Q104, Q105, Q106, Q107, Q108, Q109, Q110, Q111, Q112, Q113, Q114, Q115, Q116, Q117, Q118, Q119, Q120, Q121, Q122, Q123, Q124, Q125, Q126, Q127, Q128, Q129, Q130, Q131, Q132, Q133, Q134, Q135, Q136, Q137, Q138, Q139, Q140, Q141, Q142, Q143, Q144, Q145, Q146, Q147, Q148, Q149, Q150, Q151, Q152, Q153, Q154, Q155, Q156, Q157, Q158, Q159, Q160, Q161, Q162, Q163, Q164, Q165, Q166, Q167, Q168, Q169, Q170, Q171, Q172, Q173, Q174, Q175, Q176, Q177, Q178, Q179, Q180, Q181, Q182, Q183, Q184, Q185, Q186, Q187, Q188, Q189, Q190, Q191, Q192, Q193, Q194, Q195, Q196, Q197, Q198, Q199, Q200, Q201, Q202, Q203, Q204, Q205, Q206, Q207, Q208, Q209, Q210, Q211, Q212, Q213, Q214, Q215, Q216, Q217, Q218, Q219, Q220, Q221, Q222, Q223, Q224, Q225, Q226, Q227, Q228, Q229, Q230, Q231, Q232, Q233, Q234, Q235, Q236, Q237, Q238, Q239, Q240, Q241, Q242, Q243, Q244, Q245, Q246, Q247, Q248, Q249, Q250, Q251, Q252, Q253, Q254, Q255, Q256, Q257, Q258, Q259, Q260, Q261, Q262, Q263, Q264, Q265, Q266, Q267, Q268, Q269, Q270, Q271, Q272, Q273, Q274, Q275, Q276, Q277, Q278, Q279, Q280, Q281, Q282, Q283, Q284, Q285, Q286, Q287, Q288, Q289, Q290, Q291, Q292, Q293, Q294, Q295, Q296, Q297, Q298, Q299, Q300, Q301, Q302, Q303, Q304, Q305, Q306, Q307, Q308, Q309, Q310, Q311, Q312, Q313, Q314, Q315, Q316, Q317, Q318, Q319, Q320, Q321, Q322, Q323, Q324, Q325, Q326, Q327, Q328, Q329, Q330, Q331, Q332, Q333, Q334, Q335, Q336, Q337, Q338, Q339, Q340, Q341, Q342, Q343, Q344, Q345, Q346, Q347, Q348, Q349, Q350, Q351]), "depth" : 4 * mm, "offsetDistance" : 25 * mm});
        }
        {
            var Q0;
            Q0=makeQuery(id+"F1.opExtrude","SWEPT_FACE",FACE,{"disambiguationData":[OSD([sQuery(id+"F0.wireOp",EDGE,"E0.left")])]});
            var Q1;
            Q1=makeQuery(id+"F1.opExtrude","SWEPT_FACE",FACE,{"disambiguationData":[OSD([sQuery(id+"F0.wireOp",EDGE,"E0.top")])]});
            var Q2;
            Q2=makeQuery(id+"F1.opExtrude","SWEPT_FACE",FACE,{"disambiguationData":[OSD([sQuery(id+"F0.wireOp",EDGE,"E0.right")])]});
            var Q3;
            Q3=makeQuery(id+"F1.opExtrude","SWEPT_FACE",FACE,{"disambiguationData":[OSD([sQuery(id+"F0.wireOp",EDGE,"E0.bottom")])]});
            fillet(context, id + "F2", {"entities" : qUnion([Q0, Q1, Q2, Q3]), "radius" : 0.1 * mm, "tangentPropagation" : true, "allowEdgeOverflow" : false});
        }
    });
